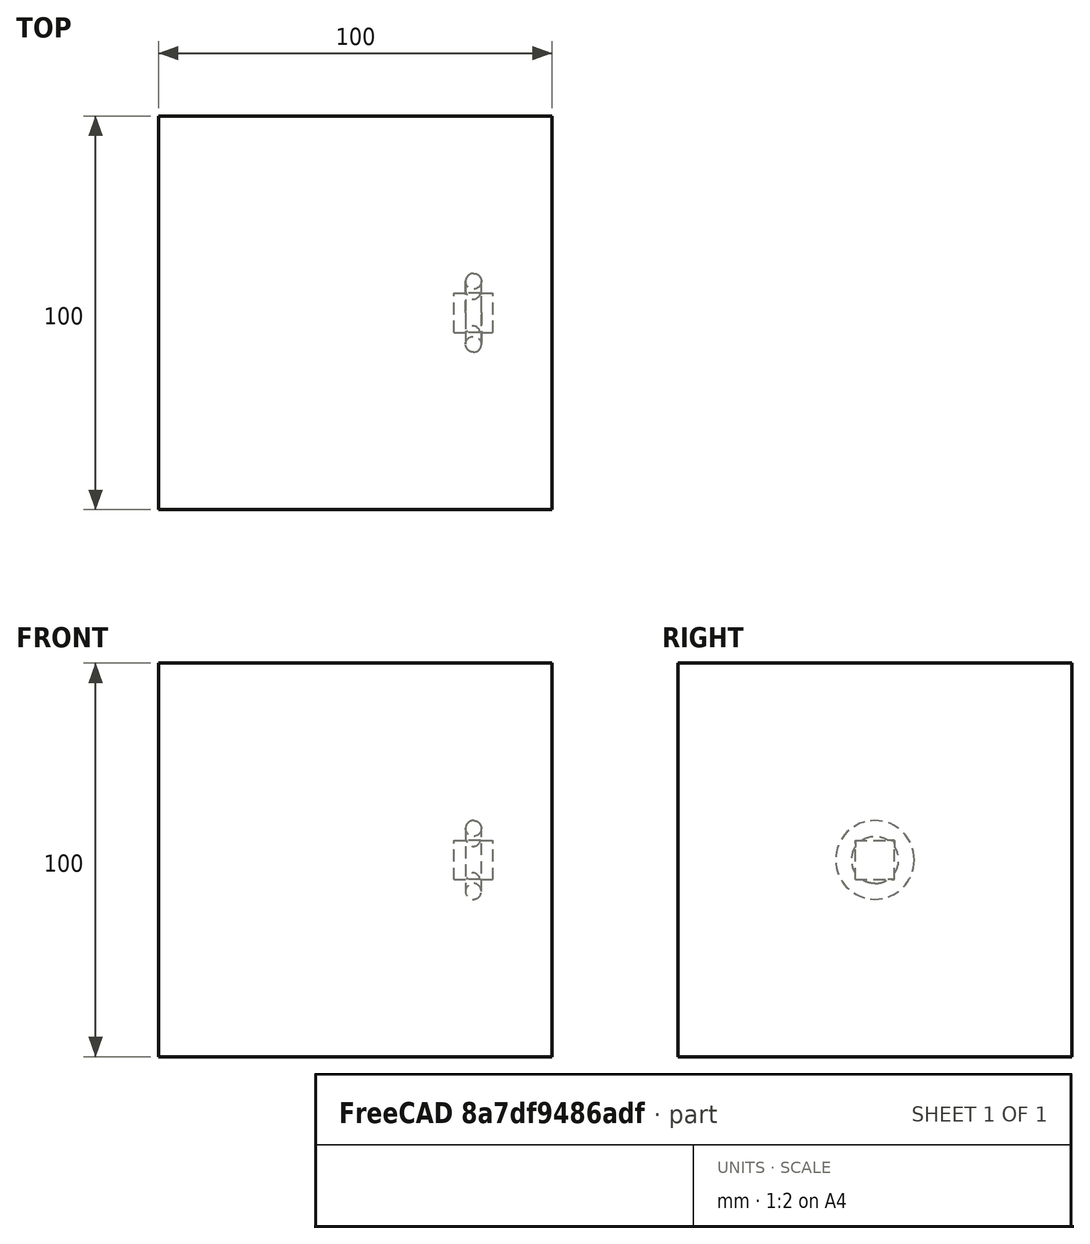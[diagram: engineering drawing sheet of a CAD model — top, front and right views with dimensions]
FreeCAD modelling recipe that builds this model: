
FCSTD DOCUMENT  (FreeCAD 1.0R39109 (Git))
Label: polarArray-7
License: All rights reserved
objects: App::DocumentObjectGroupPython×1251, Part::FeaturePython×4, App::Part×2, Part::MultiFuse×1
note: 4 computed .brp shape members not serialized (recipe doc carries the construction recipe); baked Part::Feature solids carry a one-line shape summary decoded from their .brp

FEATURE [App::DocumentObjectGroupPython] HALFPI  # scripted group (container) (typed FeaturePython)
  name = HALFPI
  value = pi/2.
FEATURE [App::DocumentObjectGroupPython] PI  # scripted group (container) (typed FeaturePython)
  name = PI
  value = 1.*pi
FEATURE [App::DocumentObjectGroupPython] TWOPI  # scripted group (container) (typed FeaturePython)
  name = TWOPI
  value = 2.*pi
FEATURE [App::DocumentObjectGroupPython] Constants  # scripted group (container) (typed FeaturePython)
  Group = -> [HALFPI,PI,TWOPI]
FEATURE [App::DocumentObjectGroupPython] Variables  # scripted group (container) (typed FeaturePython)
FEATURE [App::DocumentObjectGroupPython] Quantities  # scripted group (container) (typed FeaturePython)
FEATURE [App::DocumentObjectGroupPython] Isotopes  # scripted group (container) (typed FeaturePython)
FEATURE [App::DocumentObjectGroupPython] Elements  # scripted group (container) (typed FeaturePython)
FEATURE [App::DocumentObjectGroupPython] Matrix  # scripted group (container) (typed FeaturePython)
FEATURE [App::DocumentObjectGroupPython] Surfaces  # scripted group (container) (typed FeaturePython)
FEATURE [App::DocumentObjectGroupPython] Opticals  # scripted group (container) (typed FeaturePython)
  Group = -> [Matrix,Surfaces]
FEATURE [App::DocumentObjectGroupPython] G4Isotopes  # scripted group (container) (typed FeaturePython)
FEATURE [App::DocumentObjectGroupPython] H_element  # scripted group (container) (typed FeaturePython)
  Z = 1
  atom_value = 1.008
  formula = H
  name = H_element
FEATURE [App::DocumentObjectGroupPython] He_element  # scripted group (container) (typed FeaturePython)
  Z = 2
  atom_value = 4.0026
  formula = He
  name = He_element
FEATURE [App::DocumentObjectGroupPython] Li_element  # scripted group (container) (typed FeaturePython)
  Z = 3
  atom_value = 6.94
  formula = Li
  name = Li_element
FEATURE [App::DocumentObjectGroupPython] Be_element  # scripted group (container) (typed FeaturePython)
  Z = 4
  atom_value = 9.01218
  formula = Be
  name = Be_element
FEATURE [App::DocumentObjectGroupPython] B_element  # scripted group (container) (typed FeaturePython)
  Z = 5
  atom_value = 10.81
  formula = B
  name = B_element
FEATURE [App::DocumentObjectGroupPython] C_element  # scripted group (container) (typed FeaturePython)
  Z = 6
  atom_value = 12.011
  formula = C
  name = C_element
FEATURE [App::DocumentObjectGroupPython] N_element  # scripted group (container) (typed FeaturePython)
  Z = 7
  atom_value = 14.007
  formula = N
  name = N_element
FEATURE [App::DocumentObjectGroupPython] O_element  # scripted group (container) (typed FeaturePython)
  Z = 8
  atom_value = 15.999
  formula = O
  name = O_element
FEATURE [App::DocumentObjectGroupPython] F_element  # scripted group (container) (typed FeaturePython)
  Z = 9
  atom_value = 18.9984
  formula = F
  name = F_element
FEATURE [App::DocumentObjectGroupPython] Ne_element  # scripted group (container) (typed FeaturePython)
  Z = 10
  atom_value = 20.1797
  formula = Ne
  name = Ne_element
FEATURE [App::DocumentObjectGroupPython] Na_element  # scripted group (container) (typed FeaturePython)
  Z = 11
  atom_value = 22.9898
  formula = Na
  name = Na_element
FEATURE [App::DocumentObjectGroupPython] Mg_element  # scripted group (container) (typed FeaturePython)
  Z = 12
  atom_value = 24.305
  formula = Mg
  name = Mg_element
FEATURE [App::DocumentObjectGroupPython] Al_element  # scripted group (container) (typed FeaturePython)
  Z = 13
  atom_value = 26.9815
  formula = Al
  name = Al_element
FEATURE [App::DocumentObjectGroupPython] Si_element  # scripted group (container) (typed FeaturePython)
  Z = 14
  atom_value = 28.085
  formula = Si
  name = Si_element
FEATURE [App::DocumentObjectGroupPython] P_element  # scripted group (container) (typed FeaturePython)
  Z = 15
  atom_value = 30.9738
  formula = P
  name = P_element
FEATURE [App::DocumentObjectGroupPython] S_element  # scripted group (container) (typed FeaturePython)
  Z = 16
  atom_value = 32.06
  formula = S
  name = S_element
FEATURE [App::DocumentObjectGroupPython] Cl_element  # scripted group (container) (typed FeaturePython)
  Z = 17
  atom_value = 35.45
  formula = Cl
  name = Cl_element
FEATURE [App::DocumentObjectGroupPython] Ar_element  # scripted group (container) (typed FeaturePython)
  Z = 18
  atom_value = 39.95
  formula = Ar
  name = Ar_element
FEATURE [App::DocumentObjectGroupPython] K_element  # scripted group (container) (typed FeaturePython)
  Z = 19
  atom_value = 39.0983
  formula = K
  name = K_element
FEATURE [App::DocumentObjectGroupPython] Ca_element  # scripted group (container) (typed FeaturePython)
  Z = 20
  atom_value = 40.078
  formula = Ca
  name = Ca_element
FEATURE [App::DocumentObjectGroupPython] Sc_element  # scripted group (container) (typed FeaturePython)
  Z = 21
  atom_value = 44.9559
  formula = Sc
  name = Sc_element
FEATURE [App::DocumentObjectGroupPython] Ti_element  # scripted group (container) (typed FeaturePython)
  Z = 22
  atom_value = 47.867
  formula = Ti
  name = Ti_element
FEATURE [App::DocumentObjectGroupPython] V_element  # scripted group (container) (typed FeaturePython)
  Z = 23
  atom_value = 50.9415
  formula = V
  name = V_element
FEATURE [App::DocumentObjectGroupPython] Cr_element  # scripted group (container) (typed FeaturePython)
  Z = 24
  atom_value = 51.9961
  formula = Cr
  name = Cr_element
FEATURE [App::DocumentObjectGroupPython] Mn_element  # scripted group (container) (typed FeaturePython)
  Z = 25
  atom_value = 54.938
  formula = Mn
  name = Mn_element
FEATURE [App::DocumentObjectGroupPython] Fe_element  # scripted group (container) (typed FeaturePython)
  Z = 26
  atom_value = 55.845
  formula = Fe
  name = Fe_element
FEATURE [App::DocumentObjectGroupPython] Co_element  # scripted group (container) (typed FeaturePython)
  Z = 27
  atom_value = 58.9332
  formula = Co
  name = Co_element
FEATURE [App::DocumentObjectGroupPython] Ni_element  # scripted group (container) (typed FeaturePython)
  Z = 28
  atom_value = 58.6934
  formula = Ni
  name = Ni_element
FEATURE [App::DocumentObjectGroupPython] Cu_element  # scripted group (container) (typed FeaturePython)
  Z = 29
  atom_value = 63.546
  formula = Cu
  name = Cu_element
FEATURE [App::DocumentObjectGroupPython] Zn_element  # scripted group (container) (typed FeaturePython)
  Z = 30
  atom_value = 65.38
  formula = Zn
  name = Zn_element
FEATURE [App::DocumentObjectGroupPython] Ga_element  # scripted group (container) (typed FeaturePython)
  Z = 31
  atom_value = 69.723
  formula = Ga
  name = Ga_element
FEATURE [App::DocumentObjectGroupPython] Ge_element  # scripted group (container) (typed FeaturePython)
  Z = 32
  atom_value = 72.63
  formula = Ge
  name = Ge_element
FEATURE [App::DocumentObjectGroupPython] As_element  # scripted group (container) (typed FeaturePython)
  Z = 33
  atom_value = 74.9216
  formula = As
  name = As_element
FEATURE [App::DocumentObjectGroupPython] Se_element  # scripted group (container) (typed FeaturePython)
  Z = 34
  atom_value = 78.971
  formula = Se
  name = Se_element
FEATURE [App::DocumentObjectGroupPython] Br_element  # scripted group (container) (typed FeaturePython)
  Z = 35
  atom_value = 79.904
  formula = Br
  name = Br_element
FEATURE [App::DocumentObjectGroupPython] Kr_element  # scripted group (container) (typed FeaturePython)
  Z = 36
  atom_value = 83.798
  formula = Kr
  name = Kr_element
FEATURE [App::DocumentObjectGroupPython] Rb_element  # scripted group (container) (typed FeaturePython)
  Z = 37
  atom_value = 85.4678
  formula = Rb
  name = Rb_element
FEATURE [App::DocumentObjectGroupPython] Sr_element  # scripted group (container) (typed FeaturePython)
  Z = 38
  atom_value = 87.62
  formula = Sr
  name = Sr_element
FEATURE [App::DocumentObjectGroupPython] Y_element  # scripted group (container) (typed FeaturePython)
  Z = 39
  atom_value = 88.9058
  formula = Y
  name = Y_element
FEATURE [App::DocumentObjectGroupPython] Zr_element  # scripted group (container) (typed FeaturePython)
  Z = 40
  atom_value = 91.224
  formula = Zr
  name = Zr_element
FEATURE [App::DocumentObjectGroupPython] Nb_element  # scripted group (container) (typed FeaturePython)
  Z = 41
  atom_value = 92.9064
  formula = Nb
  name = Nb_element
FEATURE [App::DocumentObjectGroupPython] Mo_element  # scripted group (container) (typed FeaturePython)
  Z = 42
  atom_value = 95.95
  formula = Mo
  name = Mo_element
FEATURE [App::DocumentObjectGroupPython] Tc_element  # scripted group (container) (typed FeaturePython)
  Z = 43
  atom_value = 97
  formula = Tc
  name = Tc_element
FEATURE [App::DocumentObjectGroupPython] Ru_element  # scripted group (container) (typed FeaturePython)
  Z = 44
  atom_value = 101.07
  formula = Ru
  name = Ru_element
FEATURE [App::DocumentObjectGroupPython] Rh_element  # scripted group (container) (typed FeaturePython)
  Z = 45
  atom_value = 102.905
  formula = Rh
  name = Rh_element
FEATURE [App::DocumentObjectGroupPython] Pd_element  # scripted group (container) (typed FeaturePython)
  Z = 46
  atom_value = 106.42
  formula = Pd
  name = Pd_element
FEATURE [App::DocumentObjectGroupPython] Ag_element  # scripted group (container) (typed FeaturePython)
  Z = 47
  atom_value = 107.868
  formula = Ag
  name = Ag_element
FEATURE [App::DocumentObjectGroupPython] Cd_element  # scripted group (container) (typed FeaturePython)
  Z = 48
  atom_value = 112.414
  formula = Cd
  name = Cd_element
FEATURE [App::DocumentObjectGroupPython] In_element  # scripted group (container) (typed FeaturePython)
  Z = 49
  atom_value = 114.818
  formula = In
  name = In_element
FEATURE [App::DocumentObjectGroupPython] Sn_element  # scripted group (container) (typed FeaturePython)
  Z = 50
  atom_value = 118.71
  formula = Sn
  name = Sn_element
FEATURE [App::DocumentObjectGroupPython] Sb_element  # scripted group (container) (typed FeaturePython)
  Z = 51
  atom_value = 121.76
  formula = Sb
  name = Sb_element
FEATURE [App::DocumentObjectGroupPython] Te_element  # scripted group (container) (typed FeaturePython)
  Z = 52
  atom_value = 127.6
  formula = Te
  name = Te_element
FEATURE [App::DocumentObjectGroupPython] I_element  # scripted group (container) (typed FeaturePython)
  Z = 53
  atom_value = 126.904
  formula = I
  name = I_element
FEATURE [App::DocumentObjectGroupPython] Xe_element  # scripted group (container) (typed FeaturePython)
  Z = 54
  atom_value = 131.293
  formula = Xe
  name = Xe_element
FEATURE [App::DocumentObjectGroupPython] Cs_element  # scripted group (container) (typed FeaturePython)
  Z = 55
  atom_value = 132.905
  formula = Cs
  name = Cs_element
FEATURE [App::DocumentObjectGroupPython] Ba_element  # scripted group (container) (typed FeaturePython)
  Z = 56
  atom_value = 137.327
  formula = Ba
  name = Ba_element
FEATURE [App::DocumentObjectGroupPython] La_element  # scripted group (container) (typed FeaturePython)
  Z = 57
  atom_value = 138.905
  formula = La
  name = La_element
FEATURE [App::DocumentObjectGroupPython] Ce_element  # scripted group (container) (typed FeaturePython)
  Z = 58
  atom_value = 140.116
  formula = Ce
  name = Ce_element
FEATURE [App::DocumentObjectGroupPython] Pr_element  # scripted group (container) (typed FeaturePython)
  Z = 59
  atom_value = 140.908
  formula = Pr
  name = Pr_element
FEATURE [App::DocumentObjectGroupPython] Nd_element  # scripted group (container) (typed FeaturePython)
  Z = 60
  atom_value = 144.242
  formula = Nd
  name = Nd_element
FEATURE [App::DocumentObjectGroupPython] Pm_element  # scripted group (container) (typed FeaturePython)
  Z = 61
  atom_value = 145
  formula = Pm
  name = Pm_element
FEATURE [App::DocumentObjectGroupPython] Sm_element  # scripted group (container) (typed FeaturePython)
  Z = 62
  atom_value = 150.36
  formula = Sm
  name = Sm_element
FEATURE [App::DocumentObjectGroupPython] Eu_element  # scripted group (container) (typed FeaturePython)
  Z = 63
  atom_value = 151.964
  formula = Eu
  name = Eu_element
FEATURE [App::DocumentObjectGroupPython] Gd_element  # scripted group (container) (typed FeaturePython)
  Z = 64
  atom_value = 157.25
  formula = Gd
  name = Gd_element
FEATURE [App::DocumentObjectGroupPython] Tb_element  # scripted group (container) (typed FeaturePython)
  Z = 65
  atom_value = 158.925
  formula = Tb
  name = Tb_element
FEATURE [App::DocumentObjectGroupPython] Dy_element  # scripted group (container) (typed FeaturePython)
  Z = 66
  atom_value = 162.5
  formula = Dy
  name = Dy_element
FEATURE [App::DocumentObjectGroupPython] Ho_element  # scripted group (container) (typed FeaturePython)
  Z = 67
  atom_value = 164.93
  formula = Ho
  name = Ho_element
FEATURE [App::DocumentObjectGroupPython] Er_element  # scripted group (container) (typed FeaturePython)
  Z = 68
  atom_value = 167.259
  formula = Er
  name = Er_element
FEATURE [App::DocumentObjectGroupPython] Tm_element  # scripted group (container) (typed FeaturePython)
  Z = 69
  atom_value = 168.934
  formula = Tm
  name = Tm_element
FEATURE [App::DocumentObjectGroupPython] Yb_element  # scripted group (container) (typed FeaturePython)
  Z = 70
  atom_value = 173.045
  formula = Yb
  name = Yb_element
FEATURE [App::DocumentObjectGroupPython] Lu_element  # scripted group (container) (typed FeaturePython)
  Z = 71
  atom_value = 174.967
  formula = Lu
  name = Lu_element
FEATURE [App::DocumentObjectGroupPython] Hf_element  # scripted group (container) (typed FeaturePython)
  Z = 72
  atom_value = 178.49
  formula = Hf
  name = Hf_element
FEATURE [App::DocumentObjectGroupPython] Ta_element  # scripted group (container) (typed FeaturePython)
  Z = 73
  atom_value = 180.948
  formula = Ta
  name = Ta_element
FEATURE [App::DocumentObjectGroupPython] W_element  # scripted group (container) (typed FeaturePython)
  Z = 74
  atom_value = 183.84
  formula = W
  name = W_element
FEATURE [App::DocumentObjectGroupPython] Re_element  # scripted group (container) (typed FeaturePython)
  Z = 75
  atom_value = 186.207
  formula = Re
  name = Re_element
FEATURE [App::DocumentObjectGroupPython] Os_element  # scripted group (container) (typed FeaturePython)
  Z = 76
  atom_value = 190.23
  formula = Os
  name = Os_element
FEATURE [App::DocumentObjectGroupPython] Ir_element  # scripted group (container) (typed FeaturePython)
  Z = 77
  atom_value = 192.217
  formula = Ir
  name = Ir_element
FEATURE [App::DocumentObjectGroupPython] Pt_element  # scripted group (container) (typed FeaturePython)
  Z = 78
  atom_value = 195.084
  formula = Pt
  name = Pt_element
FEATURE [App::DocumentObjectGroupPython] Au_element  # scripted group (container) (typed FeaturePython)
  Z = 79
  atom_value = 196.967
  formula = Au
  name = Au_element
FEATURE [App::DocumentObjectGroupPython] Hg_element  # scripted group (container) (typed FeaturePython)
  Z = 80
  atom_value = 200.592
  formula = Hg
  name = Hg_element
FEATURE [App::DocumentObjectGroupPython] Tl_element  # scripted group (container) (typed FeaturePython)
  Z = 81
  atom_value = 204.38
  formula = Tl
  name = Tl_element
FEATURE [App::DocumentObjectGroupPython] Pb_element  # scripted group (container) (typed FeaturePython)
  Z = 82
  atom_value = 207.2
  formula = Pb
  name = Pb_element
FEATURE [App::DocumentObjectGroupPython] Bi_element  # scripted group (container) (typed FeaturePython)
  Z = 83
  atom_value = 208.98
  formula = Bi
  name = Bi_element
FEATURE [App::DocumentObjectGroupPython] Po_element  # scripted group (container) (typed FeaturePython)
  Z = 84
  atom_value = 209
  formula = Po
  name = Po_element
FEATURE [App::DocumentObjectGroupPython] At_element  # scripted group (container) (typed FeaturePython)
  Z = 85
  atom_value = 210
  formula = At
  name = At_element
FEATURE [App::DocumentObjectGroupPython] Rn_element  # scripted group (container) (typed FeaturePython)
  Z = 86
  atom_value = 222
  formula = Rn
  name = Rn_element
FEATURE [App::DocumentObjectGroupPython] Fr_element  # scripted group (container) (typed FeaturePython)
  Z = 87
  atom_value = 223
  formula = Fr
  name = Fr_element
FEATURE [App::DocumentObjectGroupPython] Ra_element  # scripted group (container) (typed FeaturePython)
  Z = 88
  atom_value = 226
  formula = Ra
  name = Ra_element
FEATURE [App::DocumentObjectGroupPython] Ac_element  # scripted group (container) (typed FeaturePython)
  Z = 89
  atom_value = 227
  formula = Ac
  name = Ac_element
FEATURE [App::DocumentObjectGroupPython] Th_element  # scripted group (container) (typed FeaturePython)
  Z = 90
  atom_value = 232.038
  formula = Th
  name = Th_element
FEATURE [App::DocumentObjectGroupPython] Pa_element  # scripted group (container) (typed FeaturePython)
  Z = 91
  atom_value = 231.036
  formula = Pa
  name = Pa_element
FEATURE [App::DocumentObjectGroupPython] U_element  # scripted group (container) (typed FeaturePython)
  Z = 92
  atom_value = 238.029
  formula = U
  name = U_element
FEATURE [App::DocumentObjectGroupPython] Np_element  # scripted group (container) (typed FeaturePython)
  Z = 93
  atom_value = 237
  formula = Np
  name = Np_element
FEATURE [App::DocumentObjectGroupPython] Pu_element  # scripted group (container) (typed FeaturePython)
  Z = 94
  atom_value = 244
  formula = Pu
  name = Pu_element
FEATURE [App::DocumentObjectGroupPython] Am_element  # scripted group (container) (typed FeaturePython)
  Z = 95
  atom_value = 243
  formula = Am
  name = Am_element
FEATURE [App::DocumentObjectGroupPython] Cm_element  # scripted group (container) (typed FeaturePython)
  Z = 96
  atom_value = 247
  formula = Cm
  name = Cm_element
FEATURE [App::DocumentObjectGroupPython] Bk_element  # scripted group (container) (typed FeaturePython)
  Z = 97
  atom_value = 247
  formula = Bk
  name = Bk_element
FEATURE [App::DocumentObjectGroupPython] Cf_element  # scripted group (container) (typed FeaturePython)
  Z = 98
  atom_value = 251
  formula = Cf
  name = Cf_element
FEATURE [App::DocumentObjectGroupPython] G4Elements  # scripted group (container) (typed FeaturePython)
  Group = -> [H_element,He_element,Li_element,Be_element,B_element,C_element,N_element,O_element,F_element,Ne_element,Na_element,Mg_element,Al_element,Si_element,P_element,S_element,Cl_element,Ar_element,K_element,Ca_element,Sc_element,Ti_element,V_element,Cr_element,Mn_element,Fe_element,Co_element,Ni_element,Cu_element,Zn_element,Ga_element,Ge_element,As_element,Se_element,Br_element,Kr_element,Rb_element,+61 more]
FEATURE [App::DocumentObjectGroupPython] H_element001  label="H_element : 0.101"  # scripted group (container) (typed FeaturePython)
  n = 0.101327
FEATURE [App::DocumentObjectGroupPython] C_element001  label="C_element : 0.775"  # scripted group (container) (typed FeaturePython)
  n = 0.7755
FEATURE [App::DocumentObjectGroupPython] N_element001  label="N_element : 0.035"  # scripted group (container) (typed FeaturePython)
  n = 0.035057
FEATURE [App::DocumentObjectGroupPython] O_element001  label="O_element : 0.052"  # scripted group (container) (typed FeaturePython)
  n = 0.0523159
FEATURE [App::DocumentObjectGroupPython] F_element001  label="F_element : 0.017"  # scripted group (container) (typed FeaturePython)
  n = 0.017422
FEATURE [App::DocumentObjectGroupPython] Ca_element001  label="Ca_element : 0.018"  # scripted group (container) (typed FeaturePython)
  n = 0.018378
FEATURE [App::DocumentObjectGroupPython] G4_A_150_TISSUE  label="G4_A-150_TISSUE"  # scripted group (container) (typed FeaturePython)
  Dunit = g/cm3
  Dvalue = 1.127
  Group = -> [H_element001,C_element001,N_element001,O_element001,F_element001,Ca_element001]
  conduct = 2
  density = 1
  expand = 3
  formula = G4_A-150_TISSUE
  name = G4_A-150_TISSUE
  specific = 4
FEATURE [App::DocumentObjectGroupPython] C_element002  label="C_element : 3"  # scripted group (container) (typed FeaturePython)
  n = 3
  ref = C_element
FEATURE [App::DocumentObjectGroupPython] H_element002  label="H_element : 6"  # scripted group (container) (typed FeaturePython)
  n = 6
  ref = H_element
FEATURE [App::DocumentObjectGroupPython] O_element002  label="O_element : 1"  # scripted group (container) (typed FeaturePython)
  n = 1
  ref = O_element
FEATURE [App::DocumentObjectGroupPython] G4_ACETONE  # scripted group (container) (typed FeaturePython)
  Dunit = g/cm3
  Dvalue = 0.7899
  Group = -> [C_element002,H_element002,O_element002]
  conduct = 2
  density = 1
  expand = 3
  formula = G4_ACETONE
  name = G4_ACETONE
  specific = 4
FEATURE [App::DocumentObjectGroupPython] C_element003  label="C_element : 2"  # scripted group (container) (typed FeaturePython)
  n = 2
  ref = C_element
FEATURE [App::DocumentObjectGroupPython] H_element003  label="H_element : 2"  # scripted group (container) (typed FeaturePython)
  n = 2
  ref = H_element
FEATURE [App::DocumentObjectGroupPython] G4_ACETYLENE  # scripted group (container) (typed FeaturePython)
  Dunit = g/cm3
  Dvalue = 0.0010967
  Group = -> [C_element003,H_element003]
  conduct = 2
  density = 1
  expand = 3
  formula = G4_ACETYLENE
  name = G4_ACETYLENE
  specific = 4
FEATURE [App::DocumentObjectGroupPython] C_element004  label="C_element : 5"  # scripted group (container) (typed FeaturePython)
  n = 5
  ref = C_element
FEATURE [App::DocumentObjectGroupPython] H_element004  label="H_element : 5"  # scripted group (container) (typed FeaturePython)
  n = 5
  ref = H_element
FEATURE [App::DocumentObjectGroupPython] N_element002  label="N_element : 5"  # scripted group (container) (typed FeaturePython)
  n = 5
  ref = N_element
FEATURE [App::DocumentObjectGroupPython] G4_ADENINE  # scripted group (container) (typed FeaturePython)
  Dunit = g/cm3
  Dvalue = 1.6
  Group = -> [C_element004,H_element004,N_element002]
  conduct = 2
  density = 1
  expand = 3
  formula = G4_ADENINE
  name = G4_ADENINE
  specific = 4
FEATURE [App::DocumentObjectGroupPython] H_element005  label="H_element : 0.114"  # scripted group (container) (typed FeaturePython)
  n = 0.114
FEATURE [App::DocumentObjectGroupPython] C_element005  label="C_element : 0.598"  # scripted group (container) (typed FeaturePython)
  n = 0.598
FEATURE [App::DocumentObjectGroupPython] N_element003  label="N_element : 0.007"  # scripted group (container) (typed FeaturePython)
  n = 0.007
FEATURE [App::DocumentObjectGroupPython] O_element003  label="O_element : 0.278"  # scripted group (container) (typed FeaturePython)
  n = 0.278
FEATURE [App::DocumentObjectGroupPython] Na_element001  label="Na_element : 0.001"  # scripted group (container) (typed FeaturePython)
  n = 0.001
FEATURE [App::DocumentObjectGroupPython] S_element001  label="S_element : 0.001"  # scripted group (container) (typed FeaturePython)
  n = 0.001
FEATURE [App::DocumentObjectGroupPython] Cl_element001  label="Cl_element : 0.001"  # scripted group (container) (typed FeaturePython)
  n = 0.001
FEATURE [App::DocumentObjectGroupPython] G4_ADIPOSE_TISSUE_ICRP  # scripted group (container) (typed FeaturePython)
  Dunit = g/cm3
  Dvalue = 0.95
  Group = -> [H_element005,C_element005,N_element003,O_element003,Na_element001,S_element001,Cl_element001]
  conduct = 2
  density = 1
  expand = 3
  formula = G4_ADIPOSE_TISSUE_ICRP
  name = G4_ADIPOSE_TISSUE_ICRP
  specific = 4
FEATURE [App::DocumentObjectGroupPython] C_element006  label="C_element : 0.000"  # scripted group (container) (typed FeaturePython)
  n = 0.000124
FEATURE [App::DocumentObjectGroupPython] N_element004  label="N_element : 0.755"  # scripted group (container) (typed FeaturePython)
  n = 0.755268
FEATURE [App::DocumentObjectGroupPython] O_element004  label="O_element : 0.232"  # scripted group (container) (typed FeaturePython)
  n = 0.231781
FEATURE [App::DocumentObjectGroupPython] Ar_element001  label="Ar_element : 0.013"  # scripted group (container) (typed FeaturePython)
  n = 0.012827
FEATURE [App::DocumentObjectGroupPython] G4_AIR  # scripted group (container) (typed FeaturePython)
  Dunit = g/cm3
  Dvalue = 0.00120479
  Group = -> [C_element006,N_element004,O_element004,Ar_element001]
  conduct = 2
  density = 1
  expand = 3
  formula = G4_AIR
  name = G4_AIR
  specific = 4
FEATURE [App::DocumentObjectGroupPython] C_element007  label="C_element : 006"  # scripted group (container) (typed FeaturePython)
  n = 3
  ref = C_element
FEATURE [App::DocumentObjectGroupPython] H_element006  label="H_element : 7"  # scripted group (container) (typed FeaturePython)
  n = 7
  ref = H_element
FEATURE [App::DocumentObjectGroupPython] N_element005  label="N_element : 1"  # scripted group (container) (typed FeaturePython)
  n = 1
  ref = N_element
FEATURE [App::DocumentObjectGroupPython] O_element005  label="O_element : 2"  # scripted group (container) (typed FeaturePython)
  n = 2
  ref = O_element
FEATURE [App::DocumentObjectGroupPython] G4_ALANINE  # scripted group (container) (typed FeaturePython)
  Dunit = g/cm3
  Dvalue = 1.42
  Group = -> [C_element007,H_element006,N_element005,O_element005]
  conduct = 2
  density = 1
  expand = 3
  formula = G4_ALANINE
  name = G4_ALANINE
  specific = 4
FEATURE [App::DocumentObjectGroupPython] Al_element001  label="Al_element : 2"  # scripted group (container) (typed FeaturePython)
  n = 2
  ref = Al_element
FEATURE [App::DocumentObjectGroupPython] O_element006  label="O_element : 3"  # scripted group (container) (typed FeaturePython)
  n = 3
  ref = O_element
FEATURE [App::DocumentObjectGroupPython] G4_ALUMINUM_OXIDE  # scripted group (container) (typed FeaturePython)
  Dunit = g/cm3
  Dvalue = 3.97
  Group = -> [Al_element001,O_element006]
  conduct = 2
  density = 1
  expand = 3
  formula = G4_ALUMINUM_OXIDE
  name = G4_ALUMINUM_OXIDE
  specific = 4
FEATURE [App::DocumentObjectGroupPython] H_element007  label="H_element : 0.106"  # scripted group (container) (typed FeaturePython)
  n = 0.10593
FEATURE [App::DocumentObjectGroupPython] C_element008  label="C_element : 0.789"  # scripted group (container) (typed FeaturePython)
  n = 0.788974
FEATURE [App::DocumentObjectGroupPython] O_element007  label="O_element : 0.105"  # scripted group (container) (typed FeaturePython)
  n = 0.105096
FEATURE [App::DocumentObjectGroupPython] G4_AMBER  # scripted group (container) (typed FeaturePython)
  Dunit = g/cm3
  Dvalue = 1.1
  Group = -> [H_element007,C_element008,O_element007]
  conduct = 2
  density = 1
  expand = 3
  formula = G4_AMBER
  name = G4_AMBER
  specific = 4
FEATURE [App::DocumentObjectGroupPython] N_element006  label="N_element : 006"  # scripted group (container) (typed FeaturePython)
  n = 1
  ref = N_element
FEATURE [App::DocumentObjectGroupPython] H_element008  label="H_element : 3"  # scripted group (container) (typed FeaturePython)
  n = 3
  ref = H_element
FEATURE [App::DocumentObjectGroupPython] G4_AMMONIA  # scripted group (container) (typed FeaturePython)
  Dunit = g/cm3
  Dvalue = 0.000826019
  Group = -> [N_element006,H_element008]
  conduct = 2
  density = 1
  expand = 3
  formula = G4_AMMONIA
  name = G4_AMMONIA
  specific = 4
FEATURE [App::DocumentObjectGroupPython] C_element009  label="C_element : 6"  # scripted group (container) (typed FeaturePython)
  n = 6
  ref = C_element
FEATURE [App::DocumentObjectGroupPython] H_element009  label="H_element : 008"  # scripted group (container) (typed FeaturePython)
  n = 7
  ref = H_element
FEATURE [App::DocumentObjectGroupPython] N_element007  label="N_element : 007"  # scripted group (container) (typed FeaturePython)
  n = 1
  ref = N_element
FEATURE [App::DocumentObjectGroupPython] G4_ANILINE  # scripted group (container) (typed FeaturePython)
  Dunit = g/cm3
  Dvalue = 1.0235
  Group = -> [C_element009,H_element009,N_element007]
  conduct = 2
  density = 1
  expand = 3
  formula = G4_ANILINE
  name = G4_ANILINE
  specific = 4
FEATURE [App::DocumentObjectGroupPython] C_element010  label="C_element : 14"  # scripted group (container) (typed FeaturePython)
  n = 14
  ref = C_element
FEATURE [App::DocumentObjectGroupPython] H_element010  label="H_element : 10"  # scripted group (container) (typed FeaturePython)
  n = 10
  ref = H_element
FEATURE [App::DocumentObjectGroupPython] G4_ANTHRACENE  # scripted group (container) (typed FeaturePython)
  Dunit = g/cm3
  Dvalue = 1.283
  Group = -> [C_element010,H_element010]
  conduct = 2
  density = 1
  expand = 3
  formula = G4_ANTHRACENE
  name = G4_ANTHRACENE
  specific = 4
FEATURE [App::DocumentObjectGroupPython] H_element011  label="H_element : 0.065"  # scripted group (container) (typed FeaturePython)
  n = 0.0654709
FEATURE [App::DocumentObjectGroupPython] C_element011  label="C_element : 0.537"  # scripted group (container) (typed FeaturePython)
  n = 0.536944
FEATURE [App::DocumentObjectGroupPython] N_element008  label="N_element : 0.021"  # scripted group (container) (typed FeaturePython)
  n = 0.0215
FEATURE [App::DocumentObjectGroupPython] O_element008  label="O_element : 0.032"  # scripted group (container) (typed FeaturePython)
  n = 0.032085
FEATURE [App::DocumentObjectGroupPython] F_element002  label="F_element : 0.167"  # scripted group (container) (typed FeaturePython)
  n = 0.167411
FEATURE [App::DocumentObjectGroupPython] Ca_element002  label="Ca_element : 0.177"  # scripted group (container) (typed FeaturePython)
  n = 0.176589
FEATURE [App::DocumentObjectGroupPython] G4_B_100_BONE  label="G4_B-100_BONE"  # scripted group (container) (typed FeaturePython)
  Dunit = g/cm3
  Dvalue = 1.45
  Group = -> [H_element011,C_element011,N_element008,O_element008,F_element002,Ca_element002]
  conduct = 2
  density = 1
  expand = 3
  formula = G4_B-100_BONE
  name = G4_B-100_BONE
  specific = 4
FEATURE [App::DocumentObjectGroupPython] H_element012  label="H_element : 0.057"  # scripted group (container) (typed FeaturePython)
  n = 0.057441
FEATURE [App::DocumentObjectGroupPython] C_element012  label="C_element : 0.790"  # scripted group (container) (typed FeaturePython)
  n = 0.774591
FEATURE [App::DocumentObjectGroupPython] O_element009  label="O_element : 0.168"  # scripted group (container) (typed FeaturePython)
  n = 0.167968
FEATURE [App::DocumentObjectGroupPython] G4_BAKELITE  # scripted group (container) (typed FeaturePython)
  Dunit = g/cm3
  Dvalue = 1.25
  Group = -> [H_element012,C_element012,O_element009]
  conduct = 2
  density = 1
  expand = 3
  formula = G4_BAKELITE
  name = G4_BAKELITE
  specific = 4
FEATURE [App::DocumentObjectGroupPython] Ba_element001  label="Ba_element : 1"  # scripted group (container) (typed FeaturePython)
  n = 1
  ref = Ba_element
FEATURE [App::DocumentObjectGroupPython] F_element003  label="F_element : 2"  # scripted group (container) (typed FeaturePython)
  n = 2
  ref = F_element
FEATURE [App::DocumentObjectGroupPython] G4_BARIUM_FLUORIDE  # scripted group (container) (typed FeaturePython)
  Dunit = g/cm3
  Dvalue = 4.89
  Group = -> [Ba_element001,F_element003]
  conduct = 2
  density = 1
  expand = 3
  formula = G4_BARIUM_FLUORIDE
  name = G4_BARIUM_FLUORIDE
  specific = 4
FEATURE [App::DocumentObjectGroupPython] Ba_element002  label="Ba_element : 002"  # scripted group (container) (typed FeaturePython)
  n = 1
  ref = Ba_element
FEATURE [App::DocumentObjectGroupPython] S_element002  label="S_element : 1"  # scripted group (container) (typed FeaturePython)
  n = 1
  ref = S_element
FEATURE [App::DocumentObjectGroupPython] O_element010  label="O_element : 4"  # scripted group (container) (typed FeaturePython)
  n = 4
  ref = O_element
FEATURE [App::DocumentObjectGroupPython] G4_BARIUM_SULFATE  # scripted group (container) (typed FeaturePython)
  Dunit = g/cm3
  Dvalue = 4.5
  Group = -> [Ba_element002,S_element002,O_element010]
  conduct = 2
  density = 1
  expand = 3
  formula = G4_BARIUM_SULFATE
  name = G4_BARIUM_SULFATE
  specific = 4
FEATURE [App::DocumentObjectGroupPython] C_element013  label="C_element : 007"  # scripted group (container) (typed FeaturePython)
  n = 6
  ref = C_element
FEATURE [App::DocumentObjectGroupPython] H_element013  label="H_element : 009"  # scripted group (container) (typed FeaturePython)
  n = 6
  ref = H_element
FEATURE [App::DocumentObjectGroupPython] G4_BENZENE  # scripted group (container) (typed FeaturePython)
  Dunit = g/cm3
  Dvalue = 0.87865
  Group = -> [C_element013,H_element013]
  conduct = 2
  density = 1
  expand = 3
  formula = G4_BENZENE
  name = G4_BENZENE
  specific = 4
FEATURE [App::DocumentObjectGroupPython] Be_element001  label="Be_element : 1"  # scripted group (container) (typed FeaturePython)
  n = 1
  ref = Be_element
FEATURE [App::DocumentObjectGroupPython] O_element011  label="O_element : 005"  # scripted group (container) (typed FeaturePython)
  n = 1
  ref = O_element
FEATURE [App::DocumentObjectGroupPython] G4_BERYLLIUM_OXIDE  # scripted group (container) (typed FeaturePython)
  Dunit = g/cm3
  Dvalue = 3.01
  Group = -> [Be_element001,O_element011]
  conduct = 2
  density = 1
  expand = 3
  formula = G4_BERYLLIUM_OXIDE
  name = G4_BERYLLIUM_OXIDE
  specific = 4
FEATURE [App::DocumentObjectGroupPython] Bi_element001  label="Bi_element : 4"  # scripted group (container) (typed FeaturePython)
  n = 4
  ref = Bi_element
FEATURE [App::DocumentObjectGroupPython] Ge_element001  label="Ge_element : 3"  # scripted group (container) (typed FeaturePython)
  n = 3
  ref = Ge_element
FEATURE [App::DocumentObjectGroupPython] O_element012  label="O_element : 12"  # scripted group (container) (typed FeaturePython)
  n = 12
  ref = O_element
FEATURE [App::DocumentObjectGroupPython] G4_BGO  # scripted group (container) (typed FeaturePython)
  Dunit = g/cm3
  Dvalue = 7.13
  Group = -> [Bi_element001,Ge_element001,O_element012]
  conduct = 2
  density = 1
  expand = 3
  formula = G4_BGO
  name = G4_BGO
  specific = 4
FEATURE [App::DocumentObjectGroupPython] H_element014  label="H_element : 0.102"  # scripted group (container) (typed FeaturePython)
  n = 0.102
FEATURE [App::DocumentObjectGroupPython] C_element014  label="C_element : 0.110"  # scripted group (container) (typed FeaturePython)
  n = 0.11
FEATURE [App::DocumentObjectGroupPython] N_element009  label="N_element : 0.033"  # scripted group (container) (typed FeaturePython)
  n = 0.033
FEATURE [App::DocumentObjectGroupPython] O_element013  label="O_element : 0.745"  # scripted group (container) (typed FeaturePython)
  n = 0.745
FEATURE [App::DocumentObjectGroupPython] Na_element002  label="Na_element : 0.002"  # scripted group (container) (typed FeaturePython)
  n = 0.001
FEATURE [App::DocumentObjectGroupPython] P_element001  label="P_element : 0.001"  # scripted group (container) (typed FeaturePython)
  n = 0.001
FEATURE [App::DocumentObjectGroupPython] S_element003  label="S_element : 0.002"  # scripted group (container) (typed FeaturePython)
  n = 0.002
FEATURE [App::DocumentObjectGroupPython] Cl_element002  label="Cl_element : 0.003"  # scripted group (container) (typed FeaturePython)
  n = 0.003
FEATURE [App::DocumentObjectGroupPython] K_element001  label="K_element : 0.002"  # scripted group (container) (typed FeaturePython)
  n = 0.002
FEATURE [App::DocumentObjectGroupPython] Fe_element001  label="Fe_element : 0.001"  # scripted group (container) (typed FeaturePython)
  n = 0.001
FEATURE [App::DocumentObjectGroupPython] G4_BLOOD_ICRP  # scripted group (container) (typed FeaturePython)
  Dunit = g/cm3
  Dvalue = 1.06
  Group = -> [H_element014,C_element014,N_element009,O_element013,Na_element002,P_element001,S_element003,Cl_element002,K_element001,Fe_element001]
  conduct = 2
  density = 1
  expand = 3
  formula = G4_BLOOD_ICRP
  name = G4_BLOOD_ICRP
  specific = 4
FEATURE [App::DocumentObjectGroupPython] H_element015  label="H_element : 0.064"  # scripted group (container) (typed FeaturePython)
  n = 0.064
FEATURE [App::DocumentObjectGroupPython] C_element015  label="C_element : 0.278"  # scripted group (container) (typed FeaturePython)
  n = 0.278
FEATURE [App::DocumentObjectGroupPython] N_element010  label="N_element : 0.027"  # scripted group (container) (typed FeaturePython)
  n = 0.027
FEATURE [App::DocumentObjectGroupPython] O_element014  label="O_element : 0.410"  # scripted group (container) (typed FeaturePython)
  n = 0.41
FEATURE [App::DocumentObjectGroupPython] Mg_element001  label="Mg_element : 0.002"  # scripted group (container) (typed FeaturePython)
  n = 0.002
FEATURE [App::DocumentObjectGroupPython] P_element002  label="P_element : 0.070"  # scripted group (container) (typed FeaturePython)
  n = 0.07
FEATURE [App::DocumentObjectGroupPython] S_element004  label="S_element : 0.003"  # scripted group (container) (typed FeaturePython)
  n = 0.002
FEATURE [App::DocumentObjectGroupPython] Ca_element003  label="Ca_element : 0.147"  # scripted group (container) (typed FeaturePython)
  n = 0.147
FEATURE [App::DocumentObjectGroupPython] G4_BONE_COMPACT_ICRU  # scripted group (container) (typed FeaturePython)
  Dunit = g/cm3
  Dvalue = 1.85
  Group = -> [H_element015,C_element015,N_element010,O_element014,Mg_element001,P_element002,S_element004,Ca_element003]
  conduct = 2
  density = 1
  expand = 3
  formula = G4_BONE_COMPACT_ICRU
  name = G4_BONE_COMPACT_ICRU
  specific = 4
FEATURE [App::DocumentObjectGroupPython] H_element016  label="H_element : 0.034"  # scripted group (container) (typed FeaturePython)
  n = 0.034
FEATURE [App::DocumentObjectGroupPython] C_element016  label="C_element : 0.155"  # scripted group (container) (typed FeaturePython)
  n = 0.155
FEATURE [App::DocumentObjectGroupPython] N_element011  label="N_element : 0.042"  # scripted group (container) (typed FeaturePython)
  n = 0.042
FEATURE [App::DocumentObjectGroupPython] O_element015  label="O_element : 0.435"  # scripted group (container) (typed FeaturePython)
  n = 0.435
FEATURE [App::DocumentObjectGroupPython] Na_element003  label="Na_element : 0.003"  # scripted group (container) (typed FeaturePython)
  n = 0.001
FEATURE [App::DocumentObjectGroupPython] Mg_element002  label="Mg_element : 0.003"  # scripted group (container) (typed FeaturePython)
  n = 0.002
FEATURE [App::DocumentObjectGroupPython] P_element003  label="P_element : 0.103"  # scripted group (container) (typed FeaturePython)
  n = 0.103
FEATURE [App::DocumentObjectGroupPython] S_element005  label="S_element : 0.004"  # scripted group (container) (typed FeaturePython)
  n = 0.003
FEATURE [App::DocumentObjectGroupPython] Ca_element004  label="Ca_element : 0.225"  # scripted group (container) (typed FeaturePython)
  n = 0.225
FEATURE [App::DocumentObjectGroupPython] G4_BONE_CORTICAL_ICRP  # scripted group (container) (typed FeaturePython)
  Dunit = g/cm3
  Dvalue = 1.92
  Group = -> [H_element016,C_element016,N_element011,O_element015,Na_element003,Mg_element002,P_element003,S_element005,Ca_element004]
  conduct = 2
  density = 1
  expand = 3
  formula = G4_BONE_CORTICAL_ICRP
  name = G4_BONE_CORTICAL_ICRP
  specific = 4
FEATURE [App::DocumentObjectGroupPython] B_element001  label="B_element : 4"  # scripted group (container) (typed FeaturePython)
  n = 4
  ref = B_element
FEATURE [App::DocumentObjectGroupPython] C_element017  label="C_element : 1"  # scripted group (container) (typed FeaturePython)
  n = 1
  ref = C_element
FEATURE [App::DocumentObjectGroupPython] G4_BORON_CARBIDE  # scripted group (container) (typed FeaturePython)
  Dunit = g/cm3
  Dvalue = 2.52
  Group = -> [B_element001,C_element017]
  conduct = 2
  density = 1
  expand = 3
  formula = G4_BORON_CARBIDE
  name = G4_BORON_CARBIDE
  specific = 4
FEATURE [App::DocumentObjectGroupPython] B_element002  label="B_element : 2"  # scripted group (container) (typed FeaturePython)
  n = 2
  ref = B_element
FEATURE [App::DocumentObjectGroupPython] O_element016  label="O_element : 006"  # scripted group (container) (typed FeaturePython)
  n = 3
  ref = O_element
FEATURE [App::DocumentObjectGroupPython] G4_BORON_OXIDE  # scripted group (container) (typed FeaturePython)
  Dunit = g/cm3
  Dvalue = 1.812
  Group = -> [B_element002,O_element016]
  conduct = 2
  density = 1
  expand = 3
  formula = G4_BORON_OXIDE
  name = G4_BORON_OXIDE
  specific = 4
FEATURE [App::DocumentObjectGroupPython] H_element017  label="H_element : 0.107"  # scripted group (container) (typed FeaturePython)
  n = 0.107
FEATURE [App::DocumentObjectGroupPython] C_element018  label="C_element : 0.145"  # scripted group (container) (typed FeaturePython)
  n = 0.145
FEATURE [App::DocumentObjectGroupPython] N_element012  label="N_element : 0.022"  # scripted group (container) (typed FeaturePython)
  n = 0.022
FEATURE [App::DocumentObjectGroupPython] O_element017  label="O_element : 0.712"  # scripted group (container) (typed FeaturePython)
  n = 0.712
FEATURE [App::DocumentObjectGroupPython] Na_element004  label="Na_element : 0.004"  # scripted group (container) (typed FeaturePython)
  n = 0.002
FEATURE [App::DocumentObjectGroupPython] P_element004  label="P_element : 0.004"  # scripted group (container) (typed FeaturePython)
  n = 0.004
FEATURE [App::DocumentObjectGroupPython] S_element006  label="S_element : 0.005"  # scripted group (container) (typed FeaturePython)
  n = 0.002
FEATURE [App::DocumentObjectGroupPython] Cl_element003  label="Cl_element : 0.004"  # scripted group (container) (typed FeaturePython)
  n = 0.003
FEATURE [App::DocumentObjectGroupPython] K_element002  label="K_element : 0.003"  # scripted group (container) (typed FeaturePython)
  n = 0.003
FEATURE [App::DocumentObjectGroupPython] G4_BRAIN_ICRP  # scripted group (container) (typed FeaturePython)
  Dunit = g/cm3
  Dvalue = 1.04
  Group = -> [H_element017,C_element018,N_element012,O_element017,Na_element004,P_element004,S_element006,Cl_element003,K_element002]
  conduct = 2
  density = 1
  expand = 3
  formula = G4_BRAIN_ICRP
  name = G4_BRAIN_ICRP
  specific = 4
FEATURE [App::DocumentObjectGroupPython] C_element019  label="C_element : 4"  # scripted group (container) (typed FeaturePython)
  n = 4
  ref = C_element
FEATURE [App::DocumentObjectGroupPython] H_element018  label="H_element : 010"  # scripted group (container) (typed FeaturePython)
  n = 10
  ref = H_element
FEATURE [App::DocumentObjectGroupPython] G4_BUTANE  # scripted group (container) (typed FeaturePython)
  Dunit = g/cm3
  Dvalue = 0.00249343
  Group = -> [C_element019,H_element018]
  conduct = 2
  density = 1
  expand = 3
  formula = G4_BUTANE
  name = G4_BUTANE
  specific = 4
FEATURE [App::DocumentObjectGroupPython] C_element020  label="C_element : 008"  # scripted group (container) (typed FeaturePython)
  n = 4
  ref = C_element
FEATURE [App::DocumentObjectGroupPython] H_element019  label="H_element : 011"  # scripted group (container) (typed FeaturePython)
  n = 10
  ref = H_element
FEATURE [App::DocumentObjectGroupPython] O_element018  label="O_element : 007"  # scripted group (container) (typed FeaturePython)
  n = 1
  ref = O_element
FEATURE [App::DocumentObjectGroupPython] G4_N_BUTYL_ALCOHOL  label="G4_N-BUTYL_ALCOHOL"  # scripted group (container) (typed FeaturePython)
  Dunit = g/cm3
  Dvalue = 0.8098
  Group = -> [C_element020,H_element019,O_element018]
  conduct = 2
  density = 1
  expand = 3
  formula = G4_N-BUTYL_ALCOHOL
  name = G4_N-BUTYL_ALCOHOL
  specific = 4
FEATURE [App::DocumentObjectGroupPython] H_element020  label="H_element : 0.025"  # scripted group (container) (typed FeaturePython)
  n = 0.02468
FEATURE [App::DocumentObjectGroupPython] C_element021  label="C_element : 0.502"  # scripted group (container) (typed FeaturePython)
  n = 0.501611
FEATURE [App::DocumentObjectGroupPython] O_element019  label="O_element : 0.005"  # scripted group (container) (typed FeaturePython)
  n = 0.004527
FEATURE [App::DocumentObjectGroupPython] F_element004  label="F_element : 0.465"  # scripted group (container) (typed FeaturePython)
  n = 0.465209
FEATURE [App::DocumentObjectGroupPython] Si_element001  label="Si_element : 0.004"  # scripted group (container) (typed FeaturePython)
  n = 0.003973
FEATURE [App::DocumentObjectGroupPython] G4_C_552  label="G4_C-552"  # scripted group (container) (typed FeaturePython)
  Dunit = g/cm3
  Dvalue = 1.76
  Group = -> [H_element020,C_element021,O_element019,F_element004,Si_element001]
  conduct = 2
  density = 1
  expand = 3
  formula = G4_C-552
  name = G4_C-552
  specific = 4
FEATURE [App::DocumentObjectGroupPython] Cd_element001  label="Cd_element : 1"  # scripted group (container) (typed FeaturePython)
  n = 1
  ref = Cd_element
FEATURE [App::DocumentObjectGroupPython] Te_element001  label="Te_element : 1"  # scripted group (container) (typed FeaturePython)
  n = 1
  ref = Te_element
FEATURE [App::DocumentObjectGroupPython] G4_CADMIUM_TELLURIDE  # scripted group (container) (typed FeaturePython)
  Dunit = g/cm3
  Dvalue = 6.2
  Group = -> [Cd_element001,Te_element001]
  conduct = 2
  density = 1
  expand = 3
  formula = G4_CADMIUM_TELLURIDE
  name = G4_CADMIUM_TELLURIDE
  specific = 4
FEATURE [App::DocumentObjectGroupPython] Cd_element002  label="Cd_element : 002"  # scripted group (container) (typed FeaturePython)
  n = 1
  ref = Cd_element
FEATURE [App::DocumentObjectGroupPython] W_element001  label="W_element : 1"  # scripted group (container) (typed FeaturePython)
  n = 1
  ref = W_element
FEATURE [App::DocumentObjectGroupPython] O_element020  label="O_element : 008"  # scripted group (container) (typed FeaturePython)
  n = 4
  ref = O_element
FEATURE [App::DocumentObjectGroupPython] G4_CADMIUM_TUNGSTATE  # scripted group (container) (typed FeaturePython)
  Dunit = g/cm3
  Dvalue = 7.9
  Group = -> [Cd_element002,W_element001,O_element020]
  conduct = 2
  density = 1
  expand = 3
  formula = G4_CADMIUM_TUNGSTATE
  name = G4_CADMIUM_TUNGSTATE
  specific = 4
FEATURE [App::DocumentObjectGroupPython] Ca_element005  label="Ca_element : 1"  # scripted group (container) (typed FeaturePython)
  n = 1
  ref = Ca_element
FEATURE [App::DocumentObjectGroupPython] C_element022  label="C_element : 009"  # scripted group (container) (typed FeaturePython)
  n = 1
  ref = C_element
FEATURE [App::DocumentObjectGroupPython] O_element021  label="O_element : 009"  # scripted group (container) (typed FeaturePython)
  n = 3
  ref = O_element
FEATURE [App::DocumentObjectGroupPython] G4_CALCIUM_CARBONATE  # scripted group (container) (typed FeaturePython)
  Dunit = g/cm3
  Dvalue = 2.8
  Group = -> [Ca_element005,C_element022,O_element021]
  conduct = 2
  density = 1
  expand = 3
  formula = G4_CALCIUM_CARBONATE
  name = G4_CALCIUM_CARBONATE
  specific = 4
FEATURE [App::DocumentObjectGroupPython] Ca_element006  label="Ca_element : 002"  # scripted group (container) (typed FeaturePython)
  n = 1
  ref = Ca_element
FEATURE [App::DocumentObjectGroupPython] F_element005  label="F_element : 003"  # scripted group (container) (typed FeaturePython)
  n = 2
  ref = F_element
FEATURE [App::DocumentObjectGroupPython] G4_CALCIUM_FLUORIDE  # scripted group (container) (typed FeaturePython)
  Dunit = g/cm3
  Dvalue = 3.18
  Group = -> [Ca_element006,F_element005]
  conduct = 2
  density = 1
  expand = 3
  formula = G4_CALCIUM_FLUORIDE
  name = G4_CALCIUM_FLUORIDE
  specific = 4
FEATURE [App::DocumentObjectGroupPython] Ca_element007  label="Ca_element : 003"  # scripted group (container) (typed FeaturePython)
  n = 1
  ref = Ca_element
FEATURE [App::DocumentObjectGroupPython] O_element022  label="O_element : 010"  # scripted group (container) (typed FeaturePython)
  n = 1
  ref = O_element
FEATURE [App::DocumentObjectGroupPython] G4_CALCIUM_OXIDE  # scripted group (container) (typed FeaturePython)
  Dunit = g/cm3
  Dvalue = 3.3
  Group = -> [Ca_element007,O_element022]
  conduct = 2
  density = 1
  expand = 3
  formula = G4_CALCIUM_OXIDE
  name = G4_CALCIUM_OXIDE
  specific = 4
FEATURE [App::DocumentObjectGroupPython] Ca_element008  label="Ca_element : 004"  # scripted group (container) (typed FeaturePython)
  n = 1
  ref = Ca_element
FEATURE [App::DocumentObjectGroupPython] S_element007  label="S_element : 002"  # scripted group (container) (typed FeaturePython)
  n = 1
  ref = S_element
FEATURE [App::DocumentObjectGroupPython] O_element023  label="O_element : 011"  # scripted group (container) (typed FeaturePython)
  n = 4
  ref = O_element
FEATURE [App::DocumentObjectGroupPython] G4_CALCIUM_SULFATE  # scripted group (container) (typed FeaturePython)
  Dunit = g/cm3
  Dvalue = 2.96
  Group = -> [Ca_element008,S_element007,O_element023]
  conduct = 2
  density = 1
  expand = 3
  formula = G4_CALCIUM_SULFATE
  name = G4_CALCIUM_SULFATE
  specific = 4
FEATURE [App::DocumentObjectGroupPython] Ca_element009  label="Ca_element : 005"  # scripted group (container) (typed FeaturePython)
  n = 1
  ref = Ca_element
FEATURE [App::DocumentObjectGroupPython] W_element002  label="W_element : 002"  # scripted group (container) (typed FeaturePython)
  n = 1
  ref = W_element
FEATURE [App::DocumentObjectGroupPython] O_element024  label="O_element : 012"  # scripted group (container) (typed FeaturePython)
  n = 4
  ref = O_element
FEATURE [App::DocumentObjectGroupPython] G4_CALCIUM_TUNGSTATE  # scripted group (container) (typed FeaturePython)
  Dunit = g/cm3
  Dvalue = 6.062
  Group = -> [Ca_element009,W_element002,O_element024]
  conduct = 2
  density = 1
  expand = 3
  formula = G4_CALCIUM_TUNGSTATE
  name = G4_CALCIUM_TUNGSTATE
  specific = 4
FEATURE [App::DocumentObjectGroupPython] C_element023  label="C_element : 010"  # scripted group (container) (typed FeaturePython)
  n = 1
  ref = C_element
FEATURE [App::DocumentObjectGroupPython] O_element025  label="O_element : 013"  # scripted group (container) (typed FeaturePython)
  n = 2
  ref = O_element
FEATURE [App::DocumentObjectGroupPython] G4_CARBON_DIOXIDE  # scripted group (container) (typed FeaturePython)
  Dunit = g/cm3
  Dvalue = 0.00184212
  Group = -> [C_element023,O_element025]
  conduct = 2
  density = 1
  expand = 3
  formula = G4_CARBON_DIOXIDE
  name = G4_CARBON_DIOXIDE
  specific = 4
FEATURE [App::DocumentObjectGroupPython] C_element024  label="C_element : 011"  # scripted group (container) (typed FeaturePython)
  n = 1
  ref = C_element
FEATURE [App::DocumentObjectGroupPython] Cl_element004  label="Cl_element : 4"  # scripted group (container) (typed FeaturePython)
  n = 4
  ref = Cl_element
FEATURE [App::DocumentObjectGroupPython] G4_CARBON_TETRACHLORIDE  # scripted group (container) (typed FeaturePython)
  Dunit = g/cm3
  Dvalue = 1.594
  Group = -> [C_element024,Cl_element004]
  conduct = 2
  density = 1
  expand = 3
  formula = G4_CARBON_TETRACHLORIDE
  name = G4_CARBON_TETRACHLORIDE
  specific = 4
FEATURE [App::DocumentObjectGroupPython] C_element025  label="C_element : 012"  # scripted group (container) (typed FeaturePython)
  n = 6
  ref = C_element
FEATURE [App::DocumentObjectGroupPython] H_element021  label="H_element : 012"  # scripted group (container) (typed FeaturePython)
  n = 10
  ref = H_element
FEATURE [App::DocumentObjectGroupPython] O_element026  label="O_element : 5"  # scripted group (container) (typed FeaturePython)
  n = 5
  ref = O_element
FEATURE [App::DocumentObjectGroupPython] G4_CELLULOSE_CELLOPHANE  # scripted group (container) (typed FeaturePython)
  Dunit = g/cm3
  Dvalue = 1.42
  Group = -> [C_element025,H_element021,O_element026]
  conduct = 2
  density = 1
  expand = 3
  formula = G4_CELLULOSE_CELLOPHANE
  name = G4_CELLULOSE_CELLOPHANE
  specific = 4
FEATURE [App::DocumentObjectGroupPython] H_element022  label="H_element : 0.067"  # scripted group (container) (typed FeaturePython)
  n = 0.067125
FEATURE [App::DocumentObjectGroupPython] C_element026  label="C_element : 0.545"  # scripted group (container) (typed FeaturePython)
  n = 0.545403
FEATURE [App::DocumentObjectGroupPython] O_element027  label="O_element : 0.387"  # scripted group (container) (typed FeaturePython)
  n = 0.387472
FEATURE [App::DocumentObjectGroupPython] G4_CELLULOSE_BUTYRATE  # scripted group (container) (typed FeaturePython)
  Dunit = g/cm3
  Dvalue = 1.2
  Group = -> [H_element022,C_element026,O_element027]
  conduct = 2
  density = 1
  expand = 3
  formula = G4_CELLULOSE_BUTYRATE
  name = G4_CELLULOSE_BUTYRATE
  specific = 4
FEATURE [App::DocumentObjectGroupPython] H_element023  label="H_element : 0.029"  # scripted group (container) (typed FeaturePython)
  n = 0.029216
FEATURE [App::DocumentObjectGroupPython] C_element027  label="C_element : 0.271"  # scripted group (container) (typed FeaturePython)
  n = 0.271296
FEATURE [App::DocumentObjectGroupPython] N_element013  label="N_element : 0.121"  # scripted group (container) (typed FeaturePython)
  n = 0.121276
FEATURE [App::DocumentObjectGroupPython] O_element028  label="O_element : 0.578"  # scripted group (container) (typed FeaturePython)
  n = 0.578212
FEATURE [App::DocumentObjectGroupPython] G4_CELLULOSE_NITRATE  # scripted group (container) (typed FeaturePython)
  Dunit = g/cm3
  Dvalue = 1.49
  Group = -> [H_element023,C_element027,N_element013,O_element028]
  conduct = 2
  density = 1
  expand = 3
  formula = G4_CELLULOSE_NITRATE
  name = G4_CELLULOSE_NITRATE
  specific = 4
FEATURE [App::DocumentObjectGroupPython] H_element024  label="H_element : 0.108"  # scripted group (container) (typed FeaturePython)
  n = 0.107596
FEATURE [App::DocumentObjectGroupPython] N_element014  label="N_element : 0.001"  # scripted group (container) (typed FeaturePython)
  n = 0.0008
FEATURE [App::DocumentObjectGroupPython] O_element029  label="O_element : 0.875"  # scripted group (container) (typed FeaturePython)
  n = 0.874976
FEATURE [App::DocumentObjectGroupPython] S_element008  label="S_element : 0.015"  # scripted group (container) (typed FeaturePython)
  n = 0.014627
FEATURE [App::DocumentObjectGroupPython] Ce_element001  label="Ce_element : 0.002"  # scripted group (container) (typed FeaturePython)
  n = 0.002001
FEATURE [App::DocumentObjectGroupPython] G4_CERIC_SULFATE  # scripted group (container) (typed FeaturePython)
  Dunit = g/cm3
  Dvalue = 1.03
  Group = -> [H_element024,N_element014,O_element029,S_element008,Ce_element001]
  conduct = 2
  density = 1
  expand = 3
  formula = G4_CERIC_SULFATE
  name = G4_CERIC_SULFATE
  specific = 4
FEATURE [App::DocumentObjectGroupPython] Cs_element001  label="Cs_element : 1"  # scripted group (container) (typed FeaturePython)
  n = 1
  ref = Cs_element
FEATURE [App::DocumentObjectGroupPython] F_element006  label="F_element : 1"  # scripted group (container) (typed FeaturePython)
  n = 1
  ref = F_element
FEATURE [App::DocumentObjectGroupPython] G4_CESIUM_FLUORIDE  # scripted group (container) (typed FeaturePython)
  Dunit = g/cm3
  Dvalue = 4.115
  Group = -> [Cs_element001,F_element006]
  conduct = 2
  density = 1
  expand = 3
  formula = G4_CESIUM_FLUORIDE
  name = G4_CESIUM_FLUORIDE
  specific = 4
FEATURE [App::DocumentObjectGroupPython] Cs_element002  label="Cs_element : 002"  # scripted group (container) (typed FeaturePython)
  n = 1
  ref = Cs_element
FEATURE [App::DocumentObjectGroupPython] I_element001  label="I_element : 1"  # scripted group (container) (typed FeaturePython)
  n = 1
  ref = I_element
FEATURE [App::DocumentObjectGroupPython] G4_CESIUM_IODIDE  # scripted group (container) (typed FeaturePython)
  Dunit = g/cm3
  Dvalue = 4.51
  Group = -> [Cs_element002,I_element001]
  conduct = 2
  density = 1
  expand = 3
  formula = G4_CESIUM_IODIDE
  name = G4_CESIUM_IODIDE
  specific = 4
FEATURE [App::DocumentObjectGroupPython] C_element028  label="C_element : 013"  # scripted group (container) (typed FeaturePython)
  n = 6
  ref = C_element
FEATURE [App::DocumentObjectGroupPython] H_element025  label="H_element : 013"  # scripted group (container) (typed FeaturePython)
  n = 5
  ref = H_element
FEATURE [App::DocumentObjectGroupPython] Cl_element005  label="Cl_element : 1"  # scripted group (container) (typed FeaturePython)
  n = 1
  ref = Cl_element
FEATURE [App::DocumentObjectGroupPython] G4_CHLOROBENZENE  # scripted group (container) (typed FeaturePython)
  Dunit = g/cm3
  Dvalue = 1.1058
  Group = -> [C_element028,H_element025,Cl_element005]
  conduct = 2
  density = 1
  expand = 3
  formula = G4_CHLOROBENZENE
  name = G4_CHLOROBENZENE
  specific = 4
FEATURE [App::DocumentObjectGroupPython] C_element029  label="C_element : 014"  # scripted group (container) (typed FeaturePython)
  n = 1
  ref = C_element
FEATURE [App::DocumentObjectGroupPython] H_element026  label="H_element : 1"  # scripted group (container) (typed FeaturePython)
  n = 1
  ref = H_element
FEATURE [App::DocumentObjectGroupPython] Cl_element006  label="Cl_element : 3"  # scripted group (container) (typed FeaturePython)
  n = 3
  ref = Cl_element
FEATURE [App::DocumentObjectGroupPython] G4_CHLOROFORM  # scripted group (container) (typed FeaturePython)
  Dunit = g/cm3
  Dvalue = 1.4832
  Group = -> [C_element029,H_element026,Cl_element006]
  conduct = 2
  density = 1
  expand = 3
  formula = G4_CHLOROFORM
  name = G4_CHLOROFORM
  specific = 4
FEATURE [App::DocumentObjectGroupPython] H_element027  label="H_element : 0.010"  # scripted group (container) (typed FeaturePython)
  n = 0.01
FEATURE [App::DocumentObjectGroupPython] C_element030  label="C_element : 0.001"  # scripted group (container) (typed FeaturePython)
  n = 0.001
FEATURE [App::DocumentObjectGroupPython] O_element030  label="O_element : 0.529"  # scripted group (container) (typed FeaturePython)
  n = 0.529107
FEATURE [App::DocumentObjectGroupPython] Na_element005  label="Na_element : 0.016"  # scripted group (container) (typed FeaturePython)
  n = 0.016
FEATURE [App::DocumentObjectGroupPython] Mg_element003  label="Mg_element : 0.004"  # scripted group (container) (typed FeaturePython)
  n = 0.002
FEATURE [App::DocumentObjectGroupPython] Al_element002  label="Al_element : 0.034"  # scripted group (container) (typed FeaturePython)
  n = 0.033872
FEATURE [App::DocumentObjectGroupPython] Si_element002  label="Si_element : 0.337"  # scripted group (container) (typed FeaturePython)
  n = 0.337021
FEATURE [App::DocumentObjectGroupPython] K_element003  label="K_element : 0.013"  # scripted group (container) (typed FeaturePython)
  n = 0.013
FEATURE [App::DocumentObjectGroupPython] Ca_element010  label="Ca_element : 0.044"  # scripted group (container) (typed FeaturePython)
  n = 0.044
FEATURE [App::DocumentObjectGroupPython] Fe_element002  label="Fe_element : 0.014"  # scripted group (container) (typed FeaturePython)
  n = 0.014
FEATURE [App::DocumentObjectGroupPython] G4_CONCRETE  # scripted group (container) (typed FeaturePython)
  Dunit = g/cm3
  Dvalue = 2.3
  Group = -> [H_element027,C_element030,O_element030,Na_element005,Mg_element003,Al_element002,Si_element002,K_element003,Ca_element010,Fe_element002]
  conduct = 2
  density = 1
  expand = 3
  formula = G4_CONCRETE
  name = G4_CONCRETE
  specific = 4
FEATURE [App::DocumentObjectGroupPython] C_element031  label="C_element : 015"  # scripted group (container) (typed FeaturePython)
  n = 6
  ref = C_element
FEATURE [App::DocumentObjectGroupPython] H_element028  label="H_element : 12"  # scripted group (container) (typed FeaturePython)
  n = 12
  ref = H_element
FEATURE [App::DocumentObjectGroupPython] G4_CYCLOHEXANE  # scripted group (container) (typed FeaturePython)
  Dunit = g/cm3
  Dvalue = 0.779
  Group = -> [C_element031,H_element028]
  conduct = 2
  density = 1
  expand = 3
  formula = G4_CYCLOHEXANE
  name = G4_CYCLOHEXANE
  specific = 4
FEATURE [App::DocumentObjectGroupPython] C_element032  label="C_element : 016"  # scripted group (container) (typed FeaturePython)
  n = 6
  ref = C_element
FEATURE [App::DocumentObjectGroupPython] H_element029  label="H_element : 4"  # scripted group (container) (typed FeaturePython)
  n = 4
  ref = H_element
FEATURE [App::DocumentObjectGroupPython] Cl_element007  label="Cl_element : 2"  # scripted group (container) (typed FeaturePython)
  n = 2
  ref = Cl_element
FEATURE [App::DocumentObjectGroupPython] G4_1_2_DICHLOROBENZENE  label="G4_1.2-DICHLOROBENZENE"  # scripted group (container) (typed FeaturePython)
  Dunit = g/cm3
  Dvalue = 1.3048
  Group = -> [C_element032,H_element029,Cl_element007]
  conduct = 2
  density = 1
  expand = 3
  formula = G4_1.2-DICHLOROBENZENE
  name = G4_1.2-DICHLOROBENZENE
  specific = 4
FEATURE [App::DocumentObjectGroupPython] C_element033  label="C_element : 017"  # scripted group (container) (typed FeaturePython)
  n = 4
  ref = C_element
FEATURE [App::DocumentObjectGroupPython] H_element030  label="H_element : 8"  # scripted group (container) (typed FeaturePython)
  n = 8
  ref = H_element
FEATURE [App::DocumentObjectGroupPython] O_element031  label="O_element : 014"  # scripted group (container) (typed FeaturePython)
  n = 1
  ref = O_element
FEATURE [App::DocumentObjectGroupPython] Cl_element008  label="Cl_element : 005"  # scripted group (container) (typed FeaturePython)
  n = 2
  ref = Cl_element
FEATURE [App::DocumentObjectGroupPython] G4_DICHLORODIETHYL_ETHER  # scripted group (container) (typed FeaturePython)
  Dunit = g/cm3
  Dvalue = 1.2199
  Group = -> [C_element033,H_element030,O_element031,Cl_element008]
  conduct = 2
  density = 1
  expand = 3
  formula = G4_DICHLORODIETHYL_ETHER
  name = G4_DICHLORODIETHYL_ETHER
  specific = 4
FEATURE [App::DocumentObjectGroupPython] C_element034  label="C_element : 018"  # scripted group (container) (typed FeaturePython)
  n = 2
  ref = C_element
FEATURE [App::DocumentObjectGroupPython] H_element031  label="H_element : 014"  # scripted group (container) (typed FeaturePython)
  n = 4
  ref = H_element
FEATURE [App::DocumentObjectGroupPython] Cl_element009  label="Cl_element : 006"  # scripted group (container) (typed FeaturePython)
  n = 2
  ref = Cl_element
FEATURE [App::DocumentObjectGroupPython] G4_1_2_DICHLOROETHANE  label="G4_1.2-DICHLOROETHANE"  # scripted group (container) (typed FeaturePython)
  Dunit = g/cm3
  Dvalue = 1.2351
  Group = -> [C_element034,H_element031,Cl_element009]
  conduct = 2
  density = 1
  expand = 3
  formula = G4_1.2-DICHLOROETHANE
  name = G4_1.2-DICHLOROETHANE
  specific = 4
FEATURE [App::DocumentObjectGroupPython] C_element035  label="C_element : 019"  # scripted group (container) (typed FeaturePython)
  n = 4
  ref = C_element
FEATURE [App::DocumentObjectGroupPython] H_element032  label="H_element : 015"  # scripted group (container) (typed FeaturePython)
  n = 10
  ref = H_element
FEATURE [App::DocumentObjectGroupPython] O_element032  label="O_element : 015"  # scripted group (container) (typed FeaturePython)
  n = 1
  ref = O_element
FEATURE [App::DocumentObjectGroupPython] G4_DIETHYL_ETHER  # scripted group (container) (typed FeaturePython)
  Dunit = g/cm3
  Dvalue = 0.71378
  Group = -> [C_element035,H_element032,O_element032]
  conduct = 2
  density = 1
  expand = 3
  formula = G4_DIETHYL_ETHER
  name = G4_DIETHYL_ETHER
  specific = 4
FEATURE [App::DocumentObjectGroupPython] C_element036  label="C_element : 020"  # scripted group (container) (typed FeaturePython)
  n = 3
  ref = C_element
FEATURE [App::DocumentObjectGroupPython] H_element033  label="H_element : 016"  # scripted group (container) (typed FeaturePython)
  n = 7
  ref = H_element
FEATURE [App::DocumentObjectGroupPython] N_element015  label="N_element : 008"  # scripted group (container) (typed FeaturePython)
  n = 1
  ref = N_element
FEATURE [App::DocumentObjectGroupPython] O_element033  label="O_element : 016"  # scripted group (container) (typed FeaturePython)
  n = 1
  ref = O_element
FEATURE [App::DocumentObjectGroupPython] G4_N_N_DIMETHYL_FORMAMIDE  label="G4_N.N-DIMETHYL_FORMAMIDE"  # scripted group (container) (typed FeaturePython)
  Dunit = g/cm3
  Dvalue = 0.9487
  Group = -> [C_element036,H_element033,N_element015,O_element033]
  conduct = 2
  density = 1
  expand = 3
  formula = G4_N.N-DIMETHYL_FORMAMIDE
  name = G4_N.N-DIMETHYL_FORMAMIDE
  specific = 4
FEATURE [App::DocumentObjectGroupPython] C_element037  label="C_element : 021"  # scripted group (container) (typed FeaturePython)
  n = 2
  ref = C_element
FEATURE [App::DocumentObjectGroupPython] H_element034  label="H_element : 017"  # scripted group (container) (typed FeaturePython)
  n = 6
  ref = H_element
FEATURE [App::DocumentObjectGroupPython] O_element034  label="O_element : 017"  # scripted group (container) (typed FeaturePython)
  n = 1
  ref = O_element
FEATURE [App::DocumentObjectGroupPython] S_element009  label="S_element : 003"  # scripted group (container) (typed FeaturePython)
  n = 1
  ref = S_element
FEATURE [App::DocumentObjectGroupPython] G4_DIMETHYL_SULFOXIDE  # scripted group (container) (typed FeaturePython)
  Dunit = g/cm3
  Dvalue = 1.1014
  Group = -> [C_element037,H_element034,O_element034,S_element009]
  conduct = 2
  density = 1
  expand = 3
  formula = G4_DIMETHYL_SULFOXIDE
  name = G4_DIMETHYL_SULFOXIDE
  specific = 4
FEATURE [App::DocumentObjectGroupPython] C_element038  label="C_element : 022"  # scripted group (container) (typed FeaturePython)
  n = 2
  ref = C_element
FEATURE [App::DocumentObjectGroupPython] H_element035  label="H_element : 018"  # scripted group (container) (typed FeaturePython)
  n = 6
  ref = H_element
FEATURE [App::DocumentObjectGroupPython] G4_ETHANE  # scripted group (container) (typed FeaturePython)
  Dunit = g/cm3
  Dvalue = 0.00125324
  Group = -> [C_element038,H_element035]
  conduct = 2
  density = 1
  expand = 3
  formula = G4_ETHANE
  name = G4_ETHANE
  specific = 4
FEATURE [App::DocumentObjectGroupPython] C_element039  label="C_element : 023"  # scripted group (container) (typed FeaturePython)
  n = 2
  ref = C_element
FEATURE [App::DocumentObjectGroupPython] H_element036  label="H_element : 019"  # scripted group (container) (typed FeaturePython)
  n = 6
  ref = H_element
FEATURE [App::DocumentObjectGroupPython] O_element035  label="O_element : 018"  # scripted group (container) (typed FeaturePython)
  n = 1
  ref = O_element
FEATURE [App::DocumentObjectGroupPython] G4_ETHYL_ALCOHOL  # scripted group (container) (typed FeaturePython)
  Dunit = g/cm3
  Dvalue = 0.7893
  Group = -> [C_element039,H_element036,O_element035]
  conduct = 2
  density = 1
  expand = 3
  formula = G4_ETHYL_ALCOHOL
  name = G4_ETHYL_ALCOHOL
  specific = 4
FEATURE [App::DocumentObjectGroupPython] H_element037  label="H_element : 0.090"  # scripted group (container) (typed FeaturePython)
  n = 0.090027
FEATURE [App::DocumentObjectGroupPython] C_element040  label="C_element : 0.585"  # scripted group (container) (typed FeaturePython)
  n = 0.585182
FEATURE [App::DocumentObjectGroupPython] O_element036  label="O_element : 0.325"  # scripted group (container) (typed FeaturePython)
  n = 0.324791
FEATURE [App::DocumentObjectGroupPython] G4_ETHYL_CELLULOSE  # scripted group (container) (typed FeaturePython)
  Dunit = g/cm3
  Dvalue = 1.13
  Group = -> [H_element037,C_element040,O_element036]
  conduct = 2
  density = 1
  expand = 3
  formula = G4_ETHYL_CELLULOSE
  name = G4_ETHYL_CELLULOSE
  specific = 4
FEATURE [App::DocumentObjectGroupPython] C_element041  label="C_element : 024"  # scripted group (container) (typed FeaturePython)
  n = 2
  ref = C_element
FEATURE [App::DocumentObjectGroupPython] H_element038  label="H_element : 020"  # scripted group (container) (typed FeaturePython)
  n = 4
  ref = H_element
FEATURE [App::DocumentObjectGroupPython] G4_ETHYLENE  # scripted group (container) (typed FeaturePython)
  Dunit = g/cm3
  Dvalue = 0.00117497
  Group = -> [C_element041,H_element038]
  conduct = 2
  density = 1
  expand = 3
  formula = G4_ETHYLENE
  name = G4_ETHYLENE
  specific = 4
FEATURE [App::DocumentObjectGroupPython] H_element039  label="H_element : 0.096"  # scripted group (container) (typed FeaturePython)
  n = 0.096
FEATURE [App::DocumentObjectGroupPython] C_element042  label="C_element : 0.195"  # scripted group (container) (typed FeaturePython)
  n = 0.195
FEATURE [App::DocumentObjectGroupPython] N_element016  label="N_element : 0.057"  # scripted group (container) (typed FeaturePython)
  n = 0.057
FEATURE [App::DocumentObjectGroupPython] O_element037  label="O_element : 0.646"  # scripted group (container) (typed FeaturePython)
  n = 0.646
FEATURE [App::DocumentObjectGroupPython] Na_element006  label="Na_element : 0.017"  # scripted group (container) (typed FeaturePython)
  n = 0.001
FEATURE [App::DocumentObjectGroupPython] P_element005  label="P_element : 0.104"  # scripted group (container) (typed FeaturePython)
  n = 0.001
FEATURE [App::DocumentObjectGroupPython] S_element010  label="S_element : 0.016"  # scripted group (container) (typed FeaturePython)
  n = 0.003
FEATURE [App::DocumentObjectGroupPython] Cl_element010  label="Cl_element : 0.005"  # scripted group (container) (typed FeaturePython)
  n = 0.001
FEATURE [App::DocumentObjectGroupPython] G4_EYE_LENS_ICRP  # scripted group (container) (typed FeaturePython)
  Dunit = g/cm3
  Dvalue = 1.07
  Group = -> [H_element039,C_element042,N_element016,O_element037,Na_element006,P_element005,S_element010,Cl_element010]
  conduct = 2
  density = 1
  expand = 3
  formula = G4_EYE_LENS_ICRP
  name = G4_EYE_LENS_ICRP
  specific = 4
FEATURE [App::DocumentObjectGroupPython] Fe_element003  label="Fe_element : 2"  # scripted group (container) (typed FeaturePython)
  n = 2
  ref = Fe_element
FEATURE [App::DocumentObjectGroupPython] O_element038  label="O_element : 019"  # scripted group (container) (typed FeaturePython)
  n = 3
  ref = O_element
FEATURE [App::DocumentObjectGroupPython] G4_FERRIC_OXIDE  # scripted group (container) (typed FeaturePython)
  Dunit = g/cm3
  Dvalue = 5.2
  Group = -> [Fe_element003,O_element038]
  conduct = 2
  density = 1
  expand = 3
  formula = G4_FERRIC_OXIDE
  name = G4_FERRIC_OXIDE
  specific = 4
FEATURE [App::DocumentObjectGroupPython] Fe_element004  label="Fe_element : 1"  # scripted group (container) (typed FeaturePython)
  n = 1
  ref = Fe_element
FEATURE [App::DocumentObjectGroupPython] B_element003  label="B_element : 1"  # scripted group (container) (typed FeaturePython)
  n = 1
  ref = B_element
FEATURE [App::DocumentObjectGroupPython] G4_FERROBORIDE  # scripted group (container) (typed FeaturePython)
  Dunit = g/cm3
  Dvalue = 7.15
  Group = -> [Fe_element004,B_element003]
  conduct = 2
  density = 1
  expand = 3
  formula = G4_FERROBORIDE
  name = G4_FERROBORIDE
  specific = 4
FEATURE [App::DocumentObjectGroupPython] Fe_element005  label="Fe_element : 003"  # scripted group (container) (typed FeaturePython)
  n = 1
  ref = Fe_element
FEATURE [App::DocumentObjectGroupPython] O_element039  label="O_element : 020"  # scripted group (container) (typed FeaturePython)
  n = 1
  ref = O_element
FEATURE [App::DocumentObjectGroupPython] G4_FERROUS_OXIDE  # scripted group (container) (typed FeaturePython)
  Dunit = g/cm3
  Dvalue = 5.7
  Group = -> [Fe_element005,O_element039]
  conduct = 2
  density = 1
  expand = 3
  formula = G4_FERROUS_OXIDE
  name = G4_FERROUS_OXIDE
  specific = 4
FEATURE [App::DocumentObjectGroupPython] H_element040  label="H_element : 0.115"  # scripted group (container) (typed FeaturePython)
  n = 0.108259
FEATURE [App::DocumentObjectGroupPython] N_element017  label="N_element : 0.000"  # scripted group (container) (typed FeaturePython)
  n = 2.7e-05
FEATURE [App::DocumentObjectGroupPython] O_element040  label="O_element : 0.879"  # scripted group (container) (typed FeaturePython)
  n = 0.878636
FEATURE [App::DocumentObjectGroupPython] Na_element007  label="Na_element : 0.000"  # scripted group (container) (typed FeaturePython)
  n = 2.2e-05
FEATURE [App::DocumentObjectGroupPython] S_element011  label="S_element : 0.013"  # scripted group (container) (typed FeaturePython)
  n = 0.012968
FEATURE [App::DocumentObjectGroupPython] Cl_element011  label="Cl_element : 0.000"  # scripted group (container) (typed FeaturePython)
  n = 3.4e-05
FEATURE [App::DocumentObjectGroupPython] Fe_element006  label="Fe_element : 0.000"  # scripted group (container) (typed FeaturePython)
  n = 5.4e-05
FEATURE [App::DocumentObjectGroupPython] G4_FERROUS_SULFATE  # scripted group (container) (typed FeaturePython)
  Dunit = g/cm3
  Dvalue = 1.024
  Group = -> [H_element040,N_element017,O_element040,Na_element007,S_element011,Cl_element011,Fe_element006]
  conduct = 2
  density = 1
  expand = 3
  formula = G4_FERROUS_SULFATE
  name = G4_FERROUS_SULFATE
  specific = 4
FEATURE [App::DocumentObjectGroupPython] C_element043  label="C_element : 0.099"  # scripted group (container) (typed FeaturePython)
  n = 0.099335
FEATURE [App::DocumentObjectGroupPython] F_element007  label="F_element : 0.314"  # scripted group (container) (typed FeaturePython)
  n = 0.314247
FEATURE [App::DocumentObjectGroupPython] Cl_element012  label="Cl_element : 0.586"  # scripted group (container) (typed FeaturePython)
  n = 0.586418
FEATURE [App::DocumentObjectGroupPython] G4_FREON_12  label="G4_FREON-12"  # scripted group (container) (typed FeaturePython)
  Dunit = g/cm3
  Dvalue = 1.12
  Group = -> [C_element043,F_element007,Cl_element012]
  conduct = 2
  density = 1
  expand = 3
  formula = G4_FREON-12
  name = G4_FREON-12
  specific = 4
FEATURE [App::DocumentObjectGroupPython] C_element044  label="C_element : 0.057"  # scripted group (container) (typed FeaturePython)
  n = 0.057245
FEATURE [App::DocumentObjectGroupPython] F_element008  label="F_element : 0.181"  # scripted group (container) (typed FeaturePython)
  n = 0.181096
FEATURE [App::DocumentObjectGroupPython] Br_element001  label="Br_element : 0.762"  # scripted group (container) (typed FeaturePython)
  n = 0.761659
FEATURE [App::DocumentObjectGroupPython] G4_FREON_12B2  label="G4_FREON-12B2"  # scripted group (container) (typed FeaturePython)
  Dunit = g/cm3
  Dvalue = 1.8
  Group = -> [C_element044,F_element008,Br_element001]
  conduct = 2
  density = 1
  expand = 3
  formula = G4_FREON-12B2
  name = G4_FREON-12B2
  specific = 4
FEATURE [App::DocumentObjectGroupPython] C_element045  label="C_element : 0.115"  # scripted group (container) (typed FeaturePython)
  n = 0.114983
FEATURE [App::DocumentObjectGroupPython] F_element009  label="F_element : 0.546"  # scripted group (container) (typed FeaturePython)
  n = 0.545621
FEATURE [App::DocumentObjectGroupPython] Cl_element013  label="Cl_element : 0.339"  # scripted group (container) (typed FeaturePython)
  n = 0.339396
FEATURE [App::DocumentObjectGroupPython] G4_FREON_13  label="G4_FREON-13"  # scripted group (container) (typed FeaturePython)
  Dunit = g/cm3
  Dvalue = 0.95
  Group = -> [C_element045,F_element009,Cl_element013]
  conduct = 2
  density = 1
  expand = 3
  formula = G4_FREON-13
  name = G4_FREON-13
  specific = 4
FEATURE [App::DocumentObjectGroupPython] C_element046  label="C_element : 025"  # scripted group (container) (typed FeaturePython)
  n = 1
  ref = C_element
FEATURE [App::DocumentObjectGroupPython] F_element010  label="F_element : 3"  # scripted group (container) (typed FeaturePython)
  n = 3
  ref = F_element
FEATURE [App::DocumentObjectGroupPython] Br_element002  label="Br_element : 1"  # scripted group (container) (typed FeaturePython)
  n = 1
  ref = Br_element
FEATURE [App::DocumentObjectGroupPython] G4_FREON_13B1  label="G4_FREON-13B1"  # scripted group (container) (typed FeaturePython)
  Dunit = g/cm3
  Dvalue = 1.5
  Group = -> [C_element046,F_element010,Br_element002]
  conduct = 2
  density = 1
  expand = 3
  formula = G4_FREON-13B1
  name = G4_FREON-13B1
  specific = 4
FEATURE [App::DocumentObjectGroupPython] C_element047  label="C_element : 0.061"  # scripted group (container) (typed FeaturePython)
  n = 0.061309
FEATURE [App::DocumentObjectGroupPython] F_element011  label="F_element : 0.291"  # scripted group (container) (typed FeaturePython)
  n = 0.290924
FEATURE [App::DocumentObjectGroupPython] I_element002  label="I_element : 0.648"  # scripted group (container) (typed FeaturePython)
  n = 0.647767
FEATURE [App::DocumentObjectGroupPython] G4_FREON_13I1  label="G4_FREON-13I1"  # scripted group (container) (typed FeaturePython)
  Dunit = g/cm3
  Dvalue = 1.8
  Group = -> [C_element047,F_element011,I_element002]
  conduct = 2
  density = 1
  expand = 3
  formula = G4_FREON-13I1
  name = G4_FREON-13I1
  specific = 4
FEATURE [App::DocumentObjectGroupPython] Gd_element001  label="Gd_element : 2"  # scripted group (container) (typed FeaturePython)
  n = 2
  ref = Gd_element
FEATURE [App::DocumentObjectGroupPython] O_element041  label="O_element : 021"  # scripted group (container) (typed FeaturePython)
  n = 2
  ref = O_element
FEATURE [App::DocumentObjectGroupPython] S_element012  label="S_element : 004"  # scripted group (container) (typed FeaturePython)
  n = 1
  ref = S_element
FEATURE [App::DocumentObjectGroupPython] G4_GADOLINIUM_OXYSULFIDE  # scripted group (container) (typed FeaturePython)
  Dunit = g/cm3
  Dvalue = 7.44
  Group = -> [Gd_element001,O_element041,S_element012]
  conduct = 2
  density = 1
  expand = 3
  formula = G4_GADOLINIUM_OXYSULFIDE
  name = G4_GADOLINIUM_OXYSULFIDE
  specific = 4
FEATURE [App::DocumentObjectGroupPython] Ga_element001  label="Ga_element : 1"  # scripted group (container) (typed FeaturePython)
  n = 1
  ref = Ga_element
FEATURE [App::DocumentObjectGroupPython] As_element001  label="As_element : 1"  # scripted group (container) (typed FeaturePython)
  n = 1
  ref = As_element
FEATURE [App::DocumentObjectGroupPython] G4_GALLIUM_ARSENIDE  # scripted group (container) (typed FeaturePython)
  Dunit = g/cm3
  Dvalue = 5.31
  Group = -> [Ga_element001,As_element001]
  conduct = 2
  density = 1
  expand = 3
  formula = G4_GALLIUM_ARSENIDE
  name = G4_GALLIUM_ARSENIDE
  specific = 4
FEATURE [App::DocumentObjectGroupPython] H_element041  label="H_element : 0.081"  # scripted group (container) (typed FeaturePython)
  n = 0.08118
FEATURE [App::DocumentObjectGroupPython] C_element048  label="C_element : 0.416"  # scripted group (container) (typed FeaturePython)
  n = 0.41606
FEATURE [App::DocumentObjectGroupPython] N_element018  label="N_element : 0.111"  # scripted group (container) (typed FeaturePython)
  n = 0.11124
FEATURE [App::DocumentObjectGroupPython] O_element042  label="O_element : 0.381"  # scripted group (container) (typed FeaturePython)
  n = 0.38064
FEATURE [App::DocumentObjectGroupPython] S_element013  label="S_element : 0.011"  # scripted group (container) (typed FeaturePython)
  n = 0.01088
FEATURE [App::DocumentObjectGroupPython] G4_GEL_PHOTO_EMULSION  # scripted group (container) (typed FeaturePython)
  Dunit = g/cm3
  Dvalue = 1.2914
  Group = -> [H_element041,C_element048,N_element018,O_element042,S_element013]
  conduct = 2
  density = 1
  expand = 3
  formula = G4_GEL_PHOTO_EMULSION
  name = G4_GEL_PHOTO_EMULSION
  specific = 4
FEATURE [App::DocumentObjectGroupPython] B_element004  label="B_element : 0.040"  # scripted group (container) (typed FeaturePython)
  n = 0.0400639
FEATURE [App::DocumentObjectGroupPython] O_element043  label="O_element : 0.540"  # scripted group (container) (typed FeaturePython)
  n = 0.539561
FEATURE [App::DocumentObjectGroupPython] Na_element008  label="Na_element : 0.028"  # scripted group (container) (typed FeaturePython)
  n = 0.0281909
FEATURE [App::DocumentObjectGroupPython] Al_element003  label="Al_element : 0.012"  # scripted group (container) (typed FeaturePython)
  n = 0.011644
FEATURE [App::DocumentObjectGroupPython] Si_element003  label="Si_element : 0.377"  # scripted group (container) (typed FeaturePython)
  n = 0.377219
FEATURE [App::DocumentObjectGroupPython] K_element004  label="K_element : 0.014"  # scripted group (container) (typed FeaturePython)
  n = 0.00332099
FEATURE [App::DocumentObjectGroupPython] G4_Pyrex_Glass  # scripted group (container) (typed FeaturePython)
  Dunit = g/cm3
  Dvalue = 2.23
  Group = -> [B_element004,O_element043,Na_element008,Al_element003,Si_element003,K_element004]
  conduct = 2
  density = 1
  expand = 3
  formula = G4_Pyrex_Glass
  name = G4_Pyrex_Glass
  specific = 4
FEATURE [App::DocumentObjectGroupPython] O_element044  label="O_element : 0.156"  # scripted group (container) (typed FeaturePython)
  n = 0.156453
FEATURE [App::DocumentObjectGroupPython] Si_element004  label="Si_element : 0.081"  # scripted group (container) (typed FeaturePython)
  n = 0.080866
FEATURE [App::DocumentObjectGroupPython] Ti_element001  label="Ti_element : 0.008"  # scripted group (container) (typed FeaturePython)
  n = 0.008092
FEATURE [App::DocumentObjectGroupPython] As_element002  label="As_element : 0.003"  # scripted group (container) (typed FeaturePython)
  n = 0.002651
FEATURE [App::DocumentObjectGroupPython] Pb_element001  label="Pb_element : 0.752"  # scripted group (container) (typed FeaturePython)
  n = 0.751938
FEATURE [App::DocumentObjectGroupPython] G4_GLASS_LEAD  # scripted group (container) (typed FeaturePython)
  Dunit = g/cm3
  Dvalue = 6.22
  Group = -> [O_element044,Si_element004,Ti_element001,As_element002,Pb_element001]
  conduct = 2
  density = 1
  expand = 3
  formula = G4_GLASS_LEAD
  name = G4_GLASS_LEAD
  specific = 4
FEATURE [App::DocumentObjectGroupPython] O_element045  label="O_element : 0.460"  # scripted group (container) (typed FeaturePython)
  n = 0.4598
FEATURE [App::DocumentObjectGroupPython] Na_element009  label="Na_element : 0.096"  # scripted group (container) (typed FeaturePython)
  n = 0.0964411
FEATURE [App::DocumentObjectGroupPython] Si_element005  label="Si_element : 0.378"  # scripted group (container) (typed FeaturePython)
  n = 0.336553
FEATURE [App::DocumentObjectGroupPython] Ca_element011  label="Ca_element : 0.107"  # scripted group (container) (typed FeaturePython)
  n = 0.107205
FEATURE [App::DocumentObjectGroupPython] G4_GLASS_PLATE  # scripted group (container) (typed FeaturePython)
  Dunit = g/cm3
  Dvalue = 2.4
  Group = -> [O_element045,Na_element009,Si_element005,Ca_element011]
  conduct = 2
  density = 1
  expand = 3
  formula = G4_GLASS_PLATE
  name = G4_GLASS_PLATE
  specific = 4
FEATURE [App::DocumentObjectGroupPython] C_element049  label="C_element : 026"  # scripted group (container) (typed FeaturePython)
  n = 5
  ref = C_element
FEATURE [App::DocumentObjectGroupPython] H_element042  label="H_element : 021"  # scripted group (container) (typed FeaturePython)
  n = 10
  ref = H_element
FEATURE [App::DocumentObjectGroupPython] N_element019  label="N_element : 2"  # scripted group (container) (typed FeaturePython)
  n = 2
  ref = N_element
FEATURE [App::DocumentObjectGroupPython] O_element046  label="O_element : 022"  # scripted group (container) (typed FeaturePython)
  n = 3
  ref = O_element
FEATURE [App::DocumentObjectGroupPython] G4_GLUTAMINE  # scripted group (container) (typed FeaturePython)
  Dunit = g/cm3
  Dvalue = 1.46
  Group = -> [C_element049,H_element042,N_element019,O_element046]
  conduct = 2
  density = 1
  expand = 3
  formula = G4_GLUTAMINE
  name = G4_GLUTAMINE
  specific = 4
FEATURE [App::DocumentObjectGroupPython] C_element050  label="C_element : 027"  # scripted group (container) (typed FeaturePython)
  n = 3
  ref = C_element
FEATURE [App::DocumentObjectGroupPython] H_element043  label="H_element : 022"  # scripted group (container) (typed FeaturePython)
  n = 8
  ref = H_element
FEATURE [App::DocumentObjectGroupPython] O_element047  label="O_element : 023"  # scripted group (container) (typed FeaturePython)
  n = 3
  ref = O_element
FEATURE [App::DocumentObjectGroupPython] G4_GLYCEROL  # scripted group (container) (typed FeaturePython)
  Dunit = g/cm3
  Dvalue = 1.2613
  Group = -> [C_element050,H_element043,O_element047]
  conduct = 2
  density = 1
  expand = 3
  formula = G4_GLYCEROL
  name = G4_GLYCEROL
  specific = 4
FEATURE [App::DocumentObjectGroupPython] C_element051  label="C_element : 028"  # scripted group (container) (typed FeaturePython)
  n = 5
  ref = C_element
FEATURE [App::DocumentObjectGroupPython] H_element044  label="H_element : 023"  # scripted group (container) (typed FeaturePython)
  n = 5
  ref = H_element
FEATURE [App::DocumentObjectGroupPython] N_element020  label="N_element : 009"  # scripted group (container) (typed FeaturePython)
  n = 5
  ref = N_element
FEATURE [App::DocumentObjectGroupPython] O_element048  label="O_element : 024"  # scripted group (container) (typed FeaturePython)
  n = 1
  ref = O_element
FEATURE [App::DocumentObjectGroupPython] G4_GUANINE  # scripted group (container) (typed FeaturePython)
  Dunit = g/cm3
  Dvalue = 2.2
  Group = -> [C_element051,H_element044,N_element020,O_element048]
  conduct = 2
  density = 1
  expand = 3
  formula = G4_GUANINE
  name = G4_GUANINE
  specific = 4
FEATURE [App::DocumentObjectGroupPython] Ca_element012  label="Ca_element : 006"  # scripted group (container) (typed FeaturePython)
  n = 1
  ref = Ca_element
FEATURE [App::DocumentObjectGroupPython] S_element014  label="S_element : 005"  # scripted group (container) (typed FeaturePython)
  n = 1
  ref = S_element
FEATURE [App::DocumentObjectGroupPython] O_element049  label="O_element : 6"  # scripted group (container) (typed FeaturePython)
  n = 6
  ref = O_element
FEATURE [App::DocumentObjectGroupPython] H_element045  label="H_element : 024"  # scripted group (container) (typed FeaturePython)
  n = 4
  ref = H_element
FEATURE [App::DocumentObjectGroupPython] G4_GYPSUM  # scripted group (container) (typed FeaturePython)
  Dunit = g/cm3
  Dvalue = 2.32
  Group = -> [Ca_element012,S_element014,O_element049,H_element045]
  conduct = 2
  density = 1
  expand = 3
  formula = G4_GYPSUM
  name = G4_GYPSUM
  specific = 4
FEATURE [App::DocumentObjectGroupPython] C_element052  label="C_element : 7"  # scripted group (container) (typed FeaturePython)
  n = 7
  ref = C_element
FEATURE [App::DocumentObjectGroupPython] H_element046  label="H_element : 16"  # scripted group (container) (typed FeaturePython)
  n = 16
  ref = H_element
FEATURE [App::DocumentObjectGroupPython] G4_N_HEPTANE  label="G4_N-HEPTANE"  # scripted group (container) (typed FeaturePython)
  Dunit = g/cm3
  Dvalue = 0.68376
  Group = -> [C_element052,H_element046]
  conduct = 2
  density = 1
  expand = 3
  formula = G4_N-HEPTANE
  name = G4_N-HEPTANE
  specific = 4
FEATURE [App::DocumentObjectGroupPython] C_element053  label="C_element : 029"  # scripted group (container) (typed FeaturePython)
  n = 6
  ref = C_element
FEATURE [App::DocumentObjectGroupPython] H_element047  label="H_element : 14"  # scripted group (container) (typed FeaturePython)
  n = 14
  ref = H_element
FEATURE [App::DocumentObjectGroupPython] G4_N_HEXANE  label="G4_N-HEXANE"  # scripted group (container) (typed FeaturePython)
  Dunit = g/cm3
  Dvalue = 0.6603
  Group = -> [C_element053,H_element047]
  conduct = 2
  density = 1
  expand = 3
  formula = G4_N-HEXANE
  name = G4_N-HEXANE
  specific = 4
FEATURE [App::DocumentObjectGroupPython] C_element054  label="C_element : 22"  # scripted group (container) (typed FeaturePython)
  n = 22
  ref = C_element
FEATURE [App::DocumentObjectGroupPython] H_element048  label="H_element : 025"  # scripted group (container) (typed FeaturePython)
  n = 10
  ref = H_element
FEATURE [App::DocumentObjectGroupPython] N_element021  label="N_element : 010"  # scripted group (container) (typed FeaturePython)
  n = 2
  ref = N_element
FEATURE [App::DocumentObjectGroupPython] O_element050  label="O_element : 025"  # scripted group (container) (typed FeaturePython)
  n = 5
  ref = O_element
FEATURE [App::DocumentObjectGroupPython] G4_KAPTON  # scripted group (container) (typed FeaturePython)
  Dunit = g/cm3
  Dvalue = 1.42
  Group = -> [C_element054,H_element048,N_element021,O_element050]
  conduct = 2
  density = 1
  expand = 3
  formula = G4_KAPTON
  name = G4_KAPTON
  specific = 4
FEATURE [App::DocumentObjectGroupPython] La_element001  label="La_element : 1"  # scripted group (container) (typed FeaturePython)
  n = 1
  ref = La_element
FEATURE [App::DocumentObjectGroupPython] Br_element003  label="Br_element : 002"  # scripted group (container) (typed FeaturePython)
  n = 1
  ref = Br_element
FEATURE [App::DocumentObjectGroupPython] O_element051  label="O_element : 026"  # scripted group (container) (typed FeaturePython)
  n = 1
  ref = O_element
FEATURE [App::DocumentObjectGroupPython] G4_LANTHANUM_OXYBROMIDE  # scripted group (container) (typed FeaturePython)
  Dunit = g/cm3
  Dvalue = 6.28
  Group = -> [La_element001,Br_element003,O_element051]
  conduct = 2
  density = 1
  expand = 3
  formula = G4_LANTHANUM_OXYBROMIDE
  name = G4_LANTHANUM_OXYBROMIDE
  specific = 4
FEATURE [App::DocumentObjectGroupPython] La_element002  label="La_element : 2"  # scripted group (container) (typed FeaturePython)
  n = 2
  ref = La_element
FEATURE [App::DocumentObjectGroupPython] O_element052  label="O_element : 027"  # scripted group (container) (typed FeaturePython)
  n = 2
  ref = O_element
FEATURE [App::DocumentObjectGroupPython] S_element015  label="S_element : 006"  # scripted group (container) (typed FeaturePython)
  n = 1
  ref = S_element
FEATURE [App::DocumentObjectGroupPython] G4_LANTHANUM_OXYSULFIDE  # scripted group (container) (typed FeaturePython)
  Dunit = g/cm3
  Dvalue = 5.86
  Group = -> [La_element002,O_element052,S_element015]
  conduct = 2
  density = 1
  expand = 3
  formula = G4_LANTHANUM_OXYSULFIDE
  name = G4_LANTHANUM_OXYSULFIDE
  specific = 4
FEATURE [App::DocumentObjectGroupPython] O_element053  label="O_element : 0.072"  # scripted group (container) (typed FeaturePython)
  n = 0.071682
FEATURE [App::DocumentObjectGroupPython] Pb_element002  label="Pb_element : 0.928"  # scripted group (container) (typed FeaturePython)
  n = 0.928318
FEATURE [App::DocumentObjectGroupPython] G4_LEAD_OXIDE  # scripted group (container) (typed FeaturePython)
  Dunit = g/cm3
  Dvalue = 9.53
  Group = -> [O_element053,Pb_element002]
  conduct = 2
  density = 1
  expand = 3
  formula = G4_LEAD_OXIDE
  name = G4_LEAD_OXIDE
  specific = 4
FEATURE [App::DocumentObjectGroupPython] Li_element001  label="Li_element : 1"  # scripted group (container) (typed FeaturePython)
  n = 1
  ref = Li_element
FEATURE [App::DocumentObjectGroupPython] N_element022  label="N_element : 011"  # scripted group (container) (typed FeaturePython)
  n = 1
  ref = N_element
FEATURE [App::DocumentObjectGroupPython] H_element049  label="H_element : 026"  # scripted group (container) (typed FeaturePython)
  n = 2
  ref = H_element
FEATURE [App::DocumentObjectGroupPython] G4_LITHIUM_AMIDE  # scripted group (container) (typed FeaturePython)
  Dunit = g/cm3
  Dvalue = 1.178
  Group = -> [Li_element001,N_element022,H_element049]
  conduct = 2
  density = 1
  expand = 3
  formula = G4_LITHIUM_AMIDE
  name = G4_LITHIUM_AMIDE
  specific = 4
FEATURE [App::DocumentObjectGroupPython] Li_element002  label="Li_element : 2"  # scripted group (container) (typed FeaturePython)
  n = 2
  ref = Li_element
FEATURE [App::DocumentObjectGroupPython] C_element055  label="C_element : 030"  # scripted group (container) (typed FeaturePython)
  n = 1
  ref = C_element
FEATURE [App::DocumentObjectGroupPython] O_element054  label="O_element : 028"  # scripted group (container) (typed FeaturePython)
  n = 3
  ref = O_element
FEATURE [App::DocumentObjectGroupPython] G4_LITHIUM_CARBONATE  # scripted group (container) (typed FeaturePython)
  Dunit = g/cm3
  Dvalue = 2.11
  Group = -> [Li_element002,C_element055,O_element054]
  conduct = 2
  density = 1
  expand = 3
  formula = G4_LITHIUM_CARBONATE
  name = G4_LITHIUM_CARBONATE
  specific = 4
FEATURE [App::DocumentObjectGroupPython] Li_element003  label="Li_element : 003"  # scripted group (container) (typed FeaturePython)
  n = 1
  ref = Li_element
FEATURE [App::DocumentObjectGroupPython] F_element012  label="F_element : 004"  # scripted group (container) (typed FeaturePython)
  n = 1
  ref = F_element
FEATURE [App::DocumentObjectGroupPython] G4_LITHIUM_FLUORIDE  # scripted group (container) (typed FeaturePython)
  Dunit = g/cm3
  Dvalue = 2.635
  Group = -> [Li_element003,F_element012]
  conduct = 2
  density = 1
  expand = 3
  formula = G4_LITHIUM_FLUORIDE
  name = G4_LITHIUM_FLUORIDE
  specific = 4
FEATURE [App::DocumentObjectGroupPython] Li_element004  label="Li_element : 004"  # scripted group (container) (typed FeaturePython)
  n = 1
  ref = Li_element
FEATURE [App::DocumentObjectGroupPython] H_element050  label="H_element : 027"  # scripted group (container) (typed FeaturePython)
  n = 1
  ref = H_element
FEATURE [App::DocumentObjectGroupPython] G4_LITHIUM_HYDRIDE  # scripted group (container) (typed FeaturePython)
  Dunit = g/cm3
  Dvalue = 0.82
  Group = -> [Li_element004,H_element050]
  conduct = 2
  density = 1
  expand = 3
  formula = G4_LITHIUM_HYDRIDE
  name = G4_LITHIUM_HYDRIDE
  specific = 4
FEATURE [App::DocumentObjectGroupPython] Li_element005  label="Li_element : 005"  # scripted group (container) (typed FeaturePython)
  n = 1
  ref = Li_element
FEATURE [App::DocumentObjectGroupPython] I_element003  label="I_element : 002"  # scripted group (container) (typed FeaturePython)
  n = 1
  ref = I_element
FEATURE [App::DocumentObjectGroupPython] G4_LITHIUM_IODIDE  # scripted group (container) (typed FeaturePython)
  Dunit = g/cm3
  Dvalue = 3.494
  Group = -> [Li_element005,I_element003]
  conduct = 2
  density = 1
  expand = 3
  formula = G4_LITHIUM_IODIDE
  name = G4_LITHIUM_IODIDE
  specific = 4
FEATURE [App::DocumentObjectGroupPython] Li_element006  label="Li_element : 006"  # scripted group (container) (typed FeaturePython)
  n = 2
  ref = Li_element
FEATURE [App::DocumentObjectGroupPython] O_element055  label="O_element : 029"  # scripted group (container) (typed FeaturePython)
  n = 1
  ref = O_element
FEATURE [App::DocumentObjectGroupPython] G4_LITHIUM_OXIDE  # scripted group (container) (typed FeaturePython)
  Dunit = g/cm3
  Dvalue = 2.013
  Group = -> [Li_element006,O_element055]
  conduct = 2
  density = 1
  expand = 3
  formula = G4_LITHIUM_OXIDE
  name = G4_LITHIUM_OXIDE
  specific = 4
FEATURE [App::DocumentObjectGroupPython] Li_element007  label="Li_element : 007"  # scripted group (container) (typed FeaturePython)
  n = 2
  ref = Li_element
FEATURE [App::DocumentObjectGroupPython] B_element005  label="B_element : 005"  # scripted group (container) (typed FeaturePython)
  n = 4
  ref = B_element
FEATURE [App::DocumentObjectGroupPython] O_element056  label="O_element : 7"  # scripted group (container) (typed FeaturePython)
  n = 7
  ref = O_element
FEATURE [App::DocumentObjectGroupPython] G4_LITHIUM_TETRABORATE  # scripted group (container) (typed FeaturePython)
  Dunit = g/cm3
  Dvalue = 2.44
  Group = -> [Li_element007,B_element005,O_element056]
  conduct = 2
  density = 1
  expand = 3
  formula = G4_LITHIUM_TETRABORATE
  name = G4_LITHIUM_TETRABORATE
  specific = 4
FEATURE [App::DocumentObjectGroupPython] H_element051  label="H_element : 0.105"  # scripted group (container) (typed FeaturePython)
  n = 0.105
FEATURE [App::DocumentObjectGroupPython] C_element056  label="C_element : 0.083"  # scripted group (container) (typed FeaturePython)
  n = 0.083
FEATURE [App::DocumentObjectGroupPython] N_element023  label="N_element : 0.023"  # scripted group (container) (typed FeaturePython)
  n = 0.023
FEATURE [App::DocumentObjectGroupPython] O_element057  label="O_element : 0.779"  # scripted group (container) (typed FeaturePython)
  n = 0.779
FEATURE [App::DocumentObjectGroupPython] Na_element010  label="Na_element : 0.097"  # scripted group (container) (typed FeaturePython)
  n = 0.002
FEATURE [App::DocumentObjectGroupPython] P_element006  label="P_element : 0.105"  # scripted group (container) (typed FeaturePython)
  n = 0.001
FEATURE [App::DocumentObjectGroupPython] S_element016  label="S_element : 0.017"  # scripted group (container) (typed FeaturePython)
  n = 0.002
FEATURE [App::DocumentObjectGroupPython] Cl_element014  label="Cl_element : 0.587"  # scripted group (container) (typed FeaturePython)
  n = 0.003
FEATURE [App::DocumentObjectGroupPython] K_element005  label="K_element : 0.015"  # scripted group (container) (typed FeaturePython)
  n = 0.002
FEATURE [App::DocumentObjectGroupPython] G4_LUNG_ICRP  # scripted group (container) (typed FeaturePython)
  Dunit = g/cm3
  Dvalue = 1.04
  Group = -> [H_element051,C_element056,N_element023,O_element057,Na_element010,P_element006,S_element016,Cl_element014,K_element005]
  conduct = 2
  density = 1
  expand = 3
  formula = G4_LUNG_ICRP
  name = G4_LUNG_ICRP
  specific = 4
FEATURE [App::DocumentObjectGroupPython] H_element052  label="H_element : 0.116"  # scripted group (container) (typed FeaturePython)
  n = 0.114318
FEATURE [App::DocumentObjectGroupPython] C_element057  label="C_element : 0.656"  # scripted group (container) (typed FeaturePython)
  n = 0.655824
FEATURE [App::DocumentObjectGroupPython] O_element058  label="O_element : 0.092"  # scripted group (container) (typed FeaturePython)
  n = 0.0921831
FEATURE [App::DocumentObjectGroupPython] Mg_element004  label="Mg_element : 0.135"  # scripted group (container) (typed FeaturePython)
  n = 0.134792
FEATURE [App::DocumentObjectGroupPython] Ca_element013  label="Ca_element : 0.003"  # scripted group (container) (typed FeaturePython)
  n = 0.002883
FEATURE [App::DocumentObjectGroupPython] G4_M3_WAX  # scripted group (container) (typed FeaturePython)
  Dunit = g/cm3
  Dvalue = 1.05
  Group = -> [H_element052,C_element057,O_element058,Mg_element004,Ca_element013]
  conduct = 2
  density = 1
  expand = 3
  formula = G4_M3_WAX
  name = G4_M3_WAX
  specific = 4
FEATURE [App::DocumentObjectGroupPython] Mg_element005  label="Mg_element : 1"  # scripted group (container) (typed FeaturePython)
  n = 1
  ref = Mg_element
FEATURE [App::DocumentObjectGroupPython] C_element058  label="C_element : 031"  # scripted group (container) (typed FeaturePython)
  n = 1
  ref = C_element
FEATURE [App::DocumentObjectGroupPython] O_element059  label="O_element : 030"  # scripted group (container) (typed FeaturePython)
  n = 3
  ref = O_element
FEATURE [App::DocumentObjectGroupPython] G4_MAGNESIUM_CARBONATE  # scripted group (container) (typed FeaturePython)
  Dunit = g/cm3
  Dvalue = 2.958
  Group = -> [Mg_element005,C_element058,O_element059]
  conduct = 2
  density = 1
  expand = 3
  formula = G4_MAGNESIUM_CARBONATE
  name = G4_MAGNESIUM_CARBONATE
  specific = 4
FEATURE [App::DocumentObjectGroupPython] Mg_element006  label="Mg_element : 002"  # scripted group (container) (typed FeaturePython)
  n = 1
  ref = Mg_element
FEATURE [App::DocumentObjectGroupPython] F_element013  label="F_element : 005"  # scripted group (container) (typed FeaturePython)
  n = 2
  ref = F_element
FEATURE [App::DocumentObjectGroupPython] G4_MAGNESIUM_FLUORIDE  # scripted group (container) (typed FeaturePython)
  Dunit = g/cm3
  Dvalue = 3
  Group = -> [Mg_element006,F_element013]
  conduct = 2
  density = 1
  expand = 3
  formula = G4_MAGNESIUM_FLUORIDE
  name = G4_MAGNESIUM_FLUORIDE
  specific = 4
FEATURE [App::DocumentObjectGroupPython] Mg_element007  label="Mg_element : 003"  # scripted group (container) (typed FeaturePython)
  n = 1
  ref = Mg_element
FEATURE [App::DocumentObjectGroupPython] O_element060  label="O_element : 031"  # scripted group (container) (typed FeaturePython)
  n = 1
  ref = O_element
FEATURE [App::DocumentObjectGroupPython] G4_MAGNESIUM_OXIDE  # scripted group (container) (typed FeaturePython)
  Dunit = g/cm3
  Dvalue = 3.58
  Group = -> [Mg_element007,O_element060]
  conduct = 2
  density = 1
  expand = 3
  formula = G4_MAGNESIUM_OXIDE
  name = G4_MAGNESIUM_OXIDE
  specific = 4
FEATURE [App::DocumentObjectGroupPython] Mg_element008  label="Mg_element : 004"  # scripted group (container) (typed FeaturePython)
  n = 1
  ref = Mg_element
FEATURE [App::DocumentObjectGroupPython] B_element006  label="B_element : 006"  # scripted group (container) (typed FeaturePython)
  n = 4
  ref = B_element
FEATURE [App::DocumentObjectGroupPython] O_element061  label="O_element : 032"  # scripted group (container) (typed FeaturePython)
  n = 7
  ref = O_element
FEATURE [App::DocumentObjectGroupPython] G4_MAGNESIUM_TETRABORATE  # scripted group (container) (typed FeaturePython)
  Dunit = g/cm3
  Dvalue = 2.53
  Group = -> [Mg_element008,B_element006,O_element061]
  conduct = 2
  density = 1
  expand = 3
  formula = G4_MAGNESIUM_TETRABORATE
  name = G4_MAGNESIUM_TETRABORATE
  specific = 4
FEATURE [App::DocumentObjectGroupPython] Hg_element001  label="Hg_element : 1"  # scripted group (container) (typed FeaturePython)
  n = 1
  ref = Hg_element
FEATURE [App::DocumentObjectGroupPython] I_element004  label="I_element : 2"  # scripted group (container) (typed FeaturePython)
  n = 2
  ref = I_element
FEATURE [App::DocumentObjectGroupPython] G4_MERCURIC_IODIDE  # scripted group (container) (typed FeaturePython)
  Dunit = g/cm3
  Dvalue = 6.36
  Group = -> [Hg_element001,I_element004]
  conduct = 2
  density = 1
  expand = 3
  formula = G4_MERCURIC_IODIDE
  name = G4_MERCURIC_IODIDE
  specific = 4
FEATURE [App::DocumentObjectGroupPython] C_element059  label="C_element : 032"  # scripted group (container) (typed FeaturePython)
  n = 1
  ref = C_element
FEATURE [App::DocumentObjectGroupPython] H_element053  label="H_element : 028"  # scripted group (container) (typed FeaturePython)
  n = 4
  ref = H_element
FEATURE [App::DocumentObjectGroupPython] G4_METHANE  # scripted group (container) (typed FeaturePython)
  Dunit = g/cm3
  Dvalue = 0.000667151
  Group = -> [C_element059,H_element053]
  conduct = 2
  density = 1
  expand = 3
  formula = G4_METHANE
  name = G4_METHANE
  specific = 4
FEATURE [App::DocumentObjectGroupPython] C_element060  label="C_element : 033"  # scripted group (container) (typed FeaturePython)
  n = 1
  ref = C_element
FEATURE [App::DocumentObjectGroupPython] H_element054  label="H_element : 029"  # scripted group (container) (typed FeaturePython)
  n = 4
  ref = H_element
FEATURE [App::DocumentObjectGroupPython] O_element062  label="O_element : 033"  # scripted group (container) (typed FeaturePython)
  n = 1
  ref = O_element
FEATURE [App::DocumentObjectGroupPython] G4_METHANOL  # scripted group (container) (typed FeaturePython)
  Dunit = g/cm3
  Dvalue = 0.7914
  Group = -> [C_element060,H_element054,O_element062]
  conduct = 2
  density = 1
  expand = 3
  formula = G4_METHANOL
  name = G4_METHANOL
  specific = 4
FEATURE [App::DocumentObjectGroupPython] H_element055  label="H_element : 0.134"  # scripted group (container) (typed FeaturePython)
  n = 0.13404
FEATURE [App::DocumentObjectGroupPython] C_element061  label="C_element : 0.778"  # scripted group (container) (typed FeaturePython)
  n = 0.77796
FEATURE [App::DocumentObjectGroupPython] O_element063  label="O_element : 0.035"  # scripted group (container) (typed FeaturePython)
  n = 0.03502
FEATURE [App::DocumentObjectGroupPython] Mg_element009  label="Mg_element : 0.039"  # scripted group (container) (typed FeaturePython)
  n = 0.038594
FEATURE [App::DocumentObjectGroupPython] Ti_element002  label="Ti_element : 0.014"  # scripted group (container) (typed FeaturePython)
  n = 0.014386
FEATURE [App::DocumentObjectGroupPython] G4_MIX_D_WAX  # scripted group (container) (typed FeaturePython)
  Dunit = g/cm3
  Dvalue = 0.99
  Group = -> [H_element055,C_element061,O_element063,Mg_element009,Ti_element002]
  conduct = 2
  density = 1
  expand = 3
  formula = G4_MIX_D_WAX
  name = G4_MIX_D_WAX
  specific = 4
FEATURE [App::DocumentObjectGroupPython] H_element056  label="H_element : 0.135"  # scripted group (container) (typed FeaturePython)
  n = 0.081192
FEATURE [App::DocumentObjectGroupPython] C_element062  label="C_element : 0.583"  # scripted group (container) (typed FeaturePython)
  n = 0.583442
FEATURE [App::DocumentObjectGroupPython] N_element024  label="N_element : 0.018"  # scripted group (container) (typed FeaturePython)
  n = 0.017798
FEATURE [App::DocumentObjectGroupPython] O_element064  label="O_element : 0.186"  # scripted group (container) (typed FeaturePython)
  n = 0.186381
FEATURE [App::DocumentObjectGroupPython] Mg_element010  label="Mg_element : 0.130"  # scripted group (container) (typed FeaturePython)
  n = 0.130287
FEATURE [App::DocumentObjectGroupPython] Cl_element015  label="Cl_element : 0.588"  # scripted group (container) (typed FeaturePython)
  n = 0.0009
FEATURE [App::DocumentObjectGroupPython] G4_MS20_TISSUE  # scripted group (container) (typed FeaturePython)
  Dunit = g/cm3
  Dvalue = 1
  Group = -> [H_element056,C_element062,N_element024,O_element064,Mg_element010,Cl_element015]
  conduct = 2
  density = 1
  expand = 3
  formula = G4_MS20_TISSUE
  name = G4_MS20_TISSUE
  specific = 4
FEATURE [App::DocumentObjectGroupPython] H_element057  label="H_element : 0.136"  # scripted group (container) (typed FeaturePython)
  n = 0.102
FEATURE [App::DocumentObjectGroupPython] C_element063  label="C_element : 0.143"  # scripted group (container) (typed FeaturePython)
  n = 0.143
FEATURE [App::DocumentObjectGroupPython] N_element025  label="N_element : 0.034"  # scripted group (container) (typed FeaturePython)
  n = 0.034
FEATURE [App::DocumentObjectGroupPython] O_element065  label="O_element : 0.710"  # scripted group (container) (typed FeaturePython)
  n = 0.71
FEATURE [App::DocumentObjectGroupPython] Na_element011  label="Na_element : 0.098"  # scripted group (container) (typed FeaturePython)
  n = 0.001
FEATURE [App::DocumentObjectGroupPython] P_element007  label="P_element : 0.002"  # scripted group (container) (typed FeaturePython)
  n = 0.002
FEATURE [App::DocumentObjectGroupPython] S_element017  label="S_element : 0.018"  # scripted group (container) (typed FeaturePython)
  n = 0.003
FEATURE [App::DocumentObjectGroupPython] Cl_element016  label="Cl_element : 0.589"  # scripted group (container) (typed FeaturePython)
  n = 0.001
FEATURE [App::DocumentObjectGroupPython] K_element006  label="K_element : 0.004"  # scripted group (container) (typed FeaturePython)
  n = 0.004
FEATURE [App::DocumentObjectGroupPython] G4_MUSCLE_SKELETAL_ICRP  # scripted group (container) (typed FeaturePython)
  Dunit = g/cm3
  Dvalue = 1.05
  Group = -> [H_element057,C_element063,N_element025,O_element065,Na_element011,P_element007,S_element017,Cl_element016,K_element006]
  conduct = 2
  density = 1
  expand = 3
  formula = G4_MUSCLE_SKELETAL_ICRP
  name = G4_MUSCLE_SKELETAL_ICRP
  specific = 4
FEATURE [App::DocumentObjectGroupPython] H_element058  label="H_element : 0.137"  # scripted group (container) (typed FeaturePython)
  n = 0.102102
FEATURE [App::DocumentObjectGroupPython] C_element064  label="C_element : 0.123"  # scripted group (container) (typed FeaturePython)
  n = 0.123123
FEATURE [App::DocumentObjectGroupPython] N_element026  label="N_element : 0.756"  # scripted group (container) (typed FeaturePython)
  n = 0.035035
FEATURE [App::DocumentObjectGroupPython] O_element066  label="O_element : 0.730"  # scripted group (container) (typed FeaturePython)
  n = 0.72973
FEATURE [App::DocumentObjectGroupPython] Na_element012  label="Na_element : 0.099"  # scripted group (container) (typed FeaturePython)
  n = 0.001001
FEATURE [App::DocumentObjectGroupPython] P_element008  label="P_element : 0.106"  # scripted group (container) (typed FeaturePython)
  n = 0.002002
FEATURE [App::DocumentObjectGroupPython] S_element018  label="S_element : 0.019"  # scripted group (container) (typed FeaturePython)
  n = 0.004004
FEATURE [App::DocumentObjectGroupPython] K_element007  label="K_element : 0.016"  # scripted group (container) (typed FeaturePython)
  n = 0.003003
FEATURE [App::DocumentObjectGroupPython] G4_MUSCLE_STRIATED_ICRU  # scripted group (container) (typed FeaturePython)
  Dunit = g/cm3
  Dvalue = 1.04
  Group = -> [H_element058,C_element064,N_element026,O_element066,Na_element012,P_element008,S_element018,K_element007]
  conduct = 2
  density = 1
  expand = 3
  formula = G4_MUSCLE_STRIATED_ICRU
  name = G4_MUSCLE_STRIATED_ICRU
  specific = 4
FEATURE [App::DocumentObjectGroupPython] H_element059  label="H_element : 0.098"  # scripted group (container) (typed FeaturePython)
  n = 0.0982341
FEATURE [App::DocumentObjectGroupPython] C_element065  label="C_element : 0.156"  # scripted group (container) (typed FeaturePython)
  n = 0.156214
FEATURE [App::DocumentObjectGroupPython] N_element027  label="N_element : 0.757"  # scripted group (container) (typed FeaturePython)
  n = 0.035451
FEATURE [App::DocumentObjectGroupPython] O_element067  label="O_element : 0.880"  # scripted group (container) (typed FeaturePython)
  n = 0.710101
FEATURE [App::DocumentObjectGroupPython] G4_MUSCLE_WITH_SUCROSE  # scripted group (container) (typed FeaturePython)
  Dunit = g/cm3
  Dvalue = 1.11
  Group = -> [H_element059,C_element065,N_element027,O_element067]
  conduct = 2
  density = 1
  expand = 3
  formula = G4_MUSCLE_WITH_SUCROSE
  name = G4_MUSCLE_WITH_SUCROSE
  specific = 4
FEATURE [App::DocumentObjectGroupPython] H_element060  label="H_element : 0.138"  # scripted group (container) (typed FeaturePython)
  n = 0.101969
FEATURE [App::DocumentObjectGroupPython] C_element066  label="C_element : 0.120"  # scripted group (container) (typed FeaturePython)
  n = 0.120058
FEATURE [App::DocumentObjectGroupPython] N_element028  label="N_element : 0.758"  # scripted group (container) (typed FeaturePython)
  n = 0.035451
FEATURE [App::DocumentObjectGroupPython] O_element068  label="O_element : 0.743"  # scripted group (container) (typed FeaturePython)
  n = 0.742522
FEATURE [App::DocumentObjectGroupPython] G4_MUSCLE_WITHOUT_SUCROSE  # scripted group (container) (typed FeaturePython)
  Dunit = g/cm3
  Dvalue = 1.07
  Group = -> [H_element060,C_element066,N_element028,O_element068]
  conduct = 2
  density = 1
  expand = 3
  formula = G4_MUSCLE_WITHOUT_SUCROSE
  name = G4_MUSCLE_WITHOUT_SUCROSE
  specific = 4
FEATURE [App::DocumentObjectGroupPython] C_element067  label="C_element : 10"  # scripted group (container) (typed FeaturePython)
  n = 10
  ref = C_element
FEATURE [App::DocumentObjectGroupPython] H_element061  label="H_element : 030"  # scripted group (container) (typed FeaturePython)
  n = 8
  ref = H_element
FEATURE [App::DocumentObjectGroupPython] G4_NAPHTHALENE  # scripted group (container) (typed FeaturePython)
  Dunit = g/cm3
  Dvalue = 1.145
  Group = -> [C_element067,H_element061]
  conduct = 2
  density = 1
  expand = 3
  formula = G4_NAPHTHALENE
  name = G4_NAPHTHALENE
  specific = 4
FEATURE [App::DocumentObjectGroupPython] C_element068  label="C_element : 034"  # scripted group (container) (typed FeaturePython)
  n = 6
  ref = C_element
FEATURE [App::DocumentObjectGroupPython] H_element062  label="H_element : 031"  # scripted group (container) (typed FeaturePython)
  n = 5
  ref = H_element
FEATURE [App::DocumentObjectGroupPython] N_element029  label="N_element : 012"  # scripted group (container) (typed FeaturePython)
  n = 1
  ref = N_element
FEATURE [App::DocumentObjectGroupPython] O_element069  label="O_element : 034"  # scripted group (container) (typed FeaturePython)
  n = 2
  ref = O_element
FEATURE [App::DocumentObjectGroupPython] G4_NITROBENZENE  # scripted group (container) (typed FeaturePython)
  Dunit = g/cm3
  Dvalue = 1.19867
  Group = -> [C_element068,H_element062,N_element029,O_element069]
  conduct = 2
  density = 1
  expand = 3
  formula = G4_NITROBENZENE
  name = G4_NITROBENZENE
  specific = 4
FEATURE [App::DocumentObjectGroupPython] N_element030  label="N_element : 013"  # scripted group (container) (typed FeaturePython)
  n = 2
  ref = N_element
FEATURE [App::DocumentObjectGroupPython] O_element070  label="O_element : 035"  # scripted group (container) (typed FeaturePython)
  n = 1
  ref = O_element
FEATURE [App::DocumentObjectGroupPython] G4_NITROUS_OXIDE  # scripted group (container) (typed FeaturePython)
  Dunit = g/cm3
  Dvalue = 0.00183094
  Group = -> [N_element030,O_element070]
  conduct = 2
  density = 1
  expand = 3
  formula = G4_NITROUS_OXIDE
  name = G4_NITROUS_OXIDE
  specific = 4
FEATURE [App::DocumentObjectGroupPython] H_element063  label="H_element : 0.104"  # scripted group (container) (typed FeaturePython)
  n = 0.103509
FEATURE [App::DocumentObjectGroupPython] C_element069  label="C_element : 0.648"  # scripted group (container) (typed FeaturePython)
  n = 0.648416
FEATURE [App::DocumentObjectGroupPython] N_element031  label="N_element : 0.100"  # scripted group (container) (typed FeaturePython)
  n = 0.0995361
FEATURE [App::DocumentObjectGroupPython] O_element071  label="O_element : 0.149"  # scripted group (container) (typed FeaturePython)
  n = 0.148539
FEATURE [App::DocumentObjectGroupPython] G4_NYLON_8062  label="G4_NYLON-8062"  # scripted group (container) (typed FeaturePython)
  Dunit = g/cm3
  Dvalue = 1.08
  Group = -> [H_element063,C_element069,N_element031,O_element071]
  conduct = 2
  density = 1
  expand = 3
  formula = G4_NYLON-8062
  name = G4_NYLON-8062
  specific = 4
FEATURE [App::DocumentObjectGroupPython] C_element070  label="C_element : 035"  # scripted group (container) (typed FeaturePython)
  n = 6
  ref = C_element
FEATURE [App::DocumentObjectGroupPython] H_element064  label="H_element : 11"  # scripted group (container) (typed FeaturePython)
  n = 11
  ref = H_element
FEATURE [App::DocumentObjectGroupPython] N_element032  label="N_element : 014"  # scripted group (container) (typed FeaturePython)
  n = 1
  ref = N_element
FEATURE [App::DocumentObjectGroupPython] O_element072  label="O_element : 036"  # scripted group (container) (typed FeaturePython)
  n = 1
  ref = O_element
FEATURE [App::DocumentObjectGroupPython] G4_NYLON_6_6  label="G4_NYLON-6-6"  # scripted group (container) (typed FeaturePython)
  Dunit = g/cm3
  Dvalue = 1.14
  Group = -> [C_element070,H_element064,N_element032,O_element072]
  conduct = 2
  density = 1
  expand = 3
  formula = G4_NYLON-6-6
  name = G4_NYLON-6-6
  specific = 4
FEATURE [App::DocumentObjectGroupPython] H_element065  label="H_element : 0.139"  # scripted group (container) (typed FeaturePython)
  n = 0.107062
FEATURE [App::DocumentObjectGroupPython] C_element071  label="C_element : 0.680"  # scripted group (container) (typed FeaturePython)
  n = 0.680449
FEATURE [App::DocumentObjectGroupPython] N_element033  label="N_element : 0.099"  # scripted group (container) (typed FeaturePython)
  n = 0.099189
FEATURE [App::DocumentObjectGroupPython] O_element073  label="O_element : 0.113"  # scripted group (container) (typed FeaturePython)
  n = 0.1133
FEATURE [App::DocumentObjectGroupPython] G4_NYLON_6_10  label="G4_NYLON-6-10"  # scripted group (container) (typed FeaturePython)
  Dunit = g/cm3
  Dvalue = 1.14
  Group = -> [H_element065,C_element071,N_element033,O_element073]
  conduct = 2
  density = 1
  expand = 3
  formula = G4_NYLON-6-10
  name = G4_NYLON-6-10
  specific = 4
FEATURE [App::DocumentObjectGroupPython] H_element066  label="H_element : 0.140"  # scripted group (container) (typed FeaturePython)
  n = 0.115476
FEATURE [App::DocumentObjectGroupPython] C_element072  label="C_element : 0.721"  # scripted group (container) (typed FeaturePython)
  n = 0.720818
FEATURE [App::DocumentObjectGroupPython] N_element034  label="N_element : 0.076"  # scripted group (container) (typed FeaturePython)
  n = 0.0764169
FEATURE [App::DocumentObjectGroupPython] O_element074  label="O_element : 0.087"  # scripted group (container) (typed FeaturePython)
  n = 0.0872889
FEATURE [App::DocumentObjectGroupPython] G4_NYLON_11_RILSAN  label="G4_NYLON-11_RILSAN"  # scripted group (container) (typed FeaturePython)
  Dunit = g/cm3
  Dvalue = 1.425
  Group = -> [H_element066,C_element072,N_element034,O_element074]
  conduct = 2
  density = 1
  expand = 3
  formula = G4_NYLON-11_RILSAN
  name = G4_NYLON-11_RILSAN
  specific = 4
FEATURE [App::DocumentObjectGroupPython] C_element073  label="C_element : 8"  # scripted group (container) (typed FeaturePython)
  n = 8
  ref = C_element
FEATURE [App::DocumentObjectGroupPython] H_element067  label="H_element : 18"  # scripted group (container) (typed FeaturePython)
  n = 18
  ref = H_element
FEATURE [App::DocumentObjectGroupPython] G4_OCTANE  # scripted group (container) (typed FeaturePython)
  Dunit = g/cm3
  Dvalue = 0.7026
  Group = -> [C_element073,H_element067]
  conduct = 2
  density = 1
  expand = 3
  formula = G4_OCTANE
  name = G4_OCTANE
  specific = 4
FEATURE [App::DocumentObjectGroupPython] C_element074  label="C_element : 25"  # scripted group (container) (typed FeaturePython)
  n = 25
  ref = C_element
FEATURE [App::DocumentObjectGroupPython] H_element068  label="H_element : 52"  # scripted group (container) (typed FeaturePython)
  n = 52
  ref = H_element
FEATURE [App::DocumentObjectGroupPython] G4_PARAFFIN  # scripted group (container) (typed FeaturePython)
  Dunit = g/cm3
  Dvalue = 0.93
  Group = -> [C_element074,H_element068]
  conduct = 2
  density = 1
  expand = 3
  formula = G4_PARAFFIN
  name = G4_PARAFFIN
  specific = 4
FEATURE [App::DocumentObjectGroupPython] C_element075  label="C_element : 036"  # scripted group (container) (typed FeaturePython)
  n = 5
  ref = C_element
FEATURE [App::DocumentObjectGroupPython] H_element069  label="H_element : 032"  # scripted group (container) (typed FeaturePython)
  n = 12
  ref = H_element
FEATURE [App::DocumentObjectGroupPython] G4_N_PENTANE  label="G4_N-PENTANE"  # scripted group (container) (typed FeaturePython)
  Dunit = g/cm3
  Dvalue = 0.6262
  Group = -> [C_element075,H_element069]
  conduct = 2
  density = 1
  expand = 3
  formula = G4_N-PENTANE
  name = G4_N-PENTANE
  specific = 4
FEATURE [App::DocumentObjectGroupPython] H_element070  label="H_element : 0.014"  # scripted group (container) (typed FeaturePython)
  n = 0.0141
FEATURE [App::DocumentObjectGroupPython] C_element076  label="C_element : 0.072"  # scripted group (container) (typed FeaturePython)
  n = 0.072261
FEATURE [App::DocumentObjectGroupPython] N_element035  label="N_element : 0.019"  # scripted group (container) (typed FeaturePython)
  n = 0.01932
FEATURE [App::DocumentObjectGroupPython] O_element075  label="O_element : 0.066"  # scripted group (container) (typed FeaturePython)
  n = 0.066101
FEATURE [App::DocumentObjectGroupPython] S_element019  label="S_element : 0.020"  # scripted group (container) (typed FeaturePython)
  n = 0.00189
FEATURE [App::DocumentObjectGroupPython] Br_element004  label="Br_element : 0.349"  # scripted group (container) (typed FeaturePython)
  n = 0.349103
FEATURE [App::DocumentObjectGroupPython] Ag_element001  label="Ag_element : 0.474"  # scripted group (container) (typed FeaturePython)
  n = 0.474105
FEATURE [App::DocumentObjectGroupPython] I_element005  label="I_element : 0.003"  # scripted group (container) (typed FeaturePython)
  n = 0.00312
FEATURE [App::DocumentObjectGroupPython] G4_PHOTO_EMULSION  # scripted group (container) (typed FeaturePython)
  Dunit = g/cm3
  Dvalue = 3.815
  Group = -> [H_element070,C_element076,N_element035,O_element075,S_element019,Br_element004,Ag_element001,I_element005]
  conduct = 2
  density = 1
  expand = 3
  formula = G4_PHOTO_EMULSION
  name = G4_PHOTO_EMULSION
  specific = 4
FEATURE [App::DocumentObjectGroupPython] C_element077  label="C_element : 9"  # scripted group (container) (typed FeaturePython)
  n = 9
  ref = C_element
FEATURE [App::DocumentObjectGroupPython] H_element071  label="H_element : 033"  # scripted group (container) (typed FeaturePython)
  n = 10
  ref = H_element
FEATURE [App::DocumentObjectGroupPython] G4_PLASTIC_SC_VINYLTOLUENE  # scripted group (container) (typed FeaturePython)
  Dunit = g/cm3
  Dvalue = 1.032
  Group = -> [C_element077,H_element071]
  conduct = 2
  density = 1
  expand = 3
  formula = G4_PLASTIC_SC_VINYLTOLUENE
  name = G4_PLASTIC_SC_VINYLTOLUENE
  specific = 4
FEATURE [App::DocumentObjectGroupPython] Pu_element001  label="Pu_element : 1"  # scripted group (container) (typed FeaturePython)
  n = 1
  ref = Pu_element
FEATURE [App::DocumentObjectGroupPython] O_element076  label="O_element : 037"  # scripted group (container) (typed FeaturePython)
  n = 2
  ref = O_element
FEATURE [App::DocumentObjectGroupPython] G4_PLUTONIUM_DIOXIDE  # scripted group (container) (typed FeaturePython)
  Dunit = g/cm3
  Dvalue = 11.46
  Group = -> [Pu_element001,O_element076]
  conduct = 2
  density = 1
  expand = 3
  formula = G4_PLUTONIUM_DIOXIDE
  name = G4_PLUTONIUM_DIOXIDE
  specific = 4
FEATURE [App::DocumentObjectGroupPython] C_element078  label="C_element : 037"  # scripted group (container) (typed FeaturePython)
  n = 3
  ref = C_element
FEATURE [App::DocumentObjectGroupPython] H_element072  label="H_element : 034"  # scripted group (container) (typed FeaturePython)
  n = 3
  ref = H_element
FEATURE [App::DocumentObjectGroupPython] N_element036  label="N_element : 015"  # scripted group (container) (typed FeaturePython)
  n = 1
  ref = N_element
FEATURE [App::DocumentObjectGroupPython] G4_POLYACRYLONITRILE  # scripted group (container) (typed FeaturePython)
  Dunit = g/cm3
  Dvalue = 1.17
  Group = -> [C_element078,H_element072,N_element036]
  conduct = 2
  density = 1
  expand = 3
  formula = G4_POLYACRYLONITRILE
  name = G4_POLYACRYLONITRILE
  specific = 4
FEATURE [App::DocumentObjectGroupPython] C_element079  label="C_element : 16"  # scripted group (container) (typed FeaturePython)
  n = 16
  ref = C_element
FEATURE [App::DocumentObjectGroupPython] H_element073  label="H_element : 035"  # scripted group (container) (typed FeaturePython)
  n = 14
  ref = H_element
FEATURE [App::DocumentObjectGroupPython] O_element077  label="O_element : 038"  # scripted group (container) (typed FeaturePython)
  n = 3
  ref = O_element
FEATURE [App::DocumentObjectGroupPython] G4_POLYCARBONATE  # scripted group (container) (typed FeaturePython)
  Dunit = g/cm3
  Dvalue = 1.2
  Group = -> [C_element079,H_element073,O_element077]
  conduct = 2
  density = 1
  expand = 3
  formula = G4_POLYCARBONATE
  name = G4_POLYCARBONATE
  specific = 4
FEATURE [App::DocumentObjectGroupPython] C_element080  label="C_element : 038"  # scripted group (container) (typed FeaturePython)
  n = 8
  ref = C_element
FEATURE [App::DocumentObjectGroupPython] H_element074  label="H_element : 036"  # scripted group (container) (typed FeaturePython)
  n = 7
  ref = H_element
FEATURE [App::DocumentObjectGroupPython] Cl_element017  label="Cl_element : 007"  # scripted group (container) (typed FeaturePython)
  n = 1
  ref = Cl_element
FEATURE [App::DocumentObjectGroupPython] G4_POLYCHLOROSTYRENE  # scripted group (container) (typed FeaturePython)
  Dunit = g/cm3
  Dvalue = 1.3
  Group = -> [C_element080,H_element074,Cl_element017]
  conduct = 2
  density = 1
  expand = 3
  formula = G4_POLYCHLOROSTYRENE
  name = G4_POLYCHLOROSTYRENE
  specific = 4
FEATURE [App::DocumentObjectGroupPython] C_element081  label="C_element : 039"  # scripted group (container) (typed FeaturePython)
  n = 1
  ref = C_element
FEATURE [App::DocumentObjectGroupPython] H_element075  label="H_element : 037"  # scripted group (container) (typed FeaturePython)
  n = 2
  ref = H_element
FEATURE [App::DocumentObjectGroupPython] G4_POLYETHYLENE  # scripted group (container) (typed FeaturePython)
  Dunit = g/cm3
  Dvalue = 0.94
  Group = -> [C_element081,H_element075]
  conduct = 2
  density = 1
  expand = 3
  formula = G4_POLYETHYLENE
  name = G4_POLYETHYLENE
  specific = 4
FEATURE [App::DocumentObjectGroupPython] C_element082  label="C_element : 040"  # scripted group (container) (typed FeaturePython)
  n = 10
  ref = C_element
FEATURE [App::DocumentObjectGroupPython] H_element076  label="H_element : 038"  # scripted group (container) (typed FeaturePython)
  n = 8
  ref = H_element
FEATURE [App::DocumentObjectGroupPython] O_element078  label="O_element : 039"  # scripted group (container) (typed FeaturePython)
  n = 4
  ref = O_element
FEATURE [App::DocumentObjectGroupPython] G4_MYLAR  # scripted group (container) (typed FeaturePython)
  Dunit = g/cm3
  Dvalue = 1.4
  Group = -> [C_element082,H_element076,O_element078]
  conduct = 2
  density = 1
  expand = 3
  formula = G4_MYLAR
  name = G4_MYLAR
  specific = 4
FEATURE [App::DocumentObjectGroupPython] C_element083  label="C_element : 041"  # scripted group (container) (typed FeaturePython)
  n = 5
  ref = C_element
FEATURE [App::DocumentObjectGroupPython] H_element077  label="H_element : 039"  # scripted group (container) (typed FeaturePython)
  n = 8
  ref = H_element
FEATURE [App::DocumentObjectGroupPython] O_element079  label="O_element : 040"  # scripted group (container) (typed FeaturePython)
  n = 2
  ref = O_element
FEATURE [App::DocumentObjectGroupPython] G4_PLEXIGLASS  # scripted group (container) (typed FeaturePython)
  Dunit = g/cm3
  Dvalue = 1.19
  Group = -> [C_element083,H_element077,O_element079]
  conduct = 2
  density = 1
  expand = 3
  formula = G4_PLEXIGLASS
  name = G4_PLEXIGLASS
  specific = 4
FEATURE [App::DocumentObjectGroupPython] C_element084  label="C_element : 042"  # scripted group (container) (typed FeaturePython)
  n = 1
  ref = C_element
FEATURE [App::DocumentObjectGroupPython] H_element078  label="H_element : 040"  # scripted group (container) (typed FeaturePython)
  n = 2
  ref = H_element
FEATURE [App::DocumentObjectGroupPython] O_element080  label="O_element : 041"  # scripted group (container) (typed FeaturePython)
  n = 1
  ref = O_element
FEATURE [App::DocumentObjectGroupPython] G4_POLYOXYMETHYLENE  # scripted group (container) (typed FeaturePython)
  Dunit = g/cm3
  Dvalue = 1.425
  Group = -> [C_element084,H_element078,O_element080]
  conduct = 2
  density = 1
  expand = 3
  formula = G4_POLYOXYMETHYLENE
  name = G4_POLYOXYMETHYLENE
  specific = 4
FEATURE [App::DocumentObjectGroupPython] C_element085  label="C_element : 043"  # scripted group (container) (typed FeaturePython)
  n = 2
  ref = C_element
FEATURE [App::DocumentObjectGroupPython] H_element079  label="H_element : 041"  # scripted group (container) (typed FeaturePython)
  n = 4
  ref = H_element
FEATURE [App::DocumentObjectGroupPython] G4_POLYPROPYLENE  # scripted group (container) (typed FeaturePython)
  Dunit = g/cm3
  Dvalue = 0.9
  Group = -> [C_element085,H_element079]
  conduct = 2
  density = 1
  expand = 3
  formula = G4_POLYPROPYLENE
  name = G4_POLYPROPYLENE
  specific = 4
FEATURE [App::DocumentObjectGroupPython] C_element086  label="C_element : 044"  # scripted group (container) (typed FeaturePython)
  n = 8
  ref = C_element
FEATURE [App::DocumentObjectGroupPython] H_element080  label="H_element : 042"  # scripted group (container) (typed FeaturePython)
  n = 8
  ref = H_element
FEATURE [App::DocumentObjectGroupPython] G4_POLYSTYRENE  # scripted group (container) (typed FeaturePython)
  Dunit = g/cm3
  Dvalue = 1.06
  Group = -> [C_element086,H_element080]
  conduct = 2
  density = 1
  expand = 3
  formula = G4_POLYSTYRENE
  name = G4_POLYSTYRENE
  specific = 4
FEATURE [App::DocumentObjectGroupPython] C_element087  label="C_element : 045"  # scripted group (container) (typed FeaturePython)
  n = 2
  ref = C_element
FEATURE [App::DocumentObjectGroupPython] F_element014  label="F_element : 4"  # scripted group (container) (typed FeaturePython)
  n = 4
  ref = F_element
FEATURE [App::DocumentObjectGroupPython] G4_TEFLON  # scripted group (container) (typed FeaturePython)
  Dunit = g/cm3
  Dvalue = 2.2
  Group = -> [C_element087,F_element014]
  conduct = 2
  density = 1
  expand = 3
  formula = G4_TEFLON
  name = G4_TEFLON
  specific = 4
FEATURE [App::DocumentObjectGroupPython] C_element088  label="C_element : 046"  # scripted group (container) (typed FeaturePython)
  n = 2
  ref = C_element
FEATURE [App::DocumentObjectGroupPython] F_element015  label="F_element : 006"  # scripted group (container) (typed FeaturePython)
  n = 3
  ref = F_element
FEATURE [App::DocumentObjectGroupPython] Cl_element018  label="Cl_element : 008"  # scripted group (container) (typed FeaturePython)
  n = 1
  ref = Cl_element
FEATURE [App::DocumentObjectGroupPython] G4_POLYTRIFLUOROCHLOROETHYLENE  # scripted group (container) (typed FeaturePython)
  Dunit = g/cm3
  Dvalue = 2.1
  Group = -> [C_element088,F_element015,Cl_element018]
  conduct = 2
  density = 1
  expand = 3
  formula = G4_POLYTRIFLUOROCHLOROETHYLENE
  name = G4_POLYTRIFLUOROCHLOROETHYLENE
  specific = 4
FEATURE [App::DocumentObjectGroupPython] C_element089  label="C_element : 047"  # scripted group (container) (typed FeaturePython)
  n = 4
  ref = C_element
FEATURE [App::DocumentObjectGroupPython] H_element081  label="H_element : 043"  # scripted group (container) (typed FeaturePython)
  n = 6
  ref = H_element
FEATURE [App::DocumentObjectGroupPython] O_element081  label="O_element : 042"  # scripted group (container) (typed FeaturePython)
  n = 2
  ref = O_element
FEATURE [App::DocumentObjectGroupPython] G4_POLYVINYL_ACETATE  # scripted group (container) (typed FeaturePython)
  Dunit = g/cm3
  Dvalue = 1.19
  Group = -> [C_element089,H_element081,O_element081]
  conduct = 2
  density = 1
  expand = 3
  formula = G4_POLYVINYL_ACETATE
  name = G4_POLYVINYL_ACETATE
  specific = 4
FEATURE [App::DocumentObjectGroupPython] C_element090  label="C_element : 048"  # scripted group (container) (typed FeaturePython)
  n = 2
  ref = C_element
FEATURE [App::DocumentObjectGroupPython] H_element082  label="H_element : 044"  # scripted group (container) (typed FeaturePython)
  n = 4
  ref = H_element
FEATURE [App::DocumentObjectGroupPython] O_element082  label="O_element : 043"  # scripted group (container) (typed FeaturePython)
  n = 1
  ref = O_element
FEATURE [App::DocumentObjectGroupPython] G4_POLYVINYL_ALCOHOL  # scripted group (container) (typed FeaturePython)
  Dunit = g/cm3
  Dvalue = 1.3
  Group = -> [C_element090,H_element082,O_element082]
  conduct = 2
  density = 1
  expand = 3
  formula = G4_POLYVINYL_ALCOHOL
  name = G4_POLYVINYL_ALCOHOL
  specific = 4
FEATURE [App::DocumentObjectGroupPython] C_element091  label="C_element : 049"  # scripted group (container) (typed FeaturePython)
  n = 8
  ref = C_element
FEATURE [App::DocumentObjectGroupPython] H_element083  label="H_element : 045"  # scripted group (container) (typed FeaturePython)
  n = 14
  ref = H_element
FEATURE [App::DocumentObjectGroupPython] O_element083  label="O_element : 044"  # scripted group (container) (typed FeaturePython)
  n = 2
  ref = O_element
FEATURE [App::DocumentObjectGroupPython] G4_POLYVINYL_BUTYRAL  # scripted group (container) (typed FeaturePython)
  Dunit = g/cm3
  Dvalue = 1.12
  Group = -> [C_element091,H_element083,O_element083]
  conduct = 2
  density = 1
  expand = 3
  formula = G4_POLYVINYL_BUTYRAL
  name = G4_POLYVINYL_BUTYRAL
  specific = 4
FEATURE [App::DocumentObjectGroupPython] C_element092  label="C_element : 050"  # scripted group (container) (typed FeaturePython)
  n = 2
  ref = C_element
FEATURE [App::DocumentObjectGroupPython] H_element084  label="H_element : 046"  # scripted group (container) (typed FeaturePython)
  n = 3
  ref = H_element
FEATURE [App::DocumentObjectGroupPython] Cl_element019  label="Cl_element : 009"  # scripted group (container) (typed FeaturePython)
  n = 1
  ref = Cl_element
FEATURE [App::DocumentObjectGroupPython] G4_POLYVINYL_CHLORIDE  # scripted group (container) (typed FeaturePython)
  Dunit = g/cm3
  Dvalue = 1.3
  Group = -> [C_element092,H_element084,Cl_element019]
  conduct = 2
  density = 1
  expand = 3
  formula = G4_POLYVINYL_CHLORIDE
  name = G4_POLYVINYL_CHLORIDE
  specific = 4
FEATURE [App::DocumentObjectGroupPython] C_element093  label="C_element : 051"  # scripted group (container) (typed FeaturePython)
  n = 2
  ref = C_element
FEATURE [App::DocumentObjectGroupPython] H_element085  label="H_element : 047"  # scripted group (container) (typed FeaturePython)
  n = 2
  ref = H_element
FEATURE [App::DocumentObjectGroupPython] Cl_element020  label="Cl_element : 010"  # scripted group (container) (typed FeaturePython)
  n = 2
  ref = Cl_element
FEATURE [App::DocumentObjectGroupPython] G4_POLYVINYLIDENE_CHLORIDE  # scripted group (container) (typed FeaturePython)
  Dunit = g/cm3
  Dvalue = 1.7
  Group = -> [C_element093,H_element085,Cl_element020]
  conduct = 2
  density = 1
  expand = 3
  formula = G4_POLYVINYLIDENE_CHLORIDE
  name = G4_POLYVINYLIDENE_CHLORIDE
  specific = 4
FEATURE [App::DocumentObjectGroupPython] C_element094  label="C_element : 052"  # scripted group (container) (typed FeaturePython)
  n = 2
  ref = C_element
FEATURE [App::DocumentObjectGroupPython] H_element086  label="H_element : 048"  # scripted group (container) (typed FeaturePython)
  n = 2
  ref = H_element
FEATURE [App::DocumentObjectGroupPython] F_element016  label="F_element : 007"  # scripted group (container) (typed FeaturePython)
  n = 2
  ref = F_element
FEATURE [App::DocumentObjectGroupPython] G4_POLYVINYLIDENE_FLUORIDE  # scripted group (container) (typed FeaturePython)
  Dunit = g/cm3
  Dvalue = 1.76
  Group = -> [C_element094,H_element086,F_element016]
  conduct = 2
  density = 1
  expand = 3
  formula = G4_POLYVINYLIDENE_FLUORIDE
  name = G4_POLYVINYLIDENE_FLUORIDE
  specific = 4
FEATURE [App::DocumentObjectGroupPython] C_element095  label="C_element : 053"  # scripted group (container) (typed FeaturePython)
  n = 6
  ref = C_element
FEATURE [App::DocumentObjectGroupPython] H_element087  label="H_element : 9"  # scripted group (container) (typed FeaturePython)
  n = 9
  ref = H_element
FEATURE [App::DocumentObjectGroupPython] N_element037  label="N_element : 016"  # scripted group (container) (typed FeaturePython)
  n = 1
  ref = N_element
FEATURE [App::DocumentObjectGroupPython] O_element084  label="O_element : 045"  # scripted group (container) (typed FeaturePython)
  n = 1
  ref = O_element
FEATURE [App::DocumentObjectGroupPython] G4_POLYVINYL_PYRROLIDONE  # scripted group (container) (typed FeaturePython)
  Dunit = g/cm3
  Dvalue = 1.25
  Group = -> [C_element095,H_element087,N_element037,O_element084]
  conduct = 2
  density = 1
  expand = 3
  formula = G4_POLYVINYL_PYRROLIDONE
  name = G4_POLYVINYL_PYRROLIDONE
  specific = 4
FEATURE [App::DocumentObjectGroupPython] K_element008  label="K_element : 1"  # scripted group (container) (typed FeaturePython)
  n = 1
  ref = K_element
FEATURE [App::DocumentObjectGroupPython] I_element006  label="I_element : 003"  # scripted group (container) (typed FeaturePython)
  n = 1
  ref = I_element
FEATURE [App::DocumentObjectGroupPython] G4_POTASSIUM_IODIDE  # scripted group (container) (typed FeaturePython)
  Dunit = g/cm3
  Dvalue = 3.13
  Group = -> [K_element008,I_element006]
  conduct = 2
  density = 1
  expand = 3
  formula = G4_POTASSIUM_IODIDE
  name = G4_POTASSIUM_IODIDE
  specific = 4
FEATURE [App::DocumentObjectGroupPython] K_element009  label="K_element : 2"  # scripted group (container) (typed FeaturePython)
  n = 2
  ref = K_element
FEATURE [App::DocumentObjectGroupPython] O_element085  label="O_element : 046"  # scripted group (container) (typed FeaturePython)
  n = 1
  ref = O_element
FEATURE [App::DocumentObjectGroupPython] G4_POTASSIUM_OXIDE  # scripted group (container) (typed FeaturePython)
  Dunit = g/cm3
  Dvalue = 2.32
  Group = -> [K_element009,O_element085]
  conduct = 2
  density = 1
  expand = 3
  formula = G4_POTASSIUM_OXIDE
  name = G4_POTASSIUM_OXIDE
  specific = 4
FEATURE [App::DocumentObjectGroupPython] C_element096  label="C_element : 054"  # scripted group (container) (typed FeaturePython)
  n = 3
  ref = C_element
FEATURE [App::DocumentObjectGroupPython] H_element088  label="H_element : 049"  # scripted group (container) (typed FeaturePython)
  n = 8
  ref = H_element
FEATURE [App::DocumentObjectGroupPython] G4_PROPANE  # scripted group (container) (typed FeaturePython)
  Dunit = g/cm3
  Dvalue = 0.00187939
  Group = -> [C_element096,H_element088]
  conduct = 2
  density = 1
  expand = 3
  formula = G4_PROPANE
  name = G4_PROPANE
  specific = 4
FEATURE [App::DocumentObjectGroupPython] C_element097  label="C_element : 055"  # scripted group (container) (typed FeaturePython)
  n = 3
  ref = C_element
FEATURE [App::DocumentObjectGroupPython] H_element089  label="H_element : 050"  # scripted group (container) (typed FeaturePython)
  n = 8
  ref = H_element
FEATURE [App::DocumentObjectGroupPython] G4_lPROPANE  # scripted group (container) (typed FeaturePython)
  Dunit = g/cm3
  Dvalue = 0.43
  Group = -> [C_element097,H_element089]
  conduct = 2
  density = 1
  expand = 3
  formula = G4_lPROPANE
  name = G4_lPROPANE
  specific = 4
FEATURE [App::DocumentObjectGroupPython] C_element098  label="C_element : 056"  # scripted group (container) (typed FeaturePython)
  n = 3
  ref = C_element
FEATURE [App::DocumentObjectGroupPython] H_element090  label="H_element : 051"  # scripted group (container) (typed FeaturePython)
  n = 8
  ref = H_element
FEATURE [App::DocumentObjectGroupPython] O_element086  label="O_element : 047"  # scripted group (container) (typed FeaturePython)
  n = 1
  ref = O_element
FEATURE [App::DocumentObjectGroupPython] G4_N_PROPYL_ALCOHOL  label="G4_N-PROPYL_ALCOHOL"  # scripted group (container) (typed FeaturePython)
  Dunit = g/cm3
  Dvalue = 0.8035
  Group = -> [C_element098,H_element090,O_element086]
  conduct = 2
  density = 1
  expand = 3
  formula = G4_N-PROPYL_ALCOHOL
  name = G4_N-PROPYL_ALCOHOL
  specific = 4
FEATURE [App::DocumentObjectGroupPython] C_element099  label="C_element : 057"  # scripted group (container) (typed FeaturePython)
  n = 5
  ref = C_element
FEATURE [App::DocumentObjectGroupPython] H_element091  label="H_element : 052"  # scripted group (container) (typed FeaturePython)
  n = 5
  ref = H_element
FEATURE [App::DocumentObjectGroupPython] N_element038  label="N_element : 017"  # scripted group (container) (typed FeaturePython)
  n = 1
  ref = N_element
FEATURE [App::DocumentObjectGroupPython] G4_PYRIDINE  # scripted group (container) (typed FeaturePython)
  Dunit = g/cm3
  Dvalue = 0.9819
  Group = -> [C_element099,H_element091,N_element038]
  conduct = 2
  density = 1
  expand = 3
  formula = G4_PYRIDINE
  name = G4_PYRIDINE
  specific = 4
FEATURE [App::DocumentObjectGroupPython] H_element092  label="H_element : 0.144"  # scripted group (container) (typed FeaturePython)
  n = 0.143711
FEATURE [App::DocumentObjectGroupPython] C_element100  label="C_element : 0.856"  # scripted group (container) (typed FeaturePython)
  n = 0.856289
FEATURE [App::DocumentObjectGroupPython] G4_RUBBER_BUTYL  # scripted group (container) (typed FeaturePython)
  Dunit = g/cm3
  Dvalue = 0.92
  Group = -> [H_element092,C_element100]
  conduct = 2
  density = 1
  expand = 3
  formula = G4_RUBBER_BUTYL
  name = G4_RUBBER_BUTYL
  specific = 4
FEATURE [App::DocumentObjectGroupPython] H_element093  label="H_element : 0.118"  # scripted group (container) (typed FeaturePython)
  n = 0.118371
FEATURE [App::DocumentObjectGroupPython] C_element101  label="C_element : 0.882"  # scripted group (container) (typed FeaturePython)
  n = 0.881629
FEATURE [App::DocumentObjectGroupPython] G4_RUBBER_NATURAL  # scripted group (container) (typed FeaturePython)
  Dunit = g/cm3
  Dvalue = 0.92
  Group = -> [H_element093,C_element101]
  conduct = 2
  density = 1
  expand = 3
  formula = G4_RUBBER_NATURAL
  name = G4_RUBBER_NATURAL
  specific = 4
FEATURE [App::DocumentObjectGroupPython] H_element094  label="H_element : 0.145"  # scripted group (container) (typed FeaturePython)
  n = 0.05692
FEATURE [App::DocumentObjectGroupPython] C_element102  label="C_element : 0.543"  # scripted group (container) (typed FeaturePython)
  n = 0.542646
FEATURE [App::DocumentObjectGroupPython] Cl_element021  label="Cl_element : 0.400"  # scripted group (container) (typed FeaturePython)
  n = 0.400434
FEATURE [App::DocumentObjectGroupPython] G4_RUBBER_NEOPRENE  # scripted group (container) (typed FeaturePython)
  Dunit = g/cm3
  Dvalue = 1.23
  Group = -> [H_element094,C_element102,Cl_element021]
  conduct = 2
  density = 1
  expand = 3
  formula = G4_RUBBER_NEOPRENE
  name = G4_RUBBER_NEOPRENE
  specific = 4
FEATURE [App::DocumentObjectGroupPython] Si_element006  label="Si_element : 1"  # scripted group (container) (typed FeaturePython)
  n = 1
  ref = Si_element
FEATURE [App::DocumentObjectGroupPython] O_element087  label="O_element : 048"  # scripted group (container) (typed FeaturePython)
  n = 2
  ref = O_element
FEATURE [App::DocumentObjectGroupPython] G4_SILICON_DIOXIDE  # scripted group (container) (typed FeaturePython)
  Dunit = g/cm3
  Dvalue = 2.32
  Group = -> [Si_element006,O_element087]
  conduct = 2
  density = 1
  expand = 3
  formula = G4_SILICON_DIOXIDE
  name = G4_SILICON_DIOXIDE
  specific = 4
FEATURE [App::DocumentObjectGroupPython] Ag_element002  label="Ag_element : 1"  # scripted group (container) (typed FeaturePython)
  n = 1
  ref = Ag_element
FEATURE [App::DocumentObjectGroupPython] Br_element005  label="Br_element : 003"  # scripted group (container) (typed FeaturePython)
  n = 1
  ref = Br_element
FEATURE [App::DocumentObjectGroupPython] G4_SILVER_BROMIDE  # scripted group (container) (typed FeaturePython)
  Dunit = g/cm3
  Dvalue = 6.473
  Group = -> [Ag_element002,Br_element005]
  conduct = 2
  density = 1
  expand = 3
  formula = G4_SILVER_BROMIDE
  name = G4_SILVER_BROMIDE
  specific = 4
FEATURE [App::DocumentObjectGroupPython] Ag_element003  label="Ag_element : 002"  # scripted group (container) (typed FeaturePython)
  n = 1
  ref = Ag_element
FEATURE [App::DocumentObjectGroupPython] Cl_element022  label="Cl_element : 011"  # scripted group (container) (typed FeaturePython)
  n = 1
  ref = Cl_element
FEATURE [App::DocumentObjectGroupPython] G4_SILVER_CHLORIDE  # scripted group (container) (typed FeaturePython)
  Dunit = g/cm3
  Dvalue = 5.56
  Group = -> [Ag_element003,Cl_element022]
  conduct = 2
  density = 1
  expand = 3
  formula = G4_SILVER_CHLORIDE
  name = G4_SILVER_CHLORIDE
  specific = 4
FEATURE [App::DocumentObjectGroupPython] Br_element006  label="Br_element : 0.423"  # scripted group (container) (typed FeaturePython)
  n = 0.422895
FEATURE [App::DocumentObjectGroupPython] Ag_element004  label="Ag_element : 0.574"  # scripted group (container) (typed FeaturePython)
  n = 0.573748
FEATURE [App::DocumentObjectGroupPython] I_element007  label="I_element : 0.649"  # scripted group (container) (typed FeaturePython)
  n = 0.003357
FEATURE [App::DocumentObjectGroupPython] G4_SILVER_HALIDES  # scripted group (container) (typed FeaturePython)
  Dunit = g/cm3
  Dvalue = 6.47
  Group = -> [Br_element006,Ag_element004,I_element007]
  conduct = 2
  density = 1
  expand = 3
  formula = G4_SILVER_HALIDES
  name = G4_SILVER_HALIDES
  specific = 4
FEATURE [App::DocumentObjectGroupPython] Ag_element005  label="Ag_element : 003"  # scripted group (container) (typed FeaturePython)
  n = 1
  ref = Ag_element
FEATURE [App::DocumentObjectGroupPython] I_element008  label="I_element : 004"  # scripted group (container) (typed FeaturePython)
  n = 1
  ref = I_element
FEATURE [App::DocumentObjectGroupPython] G4_SILVER_IODIDE  # scripted group (container) (typed FeaturePython)
  Dunit = g/cm3
  Dvalue = 6.01
  Group = -> [Ag_element005,I_element008]
  conduct = 2
  density = 1
  expand = 3
  formula = G4_SILVER_IODIDE
  name = G4_SILVER_IODIDE
  specific = 4
FEATURE [App::DocumentObjectGroupPython] H_element095  label="H_element : 0.100"  # scripted group (container) (typed FeaturePython)
  n = 0.1
FEATURE [App::DocumentObjectGroupPython] C_element103  label="C_element : 0.204"  # scripted group (container) (typed FeaturePython)
  n = 0.204
FEATURE [App::DocumentObjectGroupPython] N_element039  label="N_element : 0.759"  # scripted group (container) (typed FeaturePython)
  n = 0.042
FEATURE [App::DocumentObjectGroupPython] O_element088  label="O_element : 0.645"  # scripted group (container) (typed FeaturePython)
  n = 0.645
FEATURE [App::DocumentObjectGroupPython] Na_element013  label="Na_element : 0.100"  # scripted group (container) (typed FeaturePython)
  n = 0.002
FEATURE [App::DocumentObjectGroupPython] P_element009  label="P_element : 0.107"  # scripted group (container) (typed FeaturePython)
  n = 0.001
FEATURE [App::DocumentObjectGroupPython] S_element020  label="S_element : 0.021"  # scripted group (container) (typed FeaturePython)
  n = 0.002
FEATURE [App::DocumentObjectGroupPython] Cl_element023  label="Cl_element : 0.590"  # scripted group (container) (typed FeaturePython)
  n = 0.003
FEATURE [App::DocumentObjectGroupPython] K_element010  label="K_element : 0.001"  # scripted group (container) (typed FeaturePython)
  n = 0.001
FEATURE [App::DocumentObjectGroupPython] G4_SKIN_ICRP  # scripted group (container) (typed FeaturePython)
  Dunit = g/cm3
  Dvalue = 1.09
  Group = -> [H_element095,C_element103,N_element039,O_element088,Na_element013,P_element009,S_element020,Cl_element023,K_element010]
  conduct = 2
  density = 1
  expand = 3
  formula = G4_SKIN_ICRP
  name = G4_SKIN_ICRP
  specific = 4
FEATURE [App::DocumentObjectGroupPython] Na_element014  label="Na_element : 2"  # scripted group (container) (typed FeaturePython)
  n = 2
  ref = Na_element
FEATURE [App::DocumentObjectGroupPython] C_element104  label="C_element : 058"  # scripted group (container) (typed FeaturePython)
  n = 1
  ref = C_element
FEATURE [App::DocumentObjectGroupPython] O_element089  label="O_element : 049"  # scripted group (container) (typed FeaturePython)
  n = 3
  ref = O_element
FEATURE [App::DocumentObjectGroupPython] G4_SODIUM_CARBONATE  # scripted group (container) (typed FeaturePython)
  Dunit = g/cm3
  Dvalue = 2.532
  Group = -> [Na_element014,C_element104,O_element089]
  conduct = 2
  density = 1
  expand = 3
  formula = G4_SODIUM_CARBONATE
  name = G4_SODIUM_CARBONATE
  specific = 4
FEATURE [App::DocumentObjectGroupPython] Na_element015  label="Na_element : 1"  # scripted group (container) (typed FeaturePython)
  n = 1
  ref = Na_element
FEATURE [App::DocumentObjectGroupPython] I_element009  label="I_element : 005"  # scripted group (container) (typed FeaturePython)
  n = 1
  ref = I_element
FEATURE [App::DocumentObjectGroupPython] G4_SODIUM_IODIDE  # scripted group (container) (typed FeaturePython)
  Dunit = g/cm3
  Dvalue = 3.667
  Group = -> [Na_element015,I_element009]
  conduct = 2
  density = 1
  expand = 3
  formula = G4_SODIUM_IODIDE
  name = G4_SODIUM_IODIDE
  specific = 4
FEATURE [App::DocumentObjectGroupPython] Na_element016  label="Na_element : 003"  # scripted group (container) (typed FeaturePython)
  n = 2
  ref = Na_element
FEATURE [App::DocumentObjectGroupPython] O_element090  label="O_element : 050"  # scripted group (container) (typed FeaturePython)
  n = 1
  ref = O_element
FEATURE [App::DocumentObjectGroupPython] G4_SODIUM_MONOXIDE  # scripted group (container) (typed FeaturePython)
  Dunit = g/cm3
  Dvalue = 2.27
  Group = -> [Na_element016,O_element090]
  conduct = 2
  density = 1
  expand = 3
  formula = G4_SODIUM_MONOXIDE
  name = G4_SODIUM_MONOXIDE
  specific = 4
FEATURE [App::DocumentObjectGroupPython] Na_element017  label="Na_element : 004"  # scripted group (container) (typed FeaturePython)
  n = 1
  ref = Na_element
FEATURE [App::DocumentObjectGroupPython] N_element040  label="N_element : 018"  # scripted group (container) (typed FeaturePython)
  n = 1
  ref = N_element
FEATURE [App::DocumentObjectGroupPython] O_element091  label="O_element : 051"  # scripted group (container) (typed FeaturePython)
  n = 3
  ref = O_element
FEATURE [App::DocumentObjectGroupPython] G4_SODIUM_NITRATE  # scripted group (container) (typed FeaturePython)
  Dunit = g/cm3
  Dvalue = 2.261
  Group = -> [Na_element017,N_element040,O_element091]
  conduct = 2
  density = 1
  expand = 3
  formula = G4_SODIUM_NITRATE
  name = G4_SODIUM_NITRATE
  specific = 4
FEATURE [App::DocumentObjectGroupPython] C_element105  label="C_element : 059"  # scripted group (container) (typed FeaturePython)
  n = 14
  ref = C_element
FEATURE [App::DocumentObjectGroupPython] H_element096  label="H_element : 053"  # scripted group (container) (typed FeaturePython)
  n = 12
  ref = H_element
FEATURE [App::DocumentObjectGroupPython] G4_STILBENE  # scripted group (container) (typed FeaturePython)
  Dunit = g/cm3
  Dvalue = 0.9707
  Group = -> [C_element105,H_element096]
  conduct = 2
  density = 1
  expand = 3
  formula = G4_STILBENE
  name = G4_STILBENE
  specific = 4
FEATURE [App::DocumentObjectGroupPython] C_element106  label="C_element : 12"  # scripted group (container) (typed FeaturePython)
  n = 12
  ref = C_element
FEATURE [App::DocumentObjectGroupPython] H_element097  label="H_element : 22"  # scripted group (container) (typed FeaturePython)
  n = 22
  ref = H_element
FEATURE [App::DocumentObjectGroupPython] O_element092  label="O_element : 11"  # scripted group (container) (typed FeaturePython)
  n = 11
  ref = O_element
FEATURE [App::DocumentObjectGroupPython] G4_SUCROSE  # scripted group (container) (typed FeaturePython)
  Dunit = g/cm3
  Dvalue = 1.5805
  Group = -> [C_element106,H_element097,O_element092]
  conduct = 2
  density = 1
  expand = 3
  formula = G4_SUCROSE
  name = G4_SUCROSE
  specific = 4
FEATURE [App::DocumentObjectGroupPython] C_element107  label="C_element : 18"  # scripted group (container) (typed FeaturePython)
  n = 18
  ref = C_element
FEATURE [App::DocumentObjectGroupPython] H_element098  label="H_element : 054"  # scripted group (container) (typed FeaturePython)
  n = 14
  ref = H_element
FEATURE [App::DocumentObjectGroupPython] G4_TERPHENYL  # scripted group (container) (typed FeaturePython)
  Dunit = g/cm3
  Dvalue = 1.24
  Group = -> [C_element107,H_element098]
  conduct = 2
  density = 1
  expand = 3
  formula = G4_TERPHENYL
  name = G4_TERPHENYL
  specific = 4
FEATURE [App::DocumentObjectGroupPython] H_element099  label="H_element : 0.146"  # scripted group (container) (typed FeaturePython)
  n = 0.106
FEATURE [App::DocumentObjectGroupPython] C_element108  label="C_element : 0.883"  # scripted group (container) (typed FeaturePython)
  n = 0.099
FEATURE [App::DocumentObjectGroupPython] N_element041  label="N_element : 0.020"  # scripted group (container) (typed FeaturePython)
  n = 0.02
FEATURE [App::DocumentObjectGroupPython] O_element093  label="O_element : 0.766"  # scripted group (container) (typed FeaturePython)
  n = 0.766
FEATURE [App::DocumentObjectGroupPython] Na_element018  label="Na_element : 0.101"  # scripted group (container) (typed FeaturePython)
  n = 0.002
FEATURE [App::DocumentObjectGroupPython] P_element010  label="P_element : 0.108"  # scripted group (container) (typed FeaturePython)
  n = 0.001
FEATURE [App::DocumentObjectGroupPython] S_element021  label="S_element : 0.022"  # scripted group (container) (typed FeaturePython)
  n = 0.002
FEATURE [App::DocumentObjectGroupPython] Cl_element024  label="Cl_element : 0.002"  # scripted group (container) (typed FeaturePython)
  n = 0.002
FEATURE [App::DocumentObjectGroupPython] K_element011  label="K_element : 0.017"  # scripted group (container) (typed FeaturePython)
  n = 0.002
FEATURE [App::DocumentObjectGroupPython] G4_TESTIS_ICRP  # scripted group (container) (typed FeaturePython)
  Dunit = g/cm3
  Dvalue = 1.04
  Group = -> [H_element099,C_element108,N_element041,O_element093,Na_element018,P_element010,S_element021,Cl_element024,K_element011]
  conduct = 2
  density = 1
  expand = 3
  formula = G4_TESTIS_ICRP
  name = G4_TESTIS_ICRP
  specific = 4
FEATURE [App::DocumentObjectGroupPython] C_element109  label="C_element : 060"  # scripted group (container) (typed FeaturePython)
  n = 2
  ref = C_element
FEATURE [App::DocumentObjectGroupPython] Cl_element025  label="Cl_element : 012"  # scripted group (container) (typed FeaturePython)
  n = 4
  ref = Cl_element
FEATURE [App::DocumentObjectGroupPython] G4_TETRACHLOROETHYLENE  # scripted group (container) (typed FeaturePython)
  Dunit = g/cm3
  Dvalue = 1.625
  Group = -> [C_element109,Cl_element025]
  conduct = 2
  density = 1
  expand = 3
  formula = G4_TETRACHLOROETHYLENE
  name = G4_TETRACHLOROETHYLENE
  specific = 4
FEATURE [App::DocumentObjectGroupPython] Tl_element001  label="Tl_element : 1"  # scripted group (container) (typed FeaturePython)
  n = 1
  ref = Tl_element
FEATURE [App::DocumentObjectGroupPython] Cl_element026  label="Cl_element : 013"  # scripted group (container) (typed FeaturePython)
  n = 1
  ref = Cl_element
FEATURE [App::DocumentObjectGroupPython] G4_THALLIUM_CHLORIDE  # scripted group (container) (typed FeaturePython)
  Dunit = g/cm3
  Dvalue = 7.004
  Group = -> [Tl_element001,Cl_element026]
  conduct = 2
  density = 1
  expand = 3
  formula = G4_THALLIUM_CHLORIDE
  name = G4_THALLIUM_CHLORIDE
  specific = 4
FEATURE [App::DocumentObjectGroupPython] H_element100  label="H_element : 0.147"  # scripted group (container) (typed FeaturePython)
  n = 0.105
FEATURE [App::DocumentObjectGroupPython] C_element110  label="C_element : 0.256"  # scripted group (container) (typed FeaturePython)
  n = 0.256
FEATURE [App::DocumentObjectGroupPython] N_element042  label="N_element : 0.760"  # scripted group (container) (typed FeaturePython)
  n = 0.027
FEATURE [App::DocumentObjectGroupPython] O_element094  label="O_element : 0.602"  # scripted group (container) (typed FeaturePython)
  n = 0.602
FEATURE [App::DocumentObjectGroupPython] Na_element019  label="Na_element : 0.102"  # scripted group (container) (typed FeaturePython)
  n = 0.001
FEATURE [App::DocumentObjectGroupPython] P_element011  label="P_element : 0.109"  # scripted group (container) (typed FeaturePython)
  n = 0.002
FEATURE [App::DocumentObjectGroupPython] S_element022  label="S_element : 0.023"  # scripted group (container) (typed FeaturePython)
  n = 0.003
FEATURE [App::DocumentObjectGroupPython] Cl_element027  label="Cl_element : 0.591"  # scripted group (container) (typed FeaturePython)
  n = 0.002
FEATURE [App::DocumentObjectGroupPython] K_element012  label="K_element : 0.018"  # scripted group (container) (typed FeaturePython)
  n = 0.002
FEATURE [App::DocumentObjectGroupPython] G4_TISSUE_SOFT_ICRP  # scripted group (container) (typed FeaturePython)
  Dunit = g/cm3
  Dvalue = 1.03
  Group = -> [H_element100,C_element110,N_element042,O_element094,Na_element019,P_element011,S_element022,Cl_element027,K_element012]
  conduct = 2
  density = 1
  expand = 3
  formula = G4_TISSUE_SOFT_ICRP
  name = G4_TISSUE_SOFT_ICRP
  specific = 4
FEATURE [App::DocumentObjectGroupPython] H_element101  label="H_element : 0.148"  # scripted group (container) (typed FeaturePython)
  n = 0.101
FEATURE [App::DocumentObjectGroupPython] C_element111  label="C_element : 0.111"  # scripted group (container) (typed FeaturePython)
  n = 0.111
FEATURE [App::DocumentObjectGroupPython] N_element043  label="N_element : 0.026"  # scripted group (container) (typed FeaturePython)
  n = 0.026
FEATURE [App::DocumentObjectGroupPython] O_element095  label="O_element : 0.762"  # scripted group (container) (typed FeaturePython)
  n = 0.762
FEATURE [App::DocumentObjectGroupPython] G4_TISSUE_SOFT_ICRU_4  label="G4_TISSUE_SOFT_ICRU-4"  # scripted group (container) (typed FeaturePython)
  Dunit = g/cm3
  Dvalue = 1
  Group = -> [H_element101,C_element111,N_element043,O_element095]
  conduct = 2
  density = 1
  expand = 3
  formula = G4_TISSUE_SOFT_ICRU-4
  name = G4_TISSUE_SOFT_ICRU-4
  specific = 4
FEATURE [App::DocumentObjectGroupPython] H_element102  label="H_element : 0.149"  # scripted group (container) (typed FeaturePython)
  n = 0.101869
FEATURE [App::DocumentObjectGroupPython] C_element112  label="C_element : 0.456"  # scripted group (container) (typed FeaturePython)
  n = 0.456179
FEATURE [App::DocumentObjectGroupPython] N_element044  label="N_element : 0.761"  # scripted group (container) (typed FeaturePython)
  n = 0.035172
FEATURE [App::DocumentObjectGroupPython] O_element096  label="O_element : 0.407"  # scripted group (container) (typed FeaturePython)
  n = 0.40678
FEATURE [App::DocumentObjectGroupPython] G4_TISSUE_METHANE  label="G4_TISSUE-METHANE"  # scripted group (container) (typed FeaturePython)
  Dunit = g/cm3
  Dvalue = 0.00106409
  Group = -> [H_element102,C_element112,N_element044,O_element096]
  conduct = 2
  density = 1
  expand = 3
  formula = G4_TISSUE-METHANE
  name = G4_TISSUE-METHANE
  specific = 4
FEATURE [App::DocumentObjectGroupPython] H_element103  label="H_element : 0.103"  # scripted group (container) (typed FeaturePython)
  n = 0.102672
FEATURE [App::DocumentObjectGroupPython] C_element113  label="C_element : 0.569"  # scripted group (container) (typed FeaturePython)
  n = 0.56894
FEATURE [App::DocumentObjectGroupPython] N_element045  label="N_element : 0.762"  # scripted group (container) (typed FeaturePython)
  n = 0.035022
FEATURE [App::DocumentObjectGroupPython] O_element097  label="O_element : 0.293"  # scripted group (container) (typed FeaturePython)
  n = 0.293366
FEATURE [App::DocumentObjectGroupPython] G4_TISSUE_PROPANE  label="G4_TISSUE-PROPANE"  # scripted group (container) (typed FeaturePython)
  Dunit = g/cm3
  Dvalue = 0.00182628
  Group = -> [H_element103,C_element113,N_element045,O_element097]
  conduct = 2
  density = 1
  expand = 3
  formula = G4_TISSUE-PROPANE
  name = G4_TISSUE-PROPANE
  specific = 4
FEATURE [App::DocumentObjectGroupPython] Ti_element003  label="Ti_element : 1"  # scripted group (container) (typed FeaturePython)
  n = 1
  ref = Ti_element
FEATURE [App::DocumentObjectGroupPython] O_element098  label="O_element : 052"  # scripted group (container) (typed FeaturePython)
  n = 2
  ref = O_element
FEATURE [App::DocumentObjectGroupPython] G4_TITANIUM_DIOXIDE  # scripted group (container) (typed FeaturePython)
  Dunit = g/cm3
  Dvalue = 4.26
  Group = -> [Ti_element003,O_element098]
  conduct = 2
  density = 1
  expand = 3
  formula = G4_TITANIUM_DIOXIDE
  name = G4_TITANIUM_DIOXIDE
  specific = 4
FEATURE [App::DocumentObjectGroupPython] C_element114  label="C_element : 061"  # scripted group (container) (typed FeaturePython)
  n = 7
  ref = C_element
FEATURE [App::DocumentObjectGroupPython] H_element104  label="H_element : 055"  # scripted group (container) (typed FeaturePython)
  n = 8
  ref = H_element
FEATURE [App::DocumentObjectGroupPython] G4_TOLUENE  # scripted group (container) (typed FeaturePython)
  Dunit = g/cm3
  Dvalue = 0.8669
  Group = -> [C_element114,H_element104]
  conduct = 2
  density = 1
  expand = 3
  formula = G4_TOLUENE
  name = G4_TOLUENE
  specific = 4
FEATURE [App::DocumentObjectGroupPython] C_element115  label="C_element : 062"  # scripted group (container) (typed FeaturePython)
  n = 2
  ref = C_element
FEATURE [App::DocumentObjectGroupPython] H_element105  label="H_element : 056"  # scripted group (container) (typed FeaturePython)
  n = 1
  ref = H_element
FEATURE [App::DocumentObjectGroupPython] Cl_element028  label="Cl_element : 014"  # scripted group (container) (typed FeaturePython)
  n = 3
  ref = Cl_element
FEATURE [App::DocumentObjectGroupPython] G4_TRICHLOROETHYLENE  # scripted group (container) (typed FeaturePython)
  Dunit = g/cm3
  Dvalue = 1.46
  Group = -> [C_element115,H_element105,Cl_element028]
  conduct = 2
  density = 1
  expand = 3
  formula = G4_TRICHLOROETHYLENE
  name = G4_TRICHLOROETHYLENE
  specific = 4
FEATURE [App::DocumentObjectGroupPython] C_element116  label="C_element : 063"  # scripted group (container) (typed FeaturePython)
  n = 6
  ref = C_element
FEATURE [App::DocumentObjectGroupPython] H_element106  label="H_element : 15"  # scripted group (container) (typed FeaturePython)
  n = 15
  ref = H_element
FEATURE [App::DocumentObjectGroupPython] O_element099  label="O_element : 053"  # scripted group (container) (typed FeaturePython)
  n = 4
  ref = O_element
FEATURE [App::DocumentObjectGroupPython] P_element012  label="P_element : 1"  # scripted group (container) (typed FeaturePython)
  n = 1
  ref = P_element
FEATURE [App::DocumentObjectGroupPython] G4_TRIETHYL_PHOSPHATE  # scripted group (container) (typed FeaturePython)
  Dunit = g/cm3
  Dvalue = 1.07
  Group = -> [C_element116,H_element106,O_element099,P_element012]
  conduct = 2
  density = 1
  expand = 3
  formula = G4_TRIETHYL_PHOSPHATE
  name = G4_TRIETHYL_PHOSPHATE
  specific = 4
FEATURE [App::DocumentObjectGroupPython] W_element003  label="W_element : 003"  # scripted group (container) (typed FeaturePython)
  n = 1
  ref = W_element
FEATURE [App::DocumentObjectGroupPython] F_element017  label="F_element : 6"  # scripted group (container) (typed FeaturePython)
  n = 6
  ref = F_element
FEATURE [App::DocumentObjectGroupPython] G4_TUNGSTEN_HEXAFLUORIDE  # scripted group (container) (typed FeaturePython)
  Dunit = g/cm3
  Dvalue = 2.4
  Group = -> [W_element003,F_element017]
  conduct = 2
  density = 1
  expand = 3
  formula = G4_TUNGSTEN_HEXAFLUORIDE
  name = G4_TUNGSTEN_HEXAFLUORIDE
  specific = 4
FEATURE [App::DocumentObjectGroupPython] U_element001  label="U_element : 1"  # scripted group (container) (typed FeaturePython)
  n = 1
  ref = U_element
FEATURE [App::DocumentObjectGroupPython] C_element117  label="C_element : 064"  # scripted group (container) (typed FeaturePython)
  n = 2
  ref = C_element
FEATURE [App::DocumentObjectGroupPython] G4_URANIUM_DICARBIDE  # scripted group (container) (typed FeaturePython)
  Dunit = g/cm3
  Dvalue = 11.28
  Group = -> [U_element001,C_element117]
  conduct = 2
  density = 1
  expand = 3
  formula = G4_URANIUM_DICARBIDE
  name = G4_URANIUM_DICARBIDE
  specific = 4
FEATURE [App::DocumentObjectGroupPython] U_element002  label="U_element : 002"  # scripted group (container) (typed FeaturePython)
  n = 1
  ref = U_element
FEATURE [App::DocumentObjectGroupPython] C_element118  label="C_element : 065"  # scripted group (container) (typed FeaturePython)
  n = 1
  ref = C_element
FEATURE [App::DocumentObjectGroupPython] G4_URANIUM_MONOCARBIDE  # scripted group (container) (typed FeaturePython)
  Dunit = g/cm3
  Dvalue = 13.63
  Group = -> [U_element002,C_element118]
  conduct = 2
  density = 1
  expand = 3
  formula = G4_URANIUM_MONOCARBIDE
  name = G4_URANIUM_MONOCARBIDE
  specific = 4
FEATURE [App::DocumentObjectGroupPython] U_element003  label="U_element : 003"  # scripted group (container) (typed FeaturePython)
  n = 1
  ref = U_element
FEATURE [App::DocumentObjectGroupPython] O_element100  label="O_element : 054"  # scripted group (container) (typed FeaturePython)
  n = 2
  ref = O_element
FEATURE [App::DocumentObjectGroupPython] G4_URANIUM_OXIDE  # scripted group (container) (typed FeaturePython)
  Dunit = g/cm3
  Dvalue = 10.96
  Group = -> [U_element003,O_element100]
  conduct = 2
  density = 1
  expand = 3
  formula = G4_URANIUM_OXIDE
  name = G4_URANIUM_OXIDE
  specific = 4
FEATURE [App::DocumentObjectGroupPython] C_element119  label="C_element : 066"  # scripted group (container) (typed FeaturePython)
  n = 1
  ref = C_element
FEATURE [App::DocumentObjectGroupPython] H_element107  label="H_element : 057"  # scripted group (container) (typed FeaturePython)
  n = 4
  ref = H_element
FEATURE [App::DocumentObjectGroupPython] N_element046  label="N_element : 019"  # scripted group (container) (typed FeaturePython)
  n = 2
  ref = N_element
FEATURE [App::DocumentObjectGroupPython] O_element101  label="O_element : 055"  # scripted group (container) (typed FeaturePython)
  n = 1
  ref = O_element
FEATURE [App::DocumentObjectGroupPython] G4_UREA  # scripted group (container) (typed FeaturePython)
  Dunit = g/cm3
  Dvalue = 1.323
  Group = -> [C_element119,H_element107,N_element046,O_element101]
  conduct = 2
  density = 1
  expand = 3
  formula = G4_UREA
  name = G4_UREA
  specific = 4
FEATURE [App::DocumentObjectGroupPython] C_element120  label="C_element : 067"  # scripted group (container) (typed FeaturePython)
  n = 5
  ref = C_element
FEATURE [App::DocumentObjectGroupPython] H_element108  label="H_element : 058"  # scripted group (container) (typed FeaturePython)
  n = 11
  ref = H_element
FEATURE [App::DocumentObjectGroupPython] N_element047  label="N_element : 020"  # scripted group (container) (typed FeaturePython)
  n = 1
  ref = N_element
FEATURE [App::DocumentObjectGroupPython] O_element102  label="O_element : 056"  # scripted group (container) (typed FeaturePython)
  n = 2
  ref = O_element
FEATURE [App::DocumentObjectGroupPython] G4_VALINE  # scripted group (container) (typed FeaturePython)
  Dunit = g/cm3
  Dvalue = 1.23
  Group = -> [C_element120,H_element108,N_element047,O_element102]
  conduct = 2
  density = 1
  expand = 3
  formula = G4_VALINE
  name = G4_VALINE
  specific = 4
FEATURE [App::DocumentObjectGroupPython] H_element109  label="H_element : 0.009"  # scripted group (container) (typed FeaturePython)
  n = 0.009417
FEATURE [App::DocumentObjectGroupPython] C_element121  label="C_element : 0.281"  # scripted group (container) (typed FeaturePython)
  n = 0.280555
FEATURE [App::DocumentObjectGroupPython] F_element018  label="F_element : 0.710"  # scripted group (container) (typed FeaturePython)
  n = 0.710028
FEATURE [App::DocumentObjectGroupPython] G4_VITON  # scripted group (container) (typed FeaturePython)
  Dunit = g/cm3
  Dvalue = 1.8
  Group = -> [H_element109,C_element121,F_element018]
  conduct = 2
  density = 1
  expand = 3
  formula = G4_VITON
  name = G4_VITON
  specific = 4
FEATURE [App::DocumentObjectGroupPython] H_element110  label="H_element : 059"  # scripted group (container) (typed FeaturePython)
  n = 2
  ref = H_element
FEATURE [App::DocumentObjectGroupPython] O_element103  label="O_element : 057"  # scripted group (container) (typed FeaturePython)
  n = 1
  ref = O_element
FEATURE [App::DocumentObjectGroupPython] G4_WATER  # scripted group (container) (typed FeaturePython)
  Dunit = g/cm3
  Dvalue = 1
  Group = -> [H_element110,O_element103]
  conduct = 2
  density = 1
  expand = 3
  formula = G4_WATER
  name = G4_WATER
  specific = 4
FEATURE [App::DocumentObjectGroupPython] H_element111  label="H_element : 060"  # scripted group (container) (typed FeaturePython)
  n = 2
  ref = H_element
FEATURE [App::DocumentObjectGroupPython] O_element104  label="O_element : 058"  # scripted group (container) (typed FeaturePython)
  n = 1
  ref = O_element
FEATURE [App::DocumentObjectGroupPython] G4_WATER_VAPOR  # scripted group (container) (typed FeaturePython)
  Dunit = g/cm3
  Dvalue = 0.000756182
  Group = -> [H_element111,O_element104]
  conduct = 2
  density = 1
  expand = 3
  formula = G4_WATER_VAPOR
  name = G4_WATER_VAPOR
  specific = 4
FEATURE [App::DocumentObjectGroupPython] C_element122  label="C_element : 068"  # scripted group (container) (typed FeaturePython)
  n = 8
  ref = C_element
FEATURE [App::DocumentObjectGroupPython] H_element112  label="H_element : 061"  # scripted group (container) (typed FeaturePython)
  n = 10
  ref = H_element
FEATURE [App::DocumentObjectGroupPython] G4_XYLENE  # scripted group (container) (typed FeaturePython)
  Dunit = g/cm3
  Dvalue = 0.87
  Group = -> [C_element122,H_element112]
  conduct = 2
  density = 1
  expand = 3
  formula = G4_XYLENE
  name = G4_XYLENE
  specific = 4
FEATURE [App::DocumentObjectGroupPython] C_element123  label="C_element : 069"  # scripted group (container) (typed FeaturePython)
  n = 1
  ref = C_element
FEATURE [App::DocumentObjectGroupPython] G4_GRAPHITE  # scripted group (container) (typed FeaturePython)
  Dunit = g/cm3
  Dvalue = 2.21
  Group = -> [C_element123]
  conduct = 2
  density = 1
  expand = 3
  formula = G4_GRAPHITE
  name = G4_GRAPHITE
  specific = 4
FEATURE [App::DocumentObjectGroupPython] NIST  # scripted group (container) (typed FeaturePython)
  Group = -> [G4_A_150_TISSUE,G4_ACETONE,G4_ACETYLENE,G4_ADENINE,G4_ADIPOSE_TISSUE_ICRP,G4_AIR,G4_ALANINE,G4_ALUMINUM_OXIDE,G4_AMBER,G4_AMMONIA,G4_ANILINE,G4_ANTHRACENE,G4_B_100_BONE,G4_BAKELITE,G4_BARIUM_FLUORIDE,G4_BARIUM_SULFATE,G4_BENZENE,G4_BERYLLIUM_OXIDE,G4_BGO,G4_BLOOD_ICRP,G4_BONE_COMPACT_ICRU,G4_BONE_CORTICAL_ICRP,G4_BORON_CARBIDE,G4_BORON_OXIDE,G4_BRAIN_ICRP,G4_BUTANE,G4_N_BUTYL_ALCOHOL,G4_C_552,+152 more]
FEATURE [App::DocumentObjectGroupPython] H_element113  label="H_element : 062"  # scripted group (container) (typed FeaturePython)
  n = 1
  ref = H_element
FEATURE [App::DocumentObjectGroupPython] G4_H  # scripted group (container) (typed FeaturePython)
  Dunit = g/cm3
  Dvalue = 8.3748e-05
  Group = -> [H_element113]
  conduct = 2
  density = 1
  expand = 3
  formula = H
  name = G4_H
  specific = 4
FEATURE [App::DocumentObjectGroupPython] He_element001  label="He_element : 1"  # scripted group (container) (typed FeaturePython)
  n = 1
  ref = He_element
FEATURE [App::DocumentObjectGroupPython] G4_He  # scripted group (container) (typed FeaturePython)
  Dunit = g/cm3
  Dvalue = 0.000166322
  Group = -> [He_element001]
  conduct = 2
  density = 1
  expand = 3
  formula = He
  name = G4_He
  specific = 4
FEATURE [App::DocumentObjectGroupPython] Li_element008  label="Li_element : 008"  # scripted group (container) (typed FeaturePython)
  n = 1
  ref = Li_element
FEATURE [App::DocumentObjectGroupPython] G4_Li  # scripted group (container) (typed FeaturePython)
  Dunit = g/cm3
  Dvalue = 0.534
  Group = -> [Li_element008]
  conduct = 2
  density = 1
  expand = 3
  formula = Li
  name = G4_Li
  specific = 4
FEATURE [App::DocumentObjectGroupPython] Be_element002  label="Be_element : 002"  # scripted group (container) (typed FeaturePython)
  n = 1
  ref = Be_element
FEATURE [App::DocumentObjectGroupPython] G4_Be  # scripted group (container) (typed FeaturePython)
  Dunit = g/cm3
  Dvalue = 1.848
  Group = -> [Be_element002]
  conduct = 2
  density = 1
  expand = 3
  formula = Be
  name = G4_Be
  specific = 4
FEATURE [App::DocumentObjectGroupPython] B_element007  label="B_element : 007"  # scripted group (container) (typed FeaturePython)
  n = 1
  ref = B_element
FEATURE [App::DocumentObjectGroupPython] G4_B  # scripted group (container) (typed FeaturePython)
  Dunit = g/cm3
  Dvalue = 2.37
  Group = -> [B_element007]
  conduct = 2
  density = 1
  expand = 3
  formula = B
  name = G4_B
  specific = 4
FEATURE [App::DocumentObjectGroupPython] C_element124  label="C_element : 070"  # scripted group (container) (typed FeaturePython)
  n = 1
  ref = C_element
FEATURE [App::DocumentObjectGroupPython] G4_C  # scripted group (container) (typed FeaturePython)
  Dunit = g/cm3
  Dvalue = 2
  Group = -> [C_element124]
  conduct = 2
  density = 1
  expand = 3
  formula = C
  name = G4_C
  specific = 4
FEATURE [App::DocumentObjectGroupPython] N_element048  label="N_element : 021"  # scripted group (container) (typed FeaturePython)
  n = 1
  ref = N_element
FEATURE [App::DocumentObjectGroupPython] G4_N  # scripted group (container) (typed FeaturePython)
  Dunit = g/cm3
  Dvalue = 0.0011652
  Group = -> [N_element048]
  conduct = 2
  density = 1
  expand = 3
  formula = N
  name = G4_N
  specific = 4
FEATURE [App::DocumentObjectGroupPython] O_element105  label="O_element : 059"  # scripted group (container) (typed FeaturePython)
  n = 1
  ref = O_element
FEATURE [App::DocumentObjectGroupPython] G4_O  # scripted group (container) (typed FeaturePython)
  Dunit = g/cm3
  Dvalue = 0.00133151
  Group = -> [O_element105]
  conduct = 2
  density = 1
  expand = 3
  formula = O
  name = G4_O
  specific = 4
FEATURE [App::DocumentObjectGroupPython] F_element019  label="F_element : 008"  # scripted group (container) (typed FeaturePython)
  n = 1
  ref = F_element
FEATURE [App::DocumentObjectGroupPython] G4_F  # scripted group (container) (typed FeaturePython)
  Dunit = g/cm3
  Dvalue = 0.00158029
  Group = -> [F_element019]
  conduct = 2
  density = 1
  expand = 3
  formula = F
  name = G4_F
  specific = 4
FEATURE [App::DocumentObjectGroupPython] Ne_element001  label="Ne_element : 1"  # scripted group (container) (typed FeaturePython)
  n = 1
  ref = Ne_element
FEATURE [App::DocumentObjectGroupPython] G4_Ne  # scripted group (container) (typed FeaturePython)
  Dunit = g/cm3
  Dvalue = 0.000838505
  Group = -> [Ne_element001]
  conduct = 2
  density = 1
  expand = 3
  formula = Ne
  name = G4_Ne
  specific = 4
FEATURE [App::DocumentObjectGroupPython] Na_element020  label="Na_element : 005"  # scripted group (container) (typed FeaturePython)
  n = 1
  ref = Na_element
FEATURE [App::DocumentObjectGroupPython] G4_Na  # scripted group (container) (typed FeaturePython)
  Dunit = g/cm3
  Dvalue = 0.971
  Group = -> [Na_element020]
  conduct = 2
  density = 1
  expand = 3
  formula = Na
  name = G4_Na
  specific = 4
FEATURE [App::DocumentObjectGroupPython] Mg_element011  label="Mg_element : 005"  # scripted group (container) (typed FeaturePython)
  n = 1
  ref = Mg_element
FEATURE [App::DocumentObjectGroupPython] G4_Mg  # scripted group (container) (typed FeaturePython)
  Dunit = g/cm3
  Dvalue = 1.74
  Group = -> [Mg_element011]
  conduct = 2
  density = 1
  expand = 3
  formula = Mg
  name = G4_Mg
  specific = 4
FEATURE [App::DocumentObjectGroupPython] Al_element004  label="Al_element : 1"  # scripted group (container) (typed FeaturePython)
  n = 1
  ref = Al_element
FEATURE [App::DocumentObjectGroupPython] G4_Al  # scripted group (container) (typed FeaturePython)
  Dunit = g/cm3
  Dvalue = 2.699
  Group = -> [Al_element004]
  conduct = 2
  density = 1
  expand = 3
  formula = Al
  name = G4_Al
  specific = 4
FEATURE [App::DocumentObjectGroupPython] Si_element007  label="Si_element : 002"  # scripted group (container) (typed FeaturePython)
  n = 1
  ref = Si_element
FEATURE [App::DocumentObjectGroupPython] G4_Si  # scripted group (container) (typed FeaturePython)
  Dunit = g/cm3
  Dvalue = 2.33
  Group = -> [Si_element007]
  conduct = 2
  density = 1
  expand = 3
  formula = Si
  name = G4_Si
  specific = 4
FEATURE [App::DocumentObjectGroupPython] P_element013  label="P_element : 002"  # scripted group (container) (typed FeaturePython)
  n = 1
  ref = P_element
FEATURE [App::DocumentObjectGroupPython] G4_P  # scripted group (container) (typed FeaturePython)
  Dunit = g/cm3
  Dvalue = 2.2
  Group = -> [P_element013]
  conduct = 2
  density = 1
  expand = 3
  formula = P
  name = G4_P
  specific = 4
FEATURE [App::DocumentObjectGroupPython] S_element023  label="S_element : 007"  # scripted group (container) (typed FeaturePython)
  n = 1
  ref = S_element
FEATURE [App::DocumentObjectGroupPython] G4_S  # scripted group (container) (typed FeaturePython)
  Dunit = g/cm3
  Dvalue = 2
  Group = -> [S_element023]
  conduct = 2
  density = 1
  expand = 3
  formula = S
  name = G4_S
  specific = 4
FEATURE [App::DocumentObjectGroupPython] Cl_element029  label="Cl_element : 015"  # scripted group (container) (typed FeaturePython)
  n = 1
  ref = Cl_element
FEATURE [App::DocumentObjectGroupPython] G4_Cl  # scripted group (container) (typed FeaturePython)
  Dunit = g/cm3
  Dvalue = 0.00299473
  Group = -> [Cl_element029]
  conduct = 2
  density = 1
  expand = 3
  formula = Cl
  name = G4_Cl
  specific = 4
FEATURE [App::DocumentObjectGroupPython] Ar_element002  label="Ar_element : 1"  # scripted group (container) (typed FeaturePython)
  n = 1
  ref = Ar_element
FEATURE [App::DocumentObjectGroupPython] G4_Ar  # scripted group (container) (typed FeaturePython)
  Dunit = g/cm3
  Dvalue = 0.00166201
  Group = -> [Ar_element002]
  conduct = 2
  density = 1
  expand = 3
  formula = Ar
  name = G4_Ar
  specific = 4
FEATURE [App::DocumentObjectGroupPython] K_element013  label="K_element : 003"  # scripted group (container) (typed FeaturePython)
  n = 1
  ref = K_element
FEATURE [App::DocumentObjectGroupPython] G4_K  # scripted group (container) (typed FeaturePython)
  Dunit = g/cm3
  Dvalue = 0.862
  Group = -> [K_element013]
  conduct = 2
  density = 1
  expand = 3
  formula = K
  name = G4_K
  specific = 4
FEATURE [App::DocumentObjectGroupPython] Ca_element014  label="Ca_element : 007"  # scripted group (container) (typed FeaturePython)
  n = 1
  ref = Ca_element
FEATURE [App::DocumentObjectGroupPython] G4_Ca  # scripted group (container) (typed FeaturePython)
  Dunit = g/cm3
  Dvalue = 1.55
  Group = -> [Ca_element014]
  conduct = 2
  density = 1
  expand = 3
  formula = Ca
  name = G4_Ca
  specific = 4
FEATURE [App::DocumentObjectGroupPython] Sc_element001  label="Sc_element : 1"  # scripted group (container) (typed FeaturePython)
  n = 1
  ref = Sc_element
FEATURE [App::DocumentObjectGroupPython] G4_Sc  # scripted group (container) (typed FeaturePython)
  Dunit = g/cm3
  Dvalue = 2.989
  Group = -> [Sc_element001]
  conduct = 2
  density = 1
  expand = 3
  formula = Sc
  name = G4_Sc
  specific = 4
FEATURE [App::DocumentObjectGroupPython] Ti_element004  label="Ti_element : 002"  # scripted group (container) (typed FeaturePython)
  n = 1
  ref = Ti_element
FEATURE [App::DocumentObjectGroupPython] G4_Ti  # scripted group (container) (typed FeaturePython)
  Dunit = g/cm3
  Dvalue = 4.54
  Group = -> [Ti_element004]
  conduct = 2
  density = 1
  expand = 3
  formula = Ti
  name = G4_Ti
  specific = 4
FEATURE [App::DocumentObjectGroupPython] V_element001  label="V_element : 1"  # scripted group (container) (typed FeaturePython)
  n = 1
  ref = V_element
FEATURE [App::DocumentObjectGroupPython] G4_V  # scripted group (container) (typed FeaturePython)
  Dunit = g/cm3
  Dvalue = 6.11
  Group = -> [V_element001]
  conduct = 2
  density = 1
  expand = 3
  formula = V
  name = G4_V
  specific = 4
FEATURE [App::DocumentObjectGroupPython] Cr_element001  label="Cr_element : 1"  # scripted group (container) (typed FeaturePython)
  n = 1
  ref = Cr_element
FEATURE [App::DocumentObjectGroupPython] G4_Cr  # scripted group (container) (typed FeaturePython)
  Dunit = g/cm3
  Dvalue = 7.18
  Group = -> [Cr_element001]
  conduct = 2
  density = 1
  expand = 3
  formula = Cr
  name = G4_Cr
  specific = 4
FEATURE [App::DocumentObjectGroupPython] Mn_element001  label="Mn_element : 1"  # scripted group (container) (typed FeaturePython)
  n = 1
  ref = Mn_element
FEATURE [App::DocumentObjectGroupPython] G4_Mn  # scripted group (container) (typed FeaturePython)
  Dunit = g/cm3
  Dvalue = 7.44
  Group = -> [Mn_element001]
  conduct = 2
  density = 1
  expand = 3
  formula = Mn
  name = G4_Mn
  specific = 4
FEATURE [App::DocumentObjectGroupPython] Fe_element007  label="Fe_element : 004"  # scripted group (container) (typed FeaturePython)
  n = 1
  ref = Fe_element
FEATURE [App::DocumentObjectGroupPython] G4_Fe  # scripted group (container) (typed FeaturePython)
  Dunit = g/cm3
  Dvalue = 7.874
  Group = -> [Fe_element007]
  conduct = 2
  density = 1
  expand = 3
  formula = Fe
  name = G4_Fe
  specific = 4
FEATURE [App::DocumentObjectGroupPython] Co_element001  label="Co_element : 1"  # scripted group (container) (typed FeaturePython)
  n = 1
  ref = Co_element
FEATURE [App::DocumentObjectGroupPython] G4_Co  # scripted group (container) (typed FeaturePython)
  Dunit = g/cm3
  Dvalue = 8.9
  Group = -> [Co_element001]
  conduct = 2
  density = 1
  expand = 3
  formula = Co
  name = G4_Co
  specific = 4
FEATURE [App::DocumentObjectGroupPython] Ni_element001  label="Ni_element : 1"  # scripted group (container) (typed FeaturePython)
  n = 1
  ref = Ni_element
FEATURE [App::DocumentObjectGroupPython] G4_Ni  # scripted group (container) (typed FeaturePython)
  Dunit = g/cm3
  Dvalue = 8.902
  Group = -> [Ni_element001]
  conduct = 2
  density = 1
  expand = 3
  formula = Ni
  name = G4_Ni
  specific = 4
FEATURE [App::DocumentObjectGroupPython] Cu_element001  label="Cu_element : 1"  # scripted group (container) (typed FeaturePython)
  n = 1
  ref = Cu_element
FEATURE [App::DocumentObjectGroupPython] G4_Cu  # scripted group (container) (typed FeaturePython)
  Dunit = g/cm3
  Dvalue = 8.96
  Group = -> [Cu_element001]
  conduct = 2
  density = 1
  expand = 3
  formula = Cu
  name = G4_Cu
  specific = 4
FEATURE [App::DocumentObjectGroupPython] Zn_element001  label="Zn_element : 1"  # scripted group (container) (typed FeaturePython)
  n = 1
  ref = Zn_element
FEATURE [App::DocumentObjectGroupPython] G4_Zn  # scripted group (container) (typed FeaturePython)
  Dunit = g/cm3
  Dvalue = 7.133
  Group = -> [Zn_element001]
  conduct = 2
  density = 1
  expand = 3
  formula = Zn
  name = G4_Zn
  specific = 4
FEATURE [App::DocumentObjectGroupPython] Ga_element002  label="Ga_element : 002"  # scripted group (container) (typed FeaturePython)
  n = 1
  ref = Ga_element
FEATURE [App::DocumentObjectGroupPython] G4_Ga  # scripted group (container) (typed FeaturePython)
  Dunit = g/cm3
  Dvalue = 5.904
  Group = -> [Ga_element002]
  conduct = 2
  density = 1
  expand = 3
  formula = Ga
  name = G4_Ga
  specific = 4
FEATURE [App::DocumentObjectGroupPython] Ge_element002  label="Ge_element : 1"  # scripted group (container) (typed FeaturePython)
  n = 1
  ref = Ge_element
FEATURE [App::DocumentObjectGroupPython] G4_Ge  # scripted group (container) (typed FeaturePython)
  Dunit = g/cm3
  Dvalue = 5.323
  Group = -> [Ge_element002]
  conduct = 2
  density = 1
  expand = 3
  formula = Ge
  name = G4_Ge
  specific = 4
FEATURE [App::DocumentObjectGroupPython] As_element003  label="As_element : 002"  # scripted group (container) (typed FeaturePython)
  n = 1
  ref = As_element
FEATURE [App::DocumentObjectGroupPython] G4_As  # scripted group (container) (typed FeaturePython)
  Dunit = g/cm3
  Dvalue = 5.73
  Group = -> [As_element003]
  conduct = 2
  density = 1
  expand = 3
  formula = As
  name = G4_As
  specific = 4
FEATURE [App::DocumentObjectGroupPython] Se_element001  label="Se_element : 1"  # scripted group (container) (typed FeaturePython)
  n = 1
  ref = Se_element
FEATURE [App::DocumentObjectGroupPython] G4_Se  # scripted group (container) (typed FeaturePython)
  Dunit = g/cm3
  Dvalue = 4.5
  Group = -> [Se_element001]
  conduct = 2
  density = 1
  expand = 3
  formula = Se
  name = G4_Se
  specific = 4
FEATURE [App::DocumentObjectGroupPython] Br_element007  label="Br_element : 004"  # scripted group (container) (typed FeaturePython)
  n = 1
  ref = Br_element
FEATURE [App::DocumentObjectGroupPython] G4_Br  # scripted group (container) (typed FeaturePython)
  Dunit = g/cm3
  Dvalue = 0.0070721
  Group = -> [Br_element007]
  conduct = 2
  density = 1
  expand = 3
  formula = Br
  name = G4_Br
  specific = 4
FEATURE [App::DocumentObjectGroupPython] Kr_element001  label="Kr_element : 1"  # scripted group (container) (typed FeaturePython)
  n = 1
  ref = Kr_element
FEATURE [App::DocumentObjectGroupPython] G4_Kr  # scripted group (container) (typed FeaturePython)
  Dunit = g/cm3
  Dvalue = 0.00347832
  Group = -> [Kr_element001]
  conduct = 2
  density = 1
  expand = 3
  formula = Kr
  name = G4_Kr
  specific = 4
FEATURE [App::DocumentObjectGroupPython] Rb_element001  label="Rb_element : 1"  # scripted group (container) (typed FeaturePython)
  n = 1
  ref = Rb_element
FEATURE [App::DocumentObjectGroupPython] G4_Rb  # scripted group (container) (typed FeaturePython)
  Dunit = g/cm3
  Dvalue = 1.532
  Group = -> [Rb_element001]
  conduct = 2
  density = 1
  expand = 3
  formula = Rb
  name = G4_Rb
  specific = 4
FEATURE [App::DocumentObjectGroupPython] Sr_element001  label="Sr_element : 1"  # scripted group (container) (typed FeaturePython)
  n = 1
  ref = Sr_element
FEATURE [App::DocumentObjectGroupPython] G4_Sr  # scripted group (container) (typed FeaturePython)
  Dunit = g/cm3
  Dvalue = 2.54
  Group = -> [Sr_element001]
  conduct = 2
  density = 1
  expand = 3
  formula = Sr
  name = G4_Sr
  specific = 4
FEATURE [App::DocumentObjectGroupPython] Y_element001  label="Y_element : 1"  # scripted group (container) (typed FeaturePython)
  n = 1
  ref = Y_element
FEATURE [App::DocumentObjectGroupPython] G4_Y  # scripted group (container) (typed FeaturePython)
  Dunit = g/cm3
  Dvalue = 4.469
  Group = -> [Y_element001]
  conduct = 2
  density = 1
  expand = 3
  formula = Y
  name = G4_Y
  specific = 4
FEATURE [App::DocumentObjectGroupPython] Zr_element001  label="Zr_element : 1"  # scripted group (container) (typed FeaturePython)
  n = 1
  ref = Zr_element
FEATURE [App::DocumentObjectGroupPython] G4_Zr  # scripted group (container) (typed FeaturePython)
  Dunit = g/cm3
  Dvalue = 6.506
  Group = -> [Zr_element001]
  conduct = 2
  density = 1
  expand = 3
  formula = Zr
  name = G4_Zr
  specific = 4
FEATURE [App::DocumentObjectGroupPython] Nb_element001  label="Nb_element : 1"  # scripted group (container) (typed FeaturePython)
  n = 1
  ref = Nb_element
FEATURE [App::DocumentObjectGroupPython] G4_Nb  # scripted group (container) (typed FeaturePython)
  Dunit = g/cm3
  Dvalue = 8.57
  Group = -> [Nb_element001]
  conduct = 2
  density = 1
  expand = 3
  formula = Nb
  name = G4_Nb
  specific = 4
FEATURE [App::DocumentObjectGroupPython] Mo_element001  label="Mo_element : 1"  # scripted group (container) (typed FeaturePython)
  n = 1
  ref = Mo_element
FEATURE [App::DocumentObjectGroupPython] G4_Mo  # scripted group (container) (typed FeaturePython)
  Dunit = g/cm3
  Dvalue = 10.22
  Group = -> [Mo_element001]
  conduct = 2
  density = 1
  expand = 3
  formula = Mo
  name = G4_Mo
  specific = 4
FEATURE [App::DocumentObjectGroupPython] Tc_element001  label="Tc_element : 1"  # scripted group (container) (typed FeaturePython)
  n = 1
  ref = Tc_element
FEATURE [App::DocumentObjectGroupPython] G4_Tc  # scripted group (container) (typed FeaturePython)
  Dunit = g/cm3
  Dvalue = 11.5
  Group = -> [Tc_element001]
  conduct = 2
  density = 1
  expand = 3
  formula = Tc
  name = G4_Tc
  specific = 4
FEATURE [App::DocumentObjectGroupPython] Ru_element001  label="Ru_element : 1"  # scripted group (container) (typed FeaturePython)
  n = 1
  ref = Ru_element
FEATURE [App::DocumentObjectGroupPython] G4_Ru  # scripted group (container) (typed FeaturePython)
  Dunit = g/cm3
  Dvalue = 12.41
  Group = -> [Ru_element001]
  conduct = 2
  density = 1
  expand = 3
  formula = Ru
  name = G4_Ru
  specific = 4
FEATURE [App::DocumentObjectGroupPython] Rh_element001  label="Rh_element : 1"  # scripted group (container) (typed FeaturePython)
  n = 1
  ref = Rh_element
FEATURE [App::DocumentObjectGroupPython] G4_Rh  # scripted group (container) (typed FeaturePython)
  Dunit = g/cm3
  Dvalue = 12.41
  Group = -> [Rh_element001]
  conduct = 2
  density = 1
  expand = 3
  formula = Rh
  name = G4_Rh
  specific = 4
FEATURE [App::DocumentObjectGroupPython] Pd_element001  label="Pd_element : 1"  # scripted group (container) (typed FeaturePython)
  n = 1
  ref = Pd_element
FEATURE [App::DocumentObjectGroupPython] G4_Pd  # scripted group (container) (typed FeaturePython)
  Dunit = g/cm3
  Dvalue = 12.02
  Group = -> [Pd_element001]
  conduct = 2
  density = 1
  expand = 3
  formula = Pd
  name = G4_Pd
  specific = 4
FEATURE [App::DocumentObjectGroupPython] Ag_element006  label="Ag_element : 004"  # scripted group (container) (typed FeaturePython)
  n = 1
  ref = Ag_element
FEATURE [App::DocumentObjectGroupPython] G4_Ag  # scripted group (container) (typed FeaturePython)
  Dunit = g/cm3
  Dvalue = 10.5
  Group = -> [Ag_element006]
  conduct = 2
  density = 1
  expand = 3
  formula = Ag
  name = G4_Ag
  specific = 4
FEATURE [App::DocumentObjectGroupPython] Cd_element003  label="Cd_element : 003"  # scripted group (container) (typed FeaturePython)
  n = 1
  ref = Cd_element
FEATURE [App::DocumentObjectGroupPython] G4_Cd  # scripted group (container) (typed FeaturePython)
  Dunit = g/cm3
  Dvalue = 8.65
  Group = -> [Cd_element003]
  conduct = 2
  density = 1
  expand = 3
  formula = Cd
  name = G4_Cd
  specific = 4
FEATURE [App::DocumentObjectGroupPython] In_element001  label="In_element : 1"  # scripted group (container) (typed FeaturePython)
  n = 1
  ref = In_element
FEATURE [App::DocumentObjectGroupPython] G4_In  # scripted group (container) (typed FeaturePython)
  Dunit = g/cm3
  Dvalue = 7.31
  Group = -> [In_element001]
  conduct = 2
  density = 1
  expand = 3
  formula = In
  name = G4_In
  specific = 4
FEATURE [App::DocumentObjectGroupPython] Sn_element001  label="Sn_element : 1"  # scripted group (container) (typed FeaturePython)
  n = 1
  ref = Sn_element
FEATURE [App::DocumentObjectGroupPython] G4_Sn  # scripted group (container) (typed FeaturePython)
  Dunit = g/cm3
  Dvalue = 7.31
  Group = -> [Sn_element001]
  conduct = 2
  density = 1
  expand = 3
  formula = Sn
  name = G4_Sn
  specific = 4
FEATURE [App::DocumentObjectGroupPython] Sb_element001  label="Sb_element : 1"  # scripted group (container) (typed FeaturePython)
  n = 1
  ref = Sb_element
FEATURE [App::DocumentObjectGroupPython] G4_Sb  # scripted group (container) (typed FeaturePython)
  Dunit = g/cm3
  Dvalue = 6.691
  Group = -> [Sb_element001]
  conduct = 2
  density = 1
  expand = 3
  formula = Sb
  name = G4_Sb
  specific = 4
FEATURE [App::DocumentObjectGroupPython] Te_element002  label="Te_element : 002"  # scripted group (container) (typed FeaturePython)
  n = 1
  ref = Te_element
FEATURE [App::DocumentObjectGroupPython] G4_Te  # scripted group (container) (typed FeaturePython)
  Dunit = g/cm3
  Dvalue = 6.24
  Group = -> [Te_element002]
  conduct = 2
  density = 1
  expand = 3
  formula = Te
  name = G4_Te
  specific = 4
FEATURE [App::DocumentObjectGroupPython] I_element010  label="I_element : 006"  # scripted group (container) (typed FeaturePython)
  n = 1
  ref = I_element
FEATURE [App::DocumentObjectGroupPython] G4_I  # scripted group (container) (typed FeaturePython)
  Dunit = g/cm3
  Dvalue = 4.93
  Group = -> [I_element010]
  conduct = 2
  density = 1
  expand = 3
  formula = I
  name = G4_I
  specific = 4
FEATURE [App::DocumentObjectGroupPython] Xe_element001  label="Xe_element : 1"  # scripted group (container) (typed FeaturePython)
  n = 1
  ref = Xe_element
FEATURE [App::DocumentObjectGroupPython] G4_Xe  # scripted group (container) (typed FeaturePython)
  Dunit = g/cm3
  Dvalue = 0.00548536
  Group = -> [Xe_element001]
  conduct = 2
  density = 1
  expand = 3
  formula = Xe
  name = G4_Xe
  specific = 4
FEATURE [App::DocumentObjectGroupPython] Cs_element003  label="Cs_element : 003"  # scripted group (container) (typed FeaturePython)
  n = 1
  ref = Cs_element
FEATURE [App::DocumentObjectGroupPython] G4_Cs  # scripted group (container) (typed FeaturePython)
  Dunit = g/cm3
  Dvalue = 1.873
  Group = -> [Cs_element003]
  conduct = 2
  density = 1
  expand = 3
  formula = Cs
  name = G4_Cs
  specific = 4
FEATURE [App::DocumentObjectGroupPython] Ba_element003  label="Ba_element : 003"  # scripted group (container) (typed FeaturePython)
  n = 1
  ref = Ba_element
FEATURE [App::DocumentObjectGroupPython] G4_Ba  # scripted group (container) (typed FeaturePython)
  Dunit = g/cm3
  Dvalue = 3.5
  Group = -> [Ba_element003]
  conduct = 2
  density = 1
  expand = 3
  formula = Ba
  name = G4_Ba
  specific = 4
FEATURE [App::DocumentObjectGroupPython] La_element003  label="La_element : 003"  # scripted group (container) (typed FeaturePython)
  n = 1
  ref = La_element
FEATURE [App::DocumentObjectGroupPython] G4_La  # scripted group (container) (typed FeaturePython)
  Dunit = g/cm3
  Dvalue = 6.154
  Group = -> [La_element003]
  conduct = 2
  density = 1
  expand = 3
  formula = La
  name = G4_La
  specific = 4
FEATURE [App::DocumentObjectGroupPython] Ce_element002  label="Ce_element : 1"  # scripted group (container) (typed FeaturePython)
  n = 1
  ref = Ce_element
FEATURE [App::DocumentObjectGroupPython] G4_Ce  # scripted group (container) (typed FeaturePython)
  Dunit = g/cm3
  Dvalue = 6.657
  Group = -> [Ce_element002]
  conduct = 2
  density = 1
  expand = 3
  formula = Ce
  name = G4_Ce
  specific = 4
FEATURE [App::DocumentObjectGroupPython] Pr_element001  label="Pr_element : 1"  # scripted group (container) (typed FeaturePython)
  n = 1
  ref = Pr_element
FEATURE [App::DocumentObjectGroupPython] G4_Pr  # scripted group (container) (typed FeaturePython)
  Dunit = g/cm3
  Dvalue = 6.71
  Group = -> [Pr_element001]
  conduct = 2
  density = 1
  expand = 3
  formula = Pr
  name = G4_Pr
  specific = 4
FEATURE [App::DocumentObjectGroupPython] Nd_element001  label="Nd_element : 1"  # scripted group (container) (typed FeaturePython)
  n = 1
  ref = Nd_element
FEATURE [App::DocumentObjectGroupPython] G4_Nd  # scripted group (container) (typed FeaturePython)
  Dunit = g/cm3
  Dvalue = 6.9
  Group = -> [Nd_element001]
  conduct = 2
  density = 1
  expand = 3
  formula = Nd
  name = G4_Nd
  specific = 4
FEATURE [App::DocumentObjectGroupPython] Pm_element001  label="Pm_element : 1"  # scripted group (container) (typed FeaturePython)
  n = 1
  ref = Pm_element
FEATURE [App::DocumentObjectGroupPython] G4_Pm  # scripted group (container) (typed FeaturePython)
  Dunit = g/cm3
  Dvalue = 7.22
  Group = -> [Pm_element001]
  conduct = 2
  density = 1
  expand = 3
  formula = Pm
  name = G4_Pm
  specific = 4
FEATURE [App::DocumentObjectGroupPython] Sm_element001  label="Sm_element : 1"  # scripted group (container) (typed FeaturePython)
  n = 1
  ref = Sm_element
FEATURE [App::DocumentObjectGroupPython] G4_Sm  # scripted group (container) (typed FeaturePython)
  Dunit = g/cm3
  Dvalue = 7.46
  Group = -> [Sm_element001]
  conduct = 2
  density = 1
  expand = 3
  formula = Sm
  name = G4_Sm
  specific = 4
FEATURE [App::DocumentObjectGroupPython] Eu_element001  label="Eu_element : 1"  # scripted group (container) (typed FeaturePython)
  n = 1
  ref = Eu_element
FEATURE [App::DocumentObjectGroupPython] G4_Eu  # scripted group (container) (typed FeaturePython)
  Dunit = g/cm3
  Dvalue = 5.243
  Group = -> [Eu_element001]
  conduct = 2
  density = 1
  expand = 3
  formula = Eu
  name = G4_Eu
  specific = 4
FEATURE [App::DocumentObjectGroupPython] Gd_element002  label="Gd_element : 1"  # scripted group (container) (typed FeaturePython)
  n = 1
  ref = Gd_element
FEATURE [App::DocumentObjectGroupPython] G4_Gd  # scripted group (container) (typed FeaturePython)
  Dunit = g/cm3
  Dvalue = 7.9004
  Group = -> [Gd_element002]
  conduct = 2
  density = 1
  expand = 3
  formula = Gd
  name = G4_Gd
  specific = 4
FEATURE [App::DocumentObjectGroupPython] Tb_element001  label="Tb_element : 1"  # scripted group (container) (typed FeaturePython)
  n = 1
  ref = Tb_element
FEATURE [App::DocumentObjectGroupPython] G4_Tb  # scripted group (container) (typed FeaturePython)
  Dunit = g/cm3
  Dvalue = 8.229
  Group = -> [Tb_element001]
  conduct = 2
  density = 1
  expand = 3
  formula = Tb
  name = G4_Tb
  specific = 4
FEATURE [App::DocumentObjectGroupPython] Dy_element001  label="Dy_element : 1"  # scripted group (container) (typed FeaturePython)
  n = 1
  ref = Dy_element
FEATURE [App::DocumentObjectGroupPython] G4_Dy  # scripted group (container) (typed FeaturePython)
  Dunit = g/cm3
  Dvalue = 8.55
  Group = -> [Dy_element001]
  conduct = 2
  density = 1
  expand = 3
  formula = Dy
  name = G4_Dy
  specific = 4
FEATURE [App::DocumentObjectGroupPython] Ho_element001  label="Ho_element : 1"  # scripted group (container) (typed FeaturePython)
  n = 1
  ref = Ho_element
FEATURE [App::DocumentObjectGroupPython] G4_Ho  # scripted group (container) (typed FeaturePython)
  Dunit = g/cm3
  Dvalue = 8.795
  Group = -> [Ho_element001]
  conduct = 2
  density = 1
  expand = 3
  formula = Ho
  name = G4_Ho
  specific = 4
FEATURE [App::DocumentObjectGroupPython] Er_element001  label="Er_element : 1"  # scripted group (container) (typed FeaturePython)
  n = 1
  ref = Er_element
FEATURE [App::DocumentObjectGroupPython] G4_Er  # scripted group (container) (typed FeaturePython)
  Dunit = g/cm3
  Dvalue = 9.066
  Group = -> [Er_element001]
  conduct = 2
  density = 1
  expand = 3
  formula = Er
  name = G4_Er
  specific = 4
FEATURE [App::DocumentObjectGroupPython] Tm_element001  label="Tm_element : 1"  # scripted group (container) (typed FeaturePython)
  n = 1
  ref = Tm_element
FEATURE [App::DocumentObjectGroupPython] G4_Tm  # scripted group (container) (typed FeaturePython)
  Dunit = g/cm3
  Dvalue = 9.321
  Group = -> [Tm_element001]
  conduct = 2
  density = 1
  expand = 3
  formula = Tm
  name = G4_Tm
  specific = 4
FEATURE [App::DocumentObjectGroupPython] Yb_element001  label="Yb_element : 1"  # scripted group (container) (typed FeaturePython)
  n = 1
  ref = Yb_element
FEATURE [App::DocumentObjectGroupPython] G4_Yb  # scripted group (container) (typed FeaturePython)
  Dunit = g/cm3
  Dvalue = 6.73
  Group = -> [Yb_element001]
  conduct = 2
  density = 1
  expand = 3
  formula = Yb
  name = G4_Yb
  specific = 4
FEATURE [App::DocumentObjectGroupPython] Lu_element001  label="Lu_element : 1"  # scripted group (container) (typed FeaturePython)
  n = 1
  ref = Lu_element
FEATURE [App::DocumentObjectGroupPython] G4_Lu  # scripted group (container) (typed FeaturePython)
  Dunit = g/cm3
  Dvalue = 9.84
  Group = -> [Lu_element001]
  conduct = 2
  density = 1
  expand = 3
  formula = Lu
  name = G4_Lu
  specific = 4
FEATURE [App::DocumentObjectGroupPython] Hf_element001  label="Hf_element : 1"  # scripted group (container) (typed FeaturePython)
  n = 1
  ref = Hf_element
FEATURE [App::DocumentObjectGroupPython] G4_Hf  # scripted group (container) (typed FeaturePython)
  Dunit = g/cm3
  Dvalue = 13.31
  Group = -> [Hf_element001]
  conduct = 2
  density = 1
  expand = 3
  formula = Hf
  name = G4_Hf
  specific = 4
FEATURE [App::DocumentObjectGroupPython] Ta_element001  label="Ta_element : 1"  # scripted group (container) (typed FeaturePython)
  n = 1
  ref = Ta_element
FEATURE [App::DocumentObjectGroupPython] G4_Ta  # scripted group (container) (typed FeaturePython)
  Dunit = g/cm3
  Dvalue = 16.654
  Group = -> [Ta_element001]
  conduct = 2
  density = 1
  expand = 3
  formula = Ta
  name = G4_Ta
  specific = 4
FEATURE [App::DocumentObjectGroupPython] W_element004  label="W_element : 004"  # scripted group (container) (typed FeaturePython)
  n = 1
  ref = W_element
FEATURE [App::DocumentObjectGroupPython] G4_W  # scripted group (container) (typed FeaturePython)
  Dunit = g/cm3
  Dvalue = 19.3
  Group = -> [W_element004]
  conduct = 2
  density = 1
  expand = 3
  formula = W
  name = G4_W
  specific = 4
FEATURE [App::DocumentObjectGroupPython] Re_element001  label="Re_element : 1"  # scripted group (container) (typed FeaturePython)
  n = 1
  ref = Re_element
FEATURE [App::DocumentObjectGroupPython] G4_Re  # scripted group (container) (typed FeaturePython)
  Dunit = g/cm3
  Dvalue = 21.02
  Group = -> [Re_element001]
  conduct = 2
  density = 1
  expand = 3
  formula = Re
  name = G4_Re
  specific = 4
FEATURE [App::DocumentObjectGroupPython] Os_element001  label="Os_element : 1"  # scripted group (container) (typed FeaturePython)
  n = 1
  ref = Os_element
FEATURE [App::DocumentObjectGroupPython] G4_Os  # scripted group (container) (typed FeaturePython)
  Dunit = g/cm3
  Dvalue = 22.57
  Group = -> [Os_element001]
  conduct = 2
  density = 1
  expand = 3
  formula = Os
  name = G4_Os
  specific = 4
FEATURE [App::DocumentObjectGroupPython] Ir_element001  label="Ir_element : 1"  # scripted group (container) (typed FeaturePython)
  n = 1
  ref = Ir_element
FEATURE [App::DocumentObjectGroupPython] G4_Ir  # scripted group (container) (typed FeaturePython)
  Dunit = g/cm3
  Dvalue = 22.42
  Group = -> [Ir_element001]
  conduct = 2
  density = 1
  expand = 3
  formula = Ir
  name = G4_Ir
  specific = 4
FEATURE [App::DocumentObjectGroupPython] Pt_element001  label="Pt_element : 1"  # scripted group (container) (typed FeaturePython)
  n = 1
  ref = Pt_element
FEATURE [App::DocumentObjectGroupPython] G4_Pt  # scripted group (container) (typed FeaturePython)
  Dunit = g/cm3
  Dvalue = 21.45
  Group = -> [Pt_element001]
  conduct = 2
  density = 1
  expand = 3
  formula = Pt
  name = G4_Pt
  specific = 4
FEATURE [App::DocumentObjectGroupPython] Au_element001  label="Au_element : 1"  # scripted group (container) (typed FeaturePython)
  n = 1
  ref = Au_element
FEATURE [App::DocumentObjectGroupPython] G4_Au  # scripted group (container) (typed FeaturePython)
  Dunit = g/cm3
  Dvalue = 19.32
  Group = -> [Au_element001]
  conduct = 2
  density = 1
  expand = 3
  formula = Au
  name = G4_Au
  specific = 4
FEATURE [App::DocumentObjectGroupPython] Hg_element002  label="Hg_element : 002"  # scripted group (container) (typed FeaturePython)
  n = 1
  ref = Hg_element
FEATURE [App::DocumentObjectGroupPython] G4_Hg  # scripted group (container) (typed FeaturePython)
  Dunit = g/cm3
  Dvalue = 13.546
  Group = -> [Hg_element002]
  conduct = 2
  density = 1
  expand = 3
  formula = Hg
  name = G4_Hg
  specific = 4
FEATURE [App::DocumentObjectGroupPython] Tl_element002  label="Tl_element : 002"  # scripted group (container) (typed FeaturePython)
  n = 1
  ref = Tl_element
FEATURE [App::DocumentObjectGroupPython] G4_Tl  # scripted group (container) (typed FeaturePython)
  Dunit = g/cm3
  Dvalue = 11.72
  Group = -> [Tl_element002]
  conduct = 2
  density = 1
  expand = 3
  formula = Tl
  name = G4_Tl
  specific = 4
FEATURE [App::DocumentObjectGroupPython] Pb_element003  label="Pb_element : 1"  # scripted group (container) (typed FeaturePython)
  n = 1
  ref = Pb_element
FEATURE [App::DocumentObjectGroupPython] G4_Pb  # scripted group (container) (typed FeaturePython)
  Dunit = g/cm3
  Dvalue = 11.35
  Group = -> [Pb_element003]
  conduct = 2
  density = 1
  expand = 3
  formula = Pb
  name = G4_Pb
  specific = 4
FEATURE [App::DocumentObjectGroupPython] Bi_element002  label="Bi_element : 1"  # scripted group (container) (typed FeaturePython)
  n = 1
  ref = Bi_element
FEATURE [App::DocumentObjectGroupPython] G4_Bi  # scripted group (container) (typed FeaturePython)
  Dunit = g/cm3
  Dvalue = 9.747
  Group = -> [Bi_element002]
  conduct = 2
  density = 1
  expand = 3
  formula = Bi
  name = G4_Bi
  specific = 4
FEATURE [App::DocumentObjectGroupPython] Po_element001  label="Po_element : 1"  # scripted group (container) (typed FeaturePython)
  n = 1
  ref = Po_element
FEATURE [App::DocumentObjectGroupPython] G4_Po  # scripted group (container) (typed FeaturePython)
  Dunit = g/cm3
  Dvalue = 9.32
  Group = -> [Po_element001]
  conduct = 2
  density = 1
  expand = 3
  formula = Po
  name = G4_Po
  specific = 4
FEATURE [App::DocumentObjectGroupPython] At_element001  label="At_element : 1"  # scripted group (container) (typed FeaturePython)
  n = 1
  ref = At_element
FEATURE [App::DocumentObjectGroupPython] G4_At  # scripted group (container) (typed FeaturePython)
  Dunit = g/cm3
  Dvalue = 9.32
  Group = -> [At_element001]
  conduct = 2
  density = 1
  expand = 3
  formula = At
  name = G4_At
  specific = 4
FEATURE [App::DocumentObjectGroupPython] Rn_element001  label="Rn_element : 1"  # scripted group (container) (typed FeaturePython)
  n = 1
  ref = Rn_element
FEATURE [App::DocumentObjectGroupPython] G4_Rn  # scripted group (container) (typed FeaturePython)
  Dunit = g/cm3
  Dvalue = 0.00900662
  Group = -> [Rn_element001]
  conduct = 2
  density = 1
  expand = 3
  formula = Rn
  name = G4_Rn
  specific = 4
FEATURE [App::DocumentObjectGroupPython] Fr_element001  label="Fr_element : 1"  # scripted group (container) (typed FeaturePython)
  n = 1
  ref = Fr_element
FEATURE [App::DocumentObjectGroupPython] G4_Fr  # scripted group (container) (typed FeaturePython)
  Dunit = g/cm3
  Dvalue = 1
  Group = -> [Fr_element001]
  conduct = 2
  density = 1
  expand = 3
  formula = Fr
  name = G4_Fr
  specific = 4
FEATURE [App::DocumentObjectGroupPython] Ra_element001  label="Ra_element : 1"  # scripted group (container) (typed FeaturePython)
  n = 1
  ref = Ra_element
FEATURE [App::DocumentObjectGroupPython] G4_Ra  # scripted group (container) (typed FeaturePython)
  Dunit = g/cm3
  Dvalue = 5
  Group = -> [Ra_element001]
  conduct = 2
  density = 1
  expand = 3
  formula = Ra
  name = G4_Ra
  specific = 4
FEATURE [App::DocumentObjectGroupPython] Ac_element001  label="Ac_element : 1"  # scripted group (container) (typed FeaturePython)
  n = 1
  ref = Ac_element
FEATURE [App::DocumentObjectGroupPython] G4_Ac  # scripted group (container) (typed FeaturePython)
  Dunit = g/cm3
  Dvalue = 10.07
  Group = -> [Ac_element001]
  conduct = 2
  density = 1
  expand = 3
  formula = Ac
  name = G4_Ac
  specific = 4
FEATURE [App::DocumentObjectGroupPython] Th_element001  label="Th_element : 1"  # scripted group (container) (typed FeaturePython)
  n = 1
  ref = Th_element
FEATURE [App::DocumentObjectGroupPython] G4_Th  # scripted group (container) (typed FeaturePython)
  Dunit = g/cm3
  Dvalue = 11.72
  Group = -> [Th_element001]
  conduct = 2
  density = 1
  expand = 3
  formula = Th
  name = G4_Th
  specific = 4
FEATURE [App::DocumentObjectGroupPython] Pa_element001  label="Pa_element : 1"  # scripted group (container) (typed FeaturePython)
  n = 1
  ref = Pa_element
FEATURE [App::DocumentObjectGroupPython] G4_Pa  # scripted group (container) (typed FeaturePython)
  Dunit = g/cm3
  Dvalue = 15.37
  Group = -> [Pa_element001]
  conduct = 2
  density = 1
  expand = 3
  formula = Pa
  name = G4_Pa
  specific = 4
FEATURE [App::DocumentObjectGroupPython] U_element004  label="U_element : 004"  # scripted group (container) (typed FeaturePython)
  n = 1
  ref = U_element
FEATURE [App::DocumentObjectGroupPython] G4_U  # scripted group (container) (typed FeaturePython)
  Dunit = g/cm3
  Dvalue = 18.95
  Group = -> [U_element004]
  conduct = 2
  density = 1
  expand = 3
  formula = U
  name = G4_U
  specific = 4
FEATURE [App::DocumentObjectGroupPython] Np_element001  label="Np_element : 1"  # scripted group (container) (typed FeaturePython)
  n = 1
  ref = Np_element
FEATURE [App::DocumentObjectGroupPython] G4_Np  # scripted group (container) (typed FeaturePython)
  Dunit = g/cm3
  Dvalue = 20.25
  Group = -> [Np_element001]
  conduct = 2
  density = 1
  expand = 3
  formula = Np
  name = G4_Np
  specific = 4
FEATURE [App::DocumentObjectGroupPython] Pu_element002  label="Pu_element : 002"  # scripted group (container) (typed FeaturePython)
  n = 1
  ref = Pu_element
FEATURE [App::DocumentObjectGroupPython] G4_Pu  # scripted group (container) (typed FeaturePython)
  Dunit = g/cm3
  Dvalue = 19.84
  Group = -> [Pu_element002]
  conduct = 2
  density = 1
  expand = 3
  formula = Pu
  name = G4_Pu
  specific = 4
FEATURE [App::DocumentObjectGroupPython] Am_element001  label="Am_element : 1"  # scripted group (container) (typed FeaturePython)
  n = 1
  ref = Am_element
FEATURE [App::DocumentObjectGroupPython] G4_Am  # scripted group (container) (typed FeaturePython)
  Dunit = g/cm3
  Dvalue = 13.67
  Group = -> [Am_element001]
  conduct = 2
  density = 1
  expand = 3
  formula = Am
  name = G4_Am
  specific = 4
FEATURE [App::DocumentObjectGroupPython] Cm_element001  label="Cm_element : 1"  # scripted group (container) (typed FeaturePython)
  n = 1
  ref = Cm_element
FEATURE [App::DocumentObjectGroupPython] G4_Cm  # scripted group (container) (typed FeaturePython)
  Dunit = g/cm3
  Dvalue = 13.51
  Group = -> [Cm_element001]
  conduct = 2
  density = 1
  expand = 3
  formula = Cm
  name = G4_Cm
  specific = 4
FEATURE [App::DocumentObjectGroupPython] Bk_element001  label="Bk_element : 1"  # scripted group (container) (typed FeaturePython)
  n = 1
  ref = Bk_element
FEATURE [App::DocumentObjectGroupPython] G4_Bk  # scripted group (container) (typed FeaturePython)
  Dunit = g/cm3
  Dvalue = 14
  Group = -> [Bk_element001]
  conduct = 2
  density = 1
  expand = 3
  formula = Bk
  name = G4_Bk
  specific = 4
FEATURE [App::DocumentObjectGroupPython] Cf_element001  label="Cf_element : 1"  # scripted group (container) (typed FeaturePython)
  n = 1
  ref = Cf_element
FEATURE [App::DocumentObjectGroupPython] G4_Cf  # scripted group (container) (typed FeaturePython)
  Dunit = g/cm3
  Dvalue = 10
  Group = -> [Cf_element001]
  conduct = 2
  density = 1
  expand = 3
  formula = Cf
  name = G4_Cf
  specific = 4
FEATURE [App::DocumentObjectGroupPython] Element  # scripted group (container) (typed FeaturePython)
  Group = -> [G4_H,G4_He,G4_Li,G4_Be,G4_B,G4_C,G4_N,G4_O,G4_F,G4_Ne,G4_Na,G4_Mg,G4_Al,G4_Si,G4_P,G4_S,G4_Cl,G4_Ar,G4_K,G4_Ca,G4_Sc,G4_Ti,G4_V,G4_Cr,G4_Mn,G4_Fe,G4_Co,G4_Ni,G4_Cu,G4_Zn,G4_Ga,G4_Ge,G4_As,G4_Se,G4_Br,G4_Kr,G4_Rb,G4_Sr,G4_Y,G4_Zr,G4_Nb,G4_Mo,G4_Tc,G4_Ru,G4_Rh,G4_Pd,G4_Ag,G4_Cd,G4_In,G4_Sn,G4_Sb,G4_Te,G4_I,G4_Xe,G4_Cs,G4_Ba,G4_La,G4_Ce,G4_Pr,G4_Nd,G4_Pm,G4_Sm,G4_Eu,G4_Gd,G4_Tb,G4_Dy,G4_Ho,G4_Er,+30 more]
FEATURE [App::DocumentObjectGroupPython] H_element114  label="H_element : 063"  # scripted group (container) (typed FeaturePython)
  n = 2
  ref = H_element
FEATURE [App::DocumentObjectGroupPython] G4_lH2  # scripted group (container) (typed FeaturePython)
  Dunit = g/cm3
  Dvalue = 0.0708
  Group = -> [H_element114]
  conduct = 2
  density = 1
  expand = 3
  formula = G4_lH2
  name = G4_lH2
  specific = 4
FEATURE [App::DocumentObjectGroupPython] N_element049  label="N_element : 022"  # scripted group (container) (typed FeaturePython)
  n = 2
  ref = N_element
FEATURE [App::DocumentObjectGroupPython] G4_lN2  # scripted group (container) (typed FeaturePython)
  Dunit = g/cm3
  Dvalue = 0.807
  Group = -> [N_element049]
  conduct = 2
  density = 1
  expand = 3
  formula = G4_lN2
  name = G4_lN2
  specific = 4
FEATURE [App::DocumentObjectGroupPython] O_element106  label="O_element : 060"  # scripted group (container) (typed FeaturePython)
  n = 2
  ref = O_element
FEATURE [App::DocumentObjectGroupPython] G4_lO2  # scripted group (container) (typed FeaturePython)
  Dunit = g/cm3
  Dvalue = 1.141
  Group = -> [O_element106]
  conduct = 2
  density = 1
  expand = 3
  formula = G4_lO2
  name = G4_lO2
  specific = 4
FEATURE [App::DocumentObjectGroupPython] Ar_element003  label="Ar_element : 002"  # scripted group (container) (typed FeaturePython)
  n = 1
  ref = Ar_element
FEATURE [App::DocumentObjectGroupPython] G4_lAr  # scripted group (container) (typed FeaturePython)
  Dunit = g/cm3
  Dvalue = 1.396
  Group = -> [Ar_element003]
  conduct = 2
  density = 1
  expand = 3
  formula = G4_lAr
  name = G4_lAr
  specific = 4
FEATURE [App::DocumentObjectGroupPython] Br_element008  label="Br_element : 005"  # scripted group (container) (typed FeaturePython)
  n = 1
  ref = Br_element
FEATURE [App::DocumentObjectGroupPython] G4_lBr  # scripted group (container) (typed FeaturePython)
  Dunit = g/cm3
  Dvalue = 3.1028
  Group = -> [Br_element008]
  conduct = 2
  density = 1
  expand = 3
  formula = G4_lBr
  name = G4_lBr
  specific = 4
FEATURE [App::DocumentObjectGroupPython] Kr_element002  label="Kr_element : 002"  # scripted group (container) (typed FeaturePython)
  n = 1
  ref = Kr_element
FEATURE [App::DocumentObjectGroupPython] G4_lKr  # scripted group (container) (typed FeaturePython)
  Dunit = g/cm3
  Dvalue = 2.418
  Group = -> [Kr_element002]
  conduct = 2
  density = 1
  expand = 3
  formula = G4_lKr
  name = G4_lKr
  specific = 4
FEATURE [App::DocumentObjectGroupPython] Xe_element002  label="Xe_element : 002"  # scripted group (container) (typed FeaturePython)
  n = 1
  ref = Xe_element
FEATURE [App::DocumentObjectGroupPython] G4_lXe  # scripted group (container) (typed FeaturePython)
  Dunit = g/cm3
  Dvalue = 2.953
  Group = -> [Xe_element002]
  conduct = 2
  density = 1
  expand = 3
  formula = G4_lXe
  name = G4_lXe
  specific = 4
FEATURE [App::DocumentObjectGroupPython] O_element107  label="O_element : 061"  # scripted group (container) (typed FeaturePython)
  n = 4
  ref = O_element
FEATURE [App::DocumentObjectGroupPython] Pb_element004  label="Pb_element : 002"  # scripted group (container) (typed FeaturePython)
  n = 1
  ref = Pb_element
FEATURE [App::DocumentObjectGroupPython] W_element005  label="W_element : 005"  # scripted group (container) (typed FeaturePython)
  n = 1
  ref = W_element
FEATURE [App::DocumentObjectGroupPython] G4_PbWO4  # scripted group (container) (typed FeaturePython)
  Dunit = g/cm3
  Dvalue = 8.28
  Group = -> [O_element107,Pb_element004,W_element005]
  conduct = 2
  density = 1
  expand = 3
  formula = G4_PbWO4
  name = G4_PbWO4
  specific = 4
FEATURE [App::DocumentObjectGroupPython] H_element115  label="H_element : 064"  # scripted group (container) (typed FeaturePython)
  n = 1
  ref = H_element
FEATURE [App::DocumentObjectGroupPython] G4_Galactic  # scripted group (container) (typed FeaturePython)
  Dunit = g/cm3
  Dvalue = 0
  Group = -> [H_element115]
  conduct = 2
  density = 1
  expand = 3
  formula = G4_Galactic
  name = G4_Galactic
  specific = 4
FEATURE [App::DocumentObjectGroupPython] C_element125  label="C_element : 071"  # scripted group (container) (typed FeaturePython)
  n = 1
  ref = C_element
FEATURE [App::DocumentObjectGroupPython] G4_GRAPHITE_POROUS  # scripted group (container) (typed FeaturePython)
  Dunit = g/cm3
  Dvalue = 1.7
  Group = -> [C_element125]
  conduct = 2
  density = 1
  expand = 3
  formula = G4_GRAPHITE_POROUS
  name = G4_GRAPHITE_POROUS
  specific = 4
FEATURE [App::DocumentObjectGroupPython] H_element116  label="H_element : 0.150"  # scripted group (container) (typed FeaturePython)
  n = 0.080538
FEATURE [App::DocumentObjectGroupPython] C_element126  label="C_element : 0.600"  # scripted group (container) (typed FeaturePython)
  n = 0.599848
FEATURE [App::DocumentObjectGroupPython] O_element108  label="O_element : 0.320"  # scripted group (container) (typed FeaturePython)
  n = 0.319614
FEATURE [App::DocumentObjectGroupPython] G4_LUCITE  # scripted group (container) (typed FeaturePython)
  Dunit = g/cm3
  Dvalue = 1.19
  Group = -> [H_element116,C_element126,O_element108]
  conduct = 2
  density = 1
  expand = 3
  formula = G4_LUCITE
  name = G4_LUCITE
  specific = 4
FEATURE [App::DocumentObjectGroupPython] Cu_element002  label="Cu_element : 62"  # scripted group (container) (typed FeaturePython)
  n = 62
  ref = Cu_element
FEATURE [App::DocumentObjectGroupPython] Zn_element002  label="Zn_element : 35"  # scripted group (container) (typed FeaturePython)
  n = 35
  ref = Zn_element
FEATURE [App::DocumentObjectGroupPython] Pb_element005  label="Pb_element : 3"  # scripted group (container) (typed FeaturePython)
  n = 3
  ref = Pb_element
FEATURE [App::DocumentObjectGroupPython] G4_BRASS  # scripted group (container) (typed FeaturePython)
  Dunit = g/cm3
  Dvalue = 8.52
  Group = -> [Cu_element002,Zn_element002,Pb_element005]
  conduct = 2
  density = 1
  expand = 3
  formula = G4_BRASS
  name = G4_BRASS
  specific = 4
FEATURE [App::DocumentObjectGroupPython] Cu_element003  label="Cu_element : 89"  # scripted group (container) (typed FeaturePython)
  n = 89
  ref = Cu_element
FEATURE [App::DocumentObjectGroupPython] Zn_element003  label="Zn_element : 9"  # scripted group (container) (typed FeaturePython)
  n = 9
  ref = Zn_element
FEATURE [App::DocumentObjectGroupPython] Pb_element006  label="Pb_element : 2"  # scripted group (container) (typed FeaturePython)
  n = 2
  ref = Pb_element
FEATURE [App::DocumentObjectGroupPython] G4_BRONZE  # scripted group (container) (typed FeaturePython)
  Dunit = g/cm3
  Dvalue = 8.82
  Group = -> [Cu_element003,Zn_element003,Pb_element006]
  conduct = 2
  density = 1
  expand = 3
  formula = G4_BRONZE
  name = G4_BRONZE
  specific = 4
FEATURE [App::DocumentObjectGroupPython] Fe_element008  label="Fe_element : 74"  # scripted group (container) (typed FeaturePython)
  n = 74
  ref = Fe_element
FEATURE [App::DocumentObjectGroupPython] Cr_element002  label="Cr_element : 18"  # scripted group (container) (typed FeaturePython)
  n = 18
  ref = Cr_element
FEATURE [App::DocumentObjectGroupPython] Ni_element002  label="Ni_element : 8"  # scripted group (container) (typed FeaturePython)
  n = 8
  ref = Ni_element
FEATURE [App::DocumentObjectGroupPython] G4_STAINLESS_STEEL  label="G4_STAINLESS-STEEL"  # scripted group (container) (typed FeaturePython)
  Dunit = g/cm3
  Dvalue = 8
  Group = -> [Fe_element008,Cr_element002,Ni_element002]
  conduct = 2
  density = 1
  expand = 3
  formula = G4_STAINLESS-STEEL
  name = G4_STAINLESS-STEEL
  specific = 4
FEATURE [App::DocumentObjectGroupPython] H_element117  label="H_element : 065"  # scripted group (container) (typed FeaturePython)
  n = 18
  ref = H_element
FEATURE [App::DocumentObjectGroupPython] C_element127  label="C_element : 072"  # scripted group (container) (typed FeaturePython)
  n = 12
  ref = C_element
FEATURE [App::DocumentObjectGroupPython] O_element109  label="O_element : 062"  # scripted group (container) (typed FeaturePython)
  n = 7
  ref = O_element
FEATURE [App::DocumentObjectGroupPython] G4_CR39  # scripted group (container) (typed FeaturePython)
  Dunit = g/cm3
  Dvalue = 1.32
  Group = -> [H_element117,C_element127,O_element109]
  conduct = 2
  density = 1
  expand = 3
  formula = G4_CR39
  name = G4_CR39
  specific = 4
FEATURE [App::DocumentObjectGroupPython] H_element118  label="H_element : 38"  # scripted group (container) (typed FeaturePython)
  n = 38
  ref = H_element
FEATURE [App::DocumentObjectGroupPython] C_element128  label="C_element : 073"  # scripted group (container) (typed FeaturePython)
  n = 18
  ref = C_element
FEATURE [App::DocumentObjectGroupPython] O_element110  label="O_element : 063"  # scripted group (container) (typed FeaturePython)
  n = 1
  ref = O_element
FEATURE [App::DocumentObjectGroupPython] G4_OCTADECANOL  # scripted group (container) (typed FeaturePython)
  Dunit = g/cm3
  Dvalue = 0.812
  Group = -> [H_element118,C_element128,O_element110]
  conduct = 2
  density = 1
  expand = 3
  formula = G4_OCTADECANOL
  name = G4_OCTADECANOL
  specific = 4
FEATURE [App::DocumentObjectGroupPython] HEP  # scripted group (container) (typed FeaturePython)
  Group = -> [G4_lH2,G4_lN2,G4_lO2,G4_lAr,G4_lBr,G4_lKr,G4_lXe,G4_PbWO4,G4_Galactic,G4_GRAPHITE_POROUS,G4_LUCITE,G4_BRASS,G4_BRONZE,G4_STAINLESS_STEEL,G4_CR39,G4_OCTADECANOL]
FEATURE [App::DocumentObjectGroupPython] C_element129  label="C_element : 074"  # scripted group (container) (typed FeaturePython)
  n = 14
  ref = C_element
FEATURE [App::DocumentObjectGroupPython] H_element119  label="H_element : 066"  # scripted group (container) (typed FeaturePython)
  n = 10
  ref = H_element
FEATURE [App::DocumentObjectGroupPython] O_element111  label="O_element : 064"  # scripted group (container) (typed FeaturePython)
  n = 2
  ref = O_element
FEATURE [App::DocumentObjectGroupPython] N_element050  label="N_element : 023"  # scripted group (container) (typed FeaturePython)
  n = 2
  ref = N_element
FEATURE [App::DocumentObjectGroupPython] G4_KEVLAR  # scripted group (container) (typed FeaturePython)
  Dunit = g/cm3
  Dvalue = 1.44
  Group = -> [C_element129,H_element119,O_element111,N_element050]
  conduct = 2
  density = 1
  expand = 3
  formula = G4_KEVLAR
  name = G4_KEVLAR
  specific = 4
FEATURE [App::DocumentObjectGroupPython] C_element130  label="C_element : 075"  # scripted group (container) (typed FeaturePython)
  n = 10
  ref = C_element
FEATURE [App::DocumentObjectGroupPython] H_element120  label="H_element : 067"  # scripted group (container) (typed FeaturePython)
  n = 8
  ref = H_element
FEATURE [App::DocumentObjectGroupPython] O_element112  label="O_element : 065"  # scripted group (container) (typed FeaturePython)
  n = 4
  ref = O_element
FEATURE [App::DocumentObjectGroupPython] G4_DACRON  # scripted group (container) (typed FeaturePython)
  Dunit = g/cm3
  Dvalue = 1.4
  Group = -> [C_element130,H_element120,O_element112]
  conduct = 2
  density = 1
  expand = 3
  formula = G4_DACRON
  name = G4_DACRON
  specific = 4
FEATURE [App::DocumentObjectGroupPython] C_element131  label="C_element : 076"  # scripted group (container) (typed FeaturePython)
  n = 4
  ref = C_element
FEATURE [App::DocumentObjectGroupPython] H_element121  label="H_element : 068"  # scripted group (container) (typed FeaturePython)
  n = 5
  ref = H_element
FEATURE [App::DocumentObjectGroupPython] Cl_element030  label="Cl_element : 016"  # scripted group (container) (typed FeaturePython)
  n = 1
  ref = Cl_element
FEATURE [App::DocumentObjectGroupPython] G4_NEOPRENE  # scripted group (container) (typed FeaturePython)
  Dunit = g/cm3
  Dvalue = 1.23
  Group = -> [C_element131,H_element121,Cl_element030]
  conduct = 2
  density = 1
  expand = 3
  formula = G4_NEOPRENE
  name = G4_NEOPRENE
  specific = 4
FEATURE [App::DocumentObjectGroupPython] Space  # scripted group (container) (typed FeaturePython)
  Group = -> [G4_KEVLAR,G4_DACRON,G4_NEOPRENE]
FEATURE [App::DocumentObjectGroupPython] H_element122  label="H_element : 069"  # scripted group (container) (typed FeaturePython)
  n = 5
  ref = H_element
FEATURE [App::DocumentObjectGroupPython] C_element132  label="C_element : 077"  # scripted group (container) (typed FeaturePython)
  n = 4
  ref = C_element
FEATURE [App::DocumentObjectGroupPython] N_element051  label="N_element : 3"  # scripted group (container) (typed FeaturePython)
  n = 3
  ref = N_element
FEATURE [App::DocumentObjectGroupPython] O_element113  label="O_element : 066"  # scripted group (container) (typed FeaturePython)
  n = 1
  ref = O_element
FEATURE [App::DocumentObjectGroupPython] G4_CYTOSINE  # scripted group (container) (typed FeaturePython)
  Dunit = g/cm3
  Dvalue = 1.55
  Group = -> [H_element122,C_element132,N_element051,O_element113]
  conduct = 2
  density = 1
  expand = 3
  formula = G4_CYTOSINE
  name = G4_CYTOSINE
  specific = 4
FEATURE [App::DocumentObjectGroupPython] H_element123  label="H_element : 070"  # scripted group (container) (typed FeaturePython)
  n = 6
  ref = H_element
FEATURE [App::DocumentObjectGroupPython] C_element133  label="C_element : 078"  # scripted group (container) (typed FeaturePython)
  n = 5
  ref = C_element
FEATURE [App::DocumentObjectGroupPython] N_element052  label="N_element : 024"  # scripted group (container) (typed FeaturePython)
  n = 2
  ref = N_element
FEATURE [App::DocumentObjectGroupPython] O_element114  label="O_element : 067"  # scripted group (container) (typed FeaturePython)
  n = 2
  ref = O_element
FEATURE [App::DocumentObjectGroupPython] G4_THYMINE  # scripted group (container) (typed FeaturePython)
  Dunit = g/cm3
  Dvalue = 1.23
  Group = -> [H_element123,C_element133,N_element052,O_element114]
  conduct = 2
  density = 1
  expand = 3
  formula = G4_THYMINE
  name = G4_THYMINE
  specific = 4
FEATURE [App::DocumentObjectGroupPython] H_element124  label="H_element : 071"  # scripted group (container) (typed FeaturePython)
  n = 4
  ref = H_element
FEATURE [App::DocumentObjectGroupPython] C_element134  label="C_element : 079"  # scripted group (container) (typed FeaturePython)
  n = 4
  ref = C_element
FEATURE [App::DocumentObjectGroupPython] N_element053  label="N_element : 025"  # scripted group (container) (typed FeaturePython)
  n = 2
  ref = N_element
FEATURE [App::DocumentObjectGroupPython] O_element115  label="O_element : 068"  # scripted group (container) (typed FeaturePython)
  n = 2
  ref = O_element
FEATURE [App::DocumentObjectGroupPython] G4_URACIL  # scripted group (container) (typed FeaturePython)
  Dunit = g/cm3
  Dvalue = 1.32
  Group = -> [H_element124,C_element134,N_element053,O_element115]
  conduct = 2
  density = 1
  expand = 3
  formula = G4_URACIL
  name = G4_URACIL
  specific = 4
FEATURE [App::DocumentObjectGroupPython] H_element125  label="H_element : 072"  # scripted group (container) (typed FeaturePython)
  n = 4
  ref = H_element
FEATURE [App::DocumentObjectGroupPython] C_element135  label="C_element : 080"  # scripted group (container) (typed FeaturePython)
  n = 5
  ref = C_element
FEATURE [App::DocumentObjectGroupPython] N_element054  label="N_element : 026"  # scripted group (container) (typed FeaturePython)
  n = 5
  ref = N_element
FEATURE [App::DocumentObjectGroupPython] G4_DNA_ADENINE  # scripted group (container) (typed FeaturePython)
  Dunit = g/cm3
  Dvalue = 1
  Group = -> [H_element125,C_element135,N_element054]
  conduct = 2
  density = 1
  expand = 3
  formula = G4_DNA_ADENINE
  name = G4_DNA_ADENINE
  specific = 4
FEATURE [App::DocumentObjectGroupPython] H_element126  label="H_element : 073"  # scripted group (container) (typed FeaturePython)
  n = 4
  ref = H_element
FEATURE [App::DocumentObjectGroupPython] C_element136  label="C_element : 081"  # scripted group (container) (typed FeaturePython)
  n = 5
  ref = C_element
FEATURE [App::DocumentObjectGroupPython] N_element055  label="N_element : 027"  # scripted group (container) (typed FeaturePython)
  n = 5
  ref = N_element
FEATURE [App::DocumentObjectGroupPython] O_element116  label="O_element : 069"  # scripted group (container) (typed FeaturePython)
  n = 1
  ref = O_element
FEATURE [App::DocumentObjectGroupPython] G4_DNA_GUANINE  # scripted group (container) (typed FeaturePython)
  Dunit = g/cm3
  Dvalue = 1
  Group = -> [H_element126,C_element136,N_element055,O_element116]
  conduct = 2
  density = 1
  expand = 3
  formula = G4_DNA_GUANINE
  name = G4_DNA_GUANINE
  specific = 4
FEATURE [App::DocumentObjectGroupPython] H_element127  label="H_element : 074"  # scripted group (container) (typed FeaturePython)
  n = 4
  ref = H_element
FEATURE [App::DocumentObjectGroupPython] C_element137  label="C_element : 082"  # scripted group (container) (typed FeaturePython)
  n = 4
  ref = C_element
FEATURE [App::DocumentObjectGroupPython] N_element056  label="N_element : 028"  # scripted group (container) (typed FeaturePython)
  n = 3
  ref = N_element
FEATURE [App::DocumentObjectGroupPython] O_element117  label="O_element : 070"  # scripted group (container) (typed FeaturePython)
  n = 1
  ref = O_element
FEATURE [App::DocumentObjectGroupPython] G4_DNA_CYTOSINE  # scripted group (container) (typed FeaturePython)
  Dunit = g/cm3
  Dvalue = 1
  Group = -> [H_element127,C_element137,N_element056,O_element117]
  conduct = 2
  density = 1
  expand = 3
  formula = G4_DNA_CYTOSINE
  name = G4_DNA_CYTOSINE
  specific = 4
FEATURE [App::DocumentObjectGroupPython] H_element128  label="H_element : 075"  # scripted group (container) (typed FeaturePython)
  n = 5
  ref = H_element
FEATURE [App::DocumentObjectGroupPython] C_element138  label="C_element : 083"  # scripted group (container) (typed FeaturePython)
  n = 5
  ref = C_element
FEATURE [App::DocumentObjectGroupPython] N_element057  label="N_element : 029"  # scripted group (container) (typed FeaturePython)
  n = 2
  ref = N_element
FEATURE [App::DocumentObjectGroupPython] O_element118  label="O_element : 071"  # scripted group (container) (typed FeaturePython)
  n = 2
  ref = O_element
FEATURE [App::DocumentObjectGroupPython] G4_DNA_THYMINE  # scripted group (container) (typed FeaturePython)
  Dunit = g/cm3
  Dvalue = 1
  Group = -> [H_element128,C_element138,N_element057,O_element118]
  conduct = 2
  density = 1
  expand = 3
  formula = G4_DNA_THYMINE
  name = G4_DNA_THYMINE
  specific = 4
FEATURE [App::DocumentObjectGroupPython] H_element129  label="H_element : 076"  # scripted group (container) (typed FeaturePython)
  n = 3
  ref = H_element
FEATURE [App::DocumentObjectGroupPython] C_element139  label="C_element : 084"  # scripted group (container) (typed FeaturePython)
  n = 4
  ref = C_element
FEATURE [App::DocumentObjectGroupPython] N_element058  label="N_element : 030"  # scripted group (container) (typed FeaturePython)
  n = 2
  ref = N_element
FEATURE [App::DocumentObjectGroupPython] O_element119  label="O_element : 072"  # scripted group (container) (typed FeaturePython)
  n = 2
  ref = O_element
FEATURE [App::DocumentObjectGroupPython] G4_DNA_URACIL  # scripted group (container) (typed FeaturePython)
  Dunit = g/cm3
  Dvalue = 1
  Group = -> [H_element129,C_element139,N_element058,O_element119]
  conduct = 2
  density = 1
  expand = 3
  formula = G4_DNA_URACIL
  name = G4_DNA_URACIL
  specific = 4
FEATURE [App::DocumentObjectGroupPython] H_element130  label="H_element : 077"  # scripted group (container) (typed FeaturePython)
  n = 10
  ref = H_element
FEATURE [App::DocumentObjectGroupPython] C_element140  label="C_element : 085"  # scripted group (container) (typed FeaturePython)
  n = 10
  ref = C_element
FEATURE [App::DocumentObjectGroupPython] N_element059  label="N_element : 031"  # scripted group (container) (typed FeaturePython)
  n = 5
  ref = N_element
FEATURE [App::DocumentObjectGroupPython] O_element120  label="O_element : 073"  # scripted group (container) (typed FeaturePython)
  n = 4
  ref = O_element
FEATURE [App::DocumentObjectGroupPython] G4_DNA_ADENOSINE  # scripted group (container) (typed FeaturePython)
  Dunit = g/cm3
  Dvalue = 1
  Group = -> [H_element130,C_element140,N_element059,O_element120]
  conduct = 2
  density = 1
  expand = 3
  formula = G4_DNA_ADENOSINE
  name = G4_DNA_ADENOSINE
  specific = 4
FEATURE [App::DocumentObjectGroupPython] H_element131  label="H_element : 078"  # scripted group (container) (typed FeaturePython)
  n = 10
  ref = H_element
FEATURE [App::DocumentObjectGroupPython] C_element141  label="C_element : 086"  # scripted group (container) (typed FeaturePython)
  n = 10
  ref = C_element
FEATURE [App::DocumentObjectGroupPython] N_element060  label="N_element : 032"  # scripted group (container) (typed FeaturePython)
  n = 5
  ref = N_element
FEATURE [App::DocumentObjectGroupPython] O_element121  label="O_element : 074"  # scripted group (container) (typed FeaturePython)
  n = 5
  ref = O_element
FEATURE [App::DocumentObjectGroupPython] G4_DNA_GUANOSINE  # scripted group (container) (typed FeaturePython)
  Dunit = g/cm3
  Dvalue = 1
  Group = -> [H_element131,C_element141,N_element060,O_element121]
  conduct = 2
  density = 1
  expand = 3
  formula = G4_DNA_GUANOSINE
  name = G4_DNA_GUANOSINE
  specific = 4
FEATURE [App::DocumentObjectGroupPython] H_element132  label="H_element : 079"  # scripted group (container) (typed FeaturePython)
  n = 10
  ref = H_element
FEATURE [App::DocumentObjectGroupPython] C_element142  label="C_element : 087"  # scripted group (container) (typed FeaturePython)
  n = 9
  ref = C_element
FEATURE [App::DocumentObjectGroupPython] N_element061  label="N_element : 033"  # scripted group (container) (typed FeaturePython)
  n = 3
  ref = N_element
FEATURE [App::DocumentObjectGroupPython] O_element122  label="O_element : 075"  # scripted group (container) (typed FeaturePython)
  n = 5
  ref = O_element
FEATURE [App::DocumentObjectGroupPython] G4_DNA_CYTIDINE  # scripted group (container) (typed FeaturePython)
  Dunit = g/cm3
  Dvalue = 1
  Group = -> [H_element132,C_element142,N_element061,O_element122]
  conduct = 2
  density = 1
  expand = 3
  formula = G4_DNA_CYTIDINE
  name = G4_DNA_CYTIDINE
  specific = 4
FEATURE [App::DocumentObjectGroupPython] H_element133  label="H_element : 080"  # scripted group (container) (typed FeaturePython)
  n = 9
  ref = H_element
FEATURE [App::DocumentObjectGroupPython] C_element143  label="C_element : 088"  # scripted group (container) (typed FeaturePython)
  n = 9
  ref = C_element
FEATURE [App::DocumentObjectGroupPython] N_element062  label="N_element : 034"  # scripted group (container) (typed FeaturePython)
  n = 2
  ref = N_element
FEATURE [App::DocumentObjectGroupPython] O_element123  label="O_element : 076"  # scripted group (container) (typed FeaturePython)
  n = 6
  ref = O_element
FEATURE [App::DocumentObjectGroupPython] G4_DNA_URIDINE  # scripted group (container) (typed FeaturePython)
  Dunit = g/cm3
  Dvalue = 1
  Group = -> [H_element133,C_element143,N_element062,O_element123]
  conduct = 2
  density = 1
  expand = 3
  formula = G4_DNA_URIDINE
  name = G4_DNA_URIDINE
  specific = 4
FEATURE [App::DocumentObjectGroupPython] H_element134  label="H_element : 081"  # scripted group (container) (typed FeaturePython)
  n = 11
  ref = H_element
FEATURE [App::DocumentObjectGroupPython] C_element144  label="C_element : 089"  # scripted group (container) (typed FeaturePython)
  n = 10
  ref = C_element
FEATURE [App::DocumentObjectGroupPython] N_element063  label="N_element : 035"  # scripted group (container) (typed FeaturePython)
  n = 2
  ref = N_element
FEATURE [App::DocumentObjectGroupPython] O_element124  label="O_element : 077"  # scripted group (container) (typed FeaturePython)
  n = 6
  ref = O_element
FEATURE [App::DocumentObjectGroupPython] G4_DNA_METHYLURIDINE  # scripted group (container) (typed FeaturePython)
  Dunit = g/cm3
  Dvalue = 1
  Group = -> [H_element134,C_element144,N_element063,O_element124]
  conduct = 2
  density = 1
  expand = 3
  formula = G4_DNA_METHYLURIDINE
  name = G4_DNA_METHYLURIDINE
  specific = 4
FEATURE [App::DocumentObjectGroupPython] P_element014  label="P_element : 003"  # scripted group (container) (typed FeaturePython)
  n = 1
  ref = P_element
FEATURE [App::DocumentObjectGroupPython] O_element125  label="O_element : 078"  # scripted group (container) (typed FeaturePython)
  n = 3
  ref = O_element
FEATURE [App::DocumentObjectGroupPython] G4_DNA_MONOPHOSPHATE  # scripted group (container) (typed FeaturePython)
  Dunit = g/cm3
  Dvalue = 1
  Group = -> [P_element014,O_element125]
  conduct = 2
  density = 1
  expand = 3
  formula = G4_DNA_MONOPHOSPHATE
  name = G4_DNA_MONOPHOSPHATE
  specific = 4
FEATURE [App::DocumentObjectGroupPython] H_element135  label="H_element : 082"  # scripted group (container) (typed FeaturePython)
  n = 10
  ref = H_element
FEATURE [App::DocumentObjectGroupPython] C_element145  label="C_element : 090"  # scripted group (container) (typed FeaturePython)
  n = 10
  ref = C_element
FEATURE [App::DocumentObjectGroupPython] N_element064  label="N_element : 036"  # scripted group (container) (typed FeaturePython)
  n = 5
  ref = N_element
FEATURE [App::DocumentObjectGroupPython] O_element126  label="O_element : 079"  # scripted group (container) (typed FeaturePython)
  n = 7
  ref = O_element
FEATURE [App::DocumentObjectGroupPython] P_element015  label="P_element : 004"  # scripted group (container) (typed FeaturePython)
  n = 1
  ref = P_element
FEATURE [App::DocumentObjectGroupPython] G4_DNA_A  # scripted group (container) (typed FeaturePython)
  Dunit = g/cm3
  Dvalue = 1
  Group = -> [H_element135,C_element145,N_element064,O_element126,P_element015]
  conduct = 2
  density = 1
  expand = 3
  formula = G4_DNA_A
  name = G4_DNA_A
  specific = 4
FEATURE [App::DocumentObjectGroupPython] H_element136  label="H_element : 083"  # scripted group (container) (typed FeaturePython)
  n = 10
  ref = H_element
FEATURE [App::DocumentObjectGroupPython] C_element146  label="C_element : 091"  # scripted group (container) (typed FeaturePython)
  n = 10
  ref = C_element
FEATURE [App::DocumentObjectGroupPython] N_element065  label="N_element : 037"  # scripted group (container) (typed FeaturePython)
  n = 5
  ref = N_element
FEATURE [App::DocumentObjectGroupPython] O_element127  label="O_element : 8"  # scripted group (container) (typed FeaturePython)
  n = 8
  ref = O_element
FEATURE [App::DocumentObjectGroupPython] P_element016  label="P_element : 005"  # scripted group (container) (typed FeaturePython)
  n = 1
  ref = P_element
FEATURE [App::DocumentObjectGroupPython] G4_DNA_G  # scripted group (container) (typed FeaturePython)
  Dunit = g/cm3
  Dvalue = 1
  Group = -> [H_element136,C_element146,N_element065,O_element127,P_element016]
  conduct = 2
  density = 1
  expand = 3
  formula = G4_DNA_G
  name = G4_DNA_G
  specific = 4
FEATURE [App::DocumentObjectGroupPython] H_element137  label="H_element : 084"  # scripted group (container) (typed FeaturePython)
  n = 10
  ref = H_element
FEATURE [App::DocumentObjectGroupPython] C_element147  label="C_element : 092"  # scripted group (container) (typed FeaturePython)
  n = 9
  ref = C_element
FEATURE [App::DocumentObjectGroupPython] N_element066  label="N_element : 038"  # scripted group (container) (typed FeaturePython)
  n = 3
  ref = N_element
FEATURE [App::DocumentObjectGroupPython] O_element128  label="O_element : 080"  # scripted group (container) (typed FeaturePython)
  n = 8
  ref = O_element
FEATURE [App::DocumentObjectGroupPython] P_element017  label="P_element : 006"  # scripted group (container) (typed FeaturePython)
  n = 1
  ref = P_element
FEATURE [App::DocumentObjectGroupPython] G4_DNA_C  # scripted group (container) (typed FeaturePython)
  Dunit = g/cm3
  Dvalue = 1
  Group = -> [H_element137,C_element147,N_element066,O_element128,P_element017]
  conduct = 2
  density = 1
  expand = 3
  formula = G4_DNA_C
  name = G4_DNA_C
  specific = 4
FEATURE [App::DocumentObjectGroupPython] H_element138  label="H_element : 085"  # scripted group (container) (typed FeaturePython)
  n = 9
  ref = H_element
FEATURE [App::DocumentObjectGroupPython] C_element148  label="C_element : 093"  # scripted group (container) (typed FeaturePython)
  n = 9
  ref = C_element
FEATURE [App::DocumentObjectGroupPython] N_element067  label="N_element : 039"  # scripted group (container) (typed FeaturePython)
  n = 2
  ref = N_element
FEATURE [App::DocumentObjectGroupPython] O_element129  label="O_element : 9"  # scripted group (container) (typed FeaturePython)
  n = 9
  ref = O_element
FEATURE [App::DocumentObjectGroupPython] P_element018  label="P_element : 007"  # scripted group (container) (typed FeaturePython)
  n = 1
  ref = P_element
FEATURE [App::DocumentObjectGroupPython] G4_DNA_U  # scripted group (container) (typed FeaturePython)
  Dunit = g/cm3
  Dvalue = 1
  Group = -> [H_element138,C_element148,N_element067,O_element129,P_element018]
  conduct = 2
  density = 1
  expand = 3
  formula = G4_DNA_U
  name = G4_DNA_U
  specific = 4
FEATURE [App::DocumentObjectGroupPython] H_element139  label="H_element : 086"  # scripted group (container) (typed FeaturePython)
  n = 11
  ref = H_element
FEATURE [App::DocumentObjectGroupPython] C_element149  label="C_element : 094"  # scripted group (container) (typed FeaturePython)
  n = 10
  ref = C_element
FEATURE [App::DocumentObjectGroupPython] N_element068  label="N_element : 040"  # scripted group (container) (typed FeaturePython)
  n = 2
  ref = N_element
FEATURE [App::DocumentObjectGroupPython] O_element130  label="O_element : 081"  # scripted group (container) (typed FeaturePython)
  n = 9
  ref = O_element
FEATURE [App::DocumentObjectGroupPython] P_element019  label="P_element : 008"  # scripted group (container) (typed FeaturePython)
  n = 1
  ref = P_element
FEATURE [App::DocumentObjectGroupPython] G4_DNA_MU  # scripted group (container) (typed FeaturePython)
  Dunit = g/cm3
  Dvalue = 1
  Group = -> [H_element139,C_element149,N_element068,O_element130,P_element019]
  conduct = 2
  density = 1
  expand = 3
  formula = G4_DNA_MU
  name = G4_DNA_MU
  specific = 4
FEATURE [App::DocumentObjectGroupPython] BioChemical  # scripted group (container) (typed FeaturePython)
  Group = -> [G4_CYTOSINE,G4_THYMINE,G4_URACIL,G4_DNA_ADENINE,G4_DNA_GUANINE,G4_DNA_CYTOSINE,G4_DNA_THYMINE,G4_DNA_URACIL,G4_DNA_ADENOSINE,G4_DNA_GUANOSINE,G4_DNA_CYTIDINE,G4_DNA_URIDINE,G4_DNA_METHYLURIDINE,G4_DNA_MONOPHOSPHATE,G4_DNA_A,G4_DNA_G,G4_DNA_C,G4_DNA_U,G4_DNA_MU]
FEATURE [App::DocumentObjectGroupPython] G4Materials  # scripted group (container) (typed FeaturePython)
  Group = -> [NIST,Element,HEP,Space,BioChemical]
  version = 1
FEATURE [App::DocumentObjectGroupPython] Geant4  # scripted group (container) (typed FeaturePython)
  Group = -> [G4Isotopes,G4Elements,G4Materials]
FEATURE [App::DocumentObjectGroupPython] Materials  # scripted group (container) (typed FeaturePython)
  Group = -> [Geant4]
FEATURE [Part::FeaturePython] GDMLBox_WorldBox  # WARN: FeaturePython — macro-defined, semantics opaque (R4)
  lunit = 2
  material = 5
  x = 100
  y = 100
  z = 100
FEATURE [Part::FeaturePython] GDMLBox_Box  # WARN: FeaturePython — macro-defined, semantics opaque (R4)
  Placement = pos=(30,0,0) rot=(0,0,1;0rad)
  lunit = 2
  material = 0
  x = 10
  y = 10
  z = 10
FEATURE [Part::FeaturePython] GDMLTorus  # WARN: FeaturePython — macro-defined, semantics opaque (R4)
  Placement = pos=(30,0,0) rot=(0,1,0;1.5708rad)
  aunit = deg
  deltaphi = 360
  lunit = 2
  material = 0
  rmax = 2
  rmin = 0
  rtor = 8
  startphi = 0
FEATURE [Part::MultiFuse] Fusion
  Shapes = -> [GDMLBox_Box,GDMLTorus]
FEATURE [Part::FeaturePython] Array  # Draft array (typed FeaturePython)
  AlwaysSyncPlacement = false
  Angle = 180
  ArrayType = 1
  Axis = (0,0,1)
  Base = -> Fusion
  Center = (0,0,0)
  Count = 5
  ExpandArray = false
  Fuse = false
  IntervalAxis = (0,0,0)
  IntervalX = (50,0,0)
  IntervalY = (0,50,0)
  IntervalZ = (0,0,50)
  NumberCircles = 3
  NumberPolar = 5
  NumberX = 2
  NumberY = 2
  NumberZ = 1
  PlacementList = 5 placements: [(0,0,0),(0,0,0),(0,0,0),(0,0,0),(0,0,0)]
  RadialDistance = 50
  ScaleList = (5) [(1,1,1),(1,1,1),(1,1,1),(1,1,1),(1,1,1)]
  Symmetry = 1
  TangentialDistance = 25
FEATURE [App::Part] Part001
  Group = -> [Array]
  Origin = -> Origin004
FEATURE [App::Part] worldVOL
  Group = -> [GDMLBox_WorldBox,Part001]
  Origin = -> Origin
